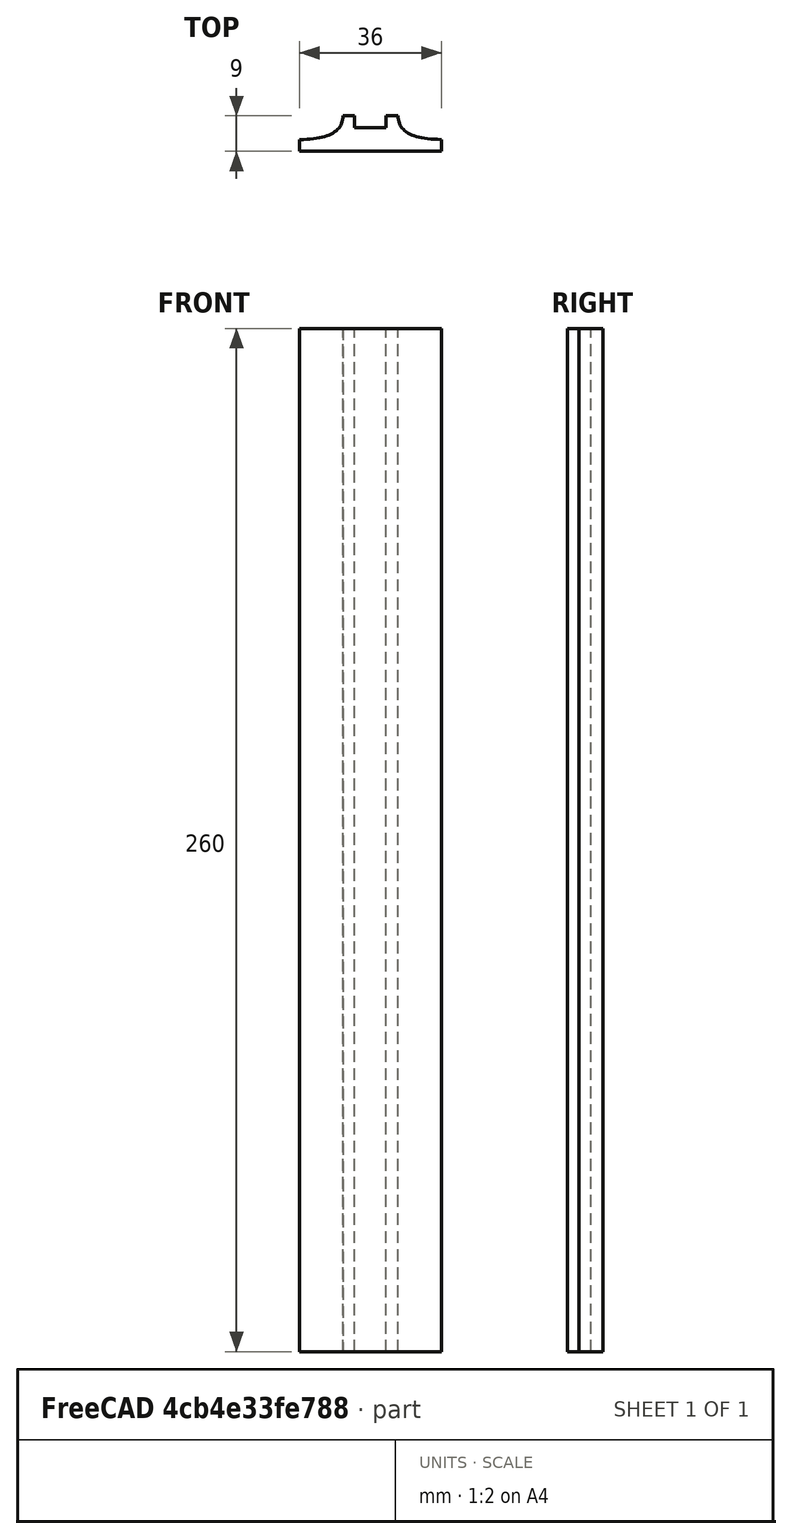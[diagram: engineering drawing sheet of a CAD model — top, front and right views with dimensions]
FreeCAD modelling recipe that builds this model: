
FCSTD DOCUMENT  (FreeCAD 0.19R0.19.2)
Label: laptopStand300.FCStd
License: All rights reserved
LicenseURL: http://en.wikipedia.org/wiki/All_rights_reserved
objects: Sketcher::SketchObject×11, Part::Extrusion×1
note: 12 computed .brp shape members not serialized (recipe doc carries the construction recipe); baked Part::Feature solids carry a one-line shape summary decoded from their .brp

FEATURE [Sketcher::SketchObject] Sketch001  label="legTop"
  FullyConstrained = true
  MapMode = 4
  Placement = pos=(0,0,0) rot=(0.57735,0.57735,0.57735;2.0944rad)
  sketch-geometry (41):
    g0: BSplineCurve PolesCount=3 KnotsCount=2 Degree=2 IsPeriodic=0
    g1: ArcOfCircle CenterX=73.1223 CenterY=-32.291 CenterZ=0 NormalX=0 NormalY=0 NormalZ=1 AngleXU=0 Radius=13 StartAngle=5.92268 EndAngle=9.06428
    g2: ArcOfCircle CenterX=66.7816 CenterY=-49.1439 CenterZ=0 NormalX=0 NormalY=0 NormalZ=1 AngleXU=0 Radius=13 StartAngle=2.78068 EndAngle=5.92131
    g3-g6: Circle x4 (B-spline internal-alignment scaffolding for g7; pole/knot coordinates omitted)
    g7: BSplineCurve PolesCount=4 KnotsCount=2 Degree=3 IsPeriodic=0
    g8: GeomPoint X=28.8094 Y=-19.0875 Z=0
    g9: GeomPoint X=47.0443 Y=-50.4712 Z=0
    g10: Circle CenterX=53.5586 CenterY=-23.2695 CenterZ=0 NormalX=0 NormalY=0 NormalZ=1 AngleXU=0 Radius=3.24518
    g11: LineSegment StartX=17.2232 StartY=-16.0875 StartZ=0 EndX=17.2232 EndY=-19.0875 EndZ=0
    g12: ArcOfCircle CenterX=17.2475 CenterY=-181.166 CenterZ=0 NormalX=0 NormalY=0 NormalZ=1 AngleXU=0 Radius=13 StartAngle=5.92268 EndAngle=7.49361
    g13: ArcOfCircle CenterX=29.5716 CenterY=-148.408 CenterZ=0 NormalX=0 NormalY=0 NormalZ=1 AngleXU=0 Radius=13 StartAngle=4.35228 EndAngle=5.92131
    g14: ArcOfCircle CenterX=35.8967 CenterY=-131.555 CenterZ=0 NormalX=0 NormalY=0 NormalZ=1 AngleXU=0 Radius=13 StartAngle=5.92268 EndAngle=7.49902
    g15: ArcOfCircle CenterX=48.1805 CenterY=-98.7782 CenterZ=0 NormalX=0 NormalY=0 NormalZ=1 AngleXU=0 Radius=13 StartAngle=4.34921 EndAngle=5.92131
    g16: ArcOfCircle CenterX=54.5183 CenterY=-81.9247 CenterZ=0 NormalX=0 NormalY=0 NormalZ=1 AngleXU=0 Radius=13 StartAngle=5.92268 EndAngle=8.70432
    g17: ArcOfCircle CenterX=20.184 CenterY=-217.506 CenterZ=0 NormalX=0 NormalY=0 NormalZ=1 AngleXU=0 Radius=3.81084 StartAngle=1.88136 EndAngle=6.80465
    g18: ArcOfCircle CenterX=36.3663 CenterY=-113.042 CenterZ=0 NormalX=0 NormalY=0 NormalZ=1 AngleXU=0 Radius=3.60555 StartAngle=0.230024 EndAngle=5.3372
    g19: ArcOfCircle CenterX=17.7945 CenterY=-162.686 CenterZ=0 NormalX=0 NormalY=0 NormalZ=1 AngleXU=0 Radius=3.60555 StartAngle=0.230024 EndAngle=5.3372
    g20: ArcOfCircle CenterX=49.8795 CenterY=-62.6074 CenterZ=0 NormalX=0 NormalY=0 NormalZ=1 AngleXU=0 Radius=3.84187 StartAngle=4.46973 EndAngle=9.40343
    g21: LineSegment StartX=48.9563 StartY=-66.3367 StartZ=0 EndX=44.7488 EndY=-73.3482 EndZ=0
    g22: LineSegment StartX=41.085 StartY=-66.3176 StartZ=0 EndX=46.0385 EndY=-62.5254 EndZ=0
    g23: LineSegment StartX=47.0443 StartY=-50.4712 StartZ=0 EndX=41.085 EndY=-66.3176 EndZ=0
    g24: LineSegment StartX=17.2232 StartY=-16.0875 StartZ=0 EndX=117.223 EndY=-16.0875 EndZ=0
    g25: LineSegment StartX=28.8094 StartY=-19.0875 StartZ=0 EndX=17.2232 EndY=-19.0875 EndZ=0
    g26: LineSegment StartX=117.223 StartY=-16.0875 StartZ=0 EndX=117.223 EndY=-19.0875 EndZ=0
    g27: LineSegment StartX=85.2866 StartY=-36.8766 StartZ=0 EndX=78.9396 EndY=-53.7463 EndZ=0
    g28: LineSegment StartX=60.9579 StartY=-27.7053 StartZ=0 EndX=54.6191 EndY=-44.5532 EndZ=0
    g29: LineSegment StartX=23.4884 StartY=-215.608 StartZ=0 EndX=94.6579 EndY=-26.1359 EndZ=0
    g30: LineSegment StartX=19.0195 StartY=-213.878 StartZ=0 EndX=29.4118 EndY=-185.752 EndZ=0
    g31: LineSegment StartX=22.7134 StartY=-166.661 StartZ=0 EndX=21.8316 EndY=-169.001 EndZ=0
    g32: LineSegment StartX=19.9036 StartY=-165.61 StartZ=0 EndX=22.7134 EndY=-166.661 EndZ=0
    g33: LineSegment StartX=21.3051 StartY=-161.864 StartZ=0 EndX=24.1149 EndY=-162.915 EndZ=0
    g34: LineSegment StartX=24.1149 StartY=-162.915 StartZ=0 EndX=24.9906 EndY=-160.574 EndZ=0
    g35: LineSegment StartX=41.7296 StartY=-153.01 StartZ=0 EndX=48.061 EndY=-136.14 EndZ=0
    g36: LineSegment StartX=41.2852 StartY=-117.017 StartZ=0 EndX=40.4148 EndY=-119.365 EndZ=0
    g37: LineSegment StartX=38.4753 StartY=-115.966 StartZ=0 EndX=41.2852 EndY=-117.017 EndZ=0
    g38: LineSegment StartX=39.8769 StartY=-112.22 StartZ=0 EndX=42.6867 EndY=-113.271 EndZ=0
    g39: LineSegment StartX=42.6867 StartY=-113.271 StartZ=0 EndX=43.5622 EndY=-110.93 EndZ=0
    g40: LineSegment StartX=66.6827 StartY=-86.5104 StartZ=0 EndX=60.3386 EndY=-103.381 EndZ=0
  constraints (65):
    c: Block(g0)
    c: Block(g1)
    c: Block(g2)
    c: Weight(g3) = 1
    c: Equal(g3,g4)
    c: Equal(g3,g5)
    c: Equal(g3,g6)
    c: InternalAlignment(g3-g6 -> g7) x4
    c: InternalAlignment(g8,g7)
    c: InternalAlignment(g9,g7)
    c: Block(g10)
    c: Block(g7)
    c: Vertical(g11)
    c: Block(g12)
    c: Block(g13)
    c: Block(g14)
    c: Block(g15)
    c: Block(g16)
    c: Block(g17)
    c: Block(g18)
    c: Block(g19)
    c: Block(g20)
    c: Coincident(g21,g20)
    c: Coincident(g21,g16)
    c: Coincident(g22,g20)
    c: Block(g22)
    c: Coincident(g23,g7)
    c: Coincident(g23,g22)
    c: Coincident(g24,g11)
    c: Horizontal(g24)
    c: Coincident(g25,g7)
    c: Coincident(g25,g11)
    c: Horizontal(g25)
    c: Coincident(g26,g24)
    c: Coincident(g26,g0)
    c: Vertical(g26)
    c: Block(g24)
    c: Coincident(g27,g1)
    c: Coincident(g27,g2)
    c: Coincident(g28,g1)
    c: Coincident(g28,g2)
    c: Coincident(g29,g17)
    c: Coincident(g29,g0)
    c: Coincident(g30,g17)
    c: Coincident(g30,g12)
    c: Coincident(g31,g12)
    c: Coincident(g32,g19)
    c: Coincident(g32,g31)
    c: Block(g31)
    c: Coincident(g33,g19)
    c: Coincident(g34,g33)
    c: Coincident(g34,g13)
    c: Block(g34)
    c: Coincident(g35,g13)
    c: Coincident(g35,g14)
    c: Coincident(g36,g14)
    c: Coincident(g37,g18)
    c: Coincident(g37,g36)
    c: Block(g36)
    c: Coincident(g38,g18)
    c: Coincident(g39,g38)
    c: Coincident(g39,g15)
    c: Block(g39)
    c: Coincident(g40,g16)
    c: Coincident(g40,g15)
FEATURE [Sketcher::SketchObject] Sketch002
  FullyConstrained = true
  sketch-geometry (20):
    g0: LineSegment StartX=-2.77179 StartY=-200.304 StartZ=0 EndX=5.22821 EndY=-200.304 EndZ=0
    g1: LineSegment StartX=5.22821 StartY=-200.304 StartZ=0 EndX=5.22821 EndY=-197.304 EndZ=0
    g2: LineSegment StartX=-2.77179 StartY=-200.304 StartZ=0 EndX=-2.77179 EndY=-197.304 EndZ=0
    g3: LineSegment StartX=5.22821 StartY=-197.304 StartZ=0 EndX=8.22821 EndY=-197.304 EndZ=0
    g4: LineSegment StartX=-2.77179 StartY=-197.304 StartZ=0 EndX=-5.77179 EndY=-197.304 EndZ=0
    g5: LineSegment StartX=19.2282 StartY=-203.304 StartZ=0 EndX=19.2282 EndY=-206.304 EndZ=0
    g6: LineSegment StartX=-16.7718 StartY=-203.304 StartZ=0 EndX=-16.7718 EndY=-206.304 EndZ=0
    g7: LineSegment StartX=-16.7718 StartY=-206.304 StartZ=0 EndX=19.2282 EndY=-206.304 EndZ=0
    g8: Circle CenterX=-16.7718 CenterY=-203.304 CenterZ=0 NormalX=0 NormalY=0 NormalZ=1 AngleXU=0 Radius=1
    g9: Circle CenterX=-5.77179 CenterY=-203.304 CenterZ=0 NormalX=0 NormalY=0 NormalZ=1 AngleXU=0 Radius=1
    g10: Circle CenterX=-5.77179 CenterY=-197.304 CenterZ=0 NormalX=0 NormalY=0 NormalZ=1 AngleXU=0 Radius=1
    g11: BSplineCurve PolesCount=3 KnotsCount=2 Degree=2 IsPeriodic=0
    g12: GeomPoint X=-16.7718 Y=-203.304 Z=0
    g13: GeomPoint X=-5.77179 Y=-197.304 Z=0
    g14: Circle CenterX=19.2282 CenterY=-203.304 CenterZ=0 NormalX=0 NormalY=0 NormalZ=1 AngleXU=0 Radius=1
    g15: Circle CenterX=8.22821 CenterY=-203.304 CenterZ=0 NormalX=0 NormalY=0 NormalZ=1 AngleXU=0 Radius=1
    g16: Circle CenterX=8.22821 CenterY=-197.304 CenterZ=0 NormalX=0 NormalY=0 NormalZ=1 AngleXU=0 Radius=1
    g17: BSplineCurve PolesCount=3 KnotsCount=2 Degree=2 IsPeriodic=0
    g18: GeomPoint X=19.2282 Y=-203.304 Z=0
    g19: GeomPoint X=8.22821 Y=-197.304 Z=0
  constraints (41):
    c: Horizontal(g0)
    c: Distance(g0) = 8
    c: Coincident(g1,g0)
    c: Vertical(g1)
    c: Distance(g1) = 3
    c: Coincident(g2,g0)
    c: Vertical(g2)
    c: Distance(g2) = 3
    c: Coincident(g3,g1)
    c: Horizontal(g3)
    c: Distance(g3) = 3
    c: Coincident(g4,g2)
    c: Horizontal(g4)
    c: Distance(g4) = 3
    c: Vertical(g5)
    c: Vertical(g6)
    c: Coincident(g7,g6)
    c: Coincident(g7,g5)
    c: Weight(g8) = 1
    c: Equal(g8,g9)
    c: Equal(g8,g10)
    c: Coincident(g11,g4)
    c: InternalAlignment(g8,g11)
    c: InternalAlignment(g9,g11)
    c: InternalAlignment(g10,g11)
    c: InternalAlignment(g12,g11)
    c: InternalAlignment(g13,g11)
    c: Coincident(g17,g5)
    c: Weight(g14) = 1
    c: Equal(g14,g15)
    c: Equal(g14,g16)
    c: Coincident(g17,g3)
    c: InternalAlignment(g14,g17)
    c: InternalAlignment(g15,g17)
    c: InternalAlignment(g16,g17)
    c: InternalAlignment(g18,g17)
    c: InternalAlignment(g19,g17)
    c: Block(g7)
    c: Block(g17)
    c: Block(g11)
    c: Block(g6)
FEATURE [Part::Extrusion] Extrude003
  Base = -> Sketch002
  Dir = (0,0,1)
  DirMode = 2
  FaceMakerClass = Part::FaceMakerBullseye
  LengthFwd = 260
  LengthRev = 0
  Solid = true
  Symmetric = false
FEATURE [Sketcher::SketchObject] Sketch003  label="original"
  FullyConstrained = false
  sketch-geometry (469):
    g0: LineSegment StartX=-42.9272 StartY=136.221 StartZ=0 EndX=-42.9272 EndY=-103.779 EndZ=0
    g1: LineSegment StartX=407.073 StartY=136.221 StartZ=0 EndX=407.073 EndY=-103.779 EndZ=0
    g2: ArcOfCircle CenterX=-26.9272 CenterY=-83.7794 CenterZ=0 NormalX=0 NormalY=0 NormalZ=1 AngleXU=0 Radius=8 StartAngle=3.14159 EndAngle=6.28319
    g3: ArcOfCircle CenterX=391.073 CenterY=-83.7794 CenterZ=0 NormalX=0 NormalY=0 NormalZ=1 AngleXU=0 Radius=8 StartAngle=3.14159 EndAngle=6.28319
    g4: Circle CenterX=175.022 CenterY=27.0628 CenterZ=0 NormalX=0 NormalY=0 NormalZ=1 AngleXU=0 Radius=1
    g5: Circle CenterX=179.022 CenterY=24.8665 CenterZ=0 NormalX=0 NormalY=0 NormalZ=1 AngleXU=0 Radius=1
    g6: Circle CenterX=179.022 CenterY=27.0628 CenterZ=0 NormalX=0 NormalY=0 NormalZ=1 AngleXU=0 Radius=1
    g7: BSplineCurve PolesCount=3 KnotsCount=2 Degree=2 IsPeriodic=0
    g8: GeomPoint X=175.022 Y=27.0628 Z=0
    g9: GeomPoint X=179.022 Y=27.0628 Z=0
    g10: Circle CenterX=189.124 CenterY=27.0628 CenterZ=0 NormalX=0 NormalY=0 NormalZ=1 AngleXU=0 Radius=1
    g11: Circle CenterX=185.124 CenterY=24.8665 CenterZ=0 NormalX=0 NormalY=0 NormalZ=1 AngleXU=0 Radius=1
    g12: Circle CenterX=185.124 CenterY=27.0628 CenterZ=0 NormalX=0 NormalY=0 NormalZ=1 AngleXU=0 Radius=1
    g13: BSplineCurve PolesCount=3 KnotsCount=2 Degree=2 IsPeriodic=0
    g14: GeomPoint X=189.124 Y=27.0628 Z=0
    g15: GeomPoint X=185.124 Y=27.0628 Z=0
    g16: Circle CenterX=175.022 CenterY=5.37834 CenterZ=0 NormalX=0 NormalY=0 NormalZ=1 AngleXU=0 Radius=1
    g17: Circle CenterX=179.022 CenterY=7.57463 CenterZ=0 NormalX=0 NormalY=0 NormalZ=1 AngleXU=0 Radius=1
    g18: Circle CenterX=179.022 CenterY=5.34704 CenterZ=0 NormalX=0 NormalY=0 NormalZ=1 AngleXU=0 Radius=1
    g19: BSplineCurve PolesCount=3 KnotsCount=2 Degree=2 IsPeriodic=0
    g20: GeomPoint X=175.022 Y=5.37834 Z=0
    g21: GeomPoint X=179.022 Y=5.34704 Z=0
    g22: Circle CenterX=189.124 CenterY=5.37834 CenterZ=0 NormalX=0 NormalY=0 NormalZ=1 AngleXU=0 Radius=1
    g23: Circle CenterX=185.124 CenterY=7.57463 CenterZ=0 NormalX=0 NormalY=0 NormalZ=1 AngleXU=0 Radius=1
    g24: Circle CenterX=185.124 CenterY=5.34704 CenterZ=0 NormalX=0 NormalY=0 NormalZ=1 AngleXU=0 Radius=1
    g25: BSplineCurve PolesCount=3 KnotsCount=2 Degree=2 IsPeriodic=0
    g26: GeomPoint X=189.124 Y=5.37834 Z=0
    g27: GeomPoint X=185.124 Y=5.34704 Z=0
    g28: Circle CenterX=165.871 CenterY=18.1458 CenterZ=0 NormalX=0 NormalY=0 NormalZ=1 AngleXU=0 Radius=1
    g29: Circle CenterX=169.377 CenterY=16.2206 CenterZ=0 NormalX=0 NormalY=0 NormalZ=1 AngleXU=0 Radius=1
    g30: Circle CenterX=165.871 CenterY=14.2956 CenterZ=0 NormalX=0 NormalY=0 NormalZ=1 AngleXU=0 Radius=1
    g31: BSplineCurve PolesCount=3 KnotsCount=2 Degree=2 IsPeriodic=0
    g32: GeomPoint X=165.871 Y=18.1458 Z=0
    g33: GeomPoint X=165.871 Y=14.2956 Z=0
    g34: Circle CenterX=198.275 CenterY=18.1318 CenterZ=0 NormalX=0 NormalY=0 NormalZ=1 AngleXU=0 Radius=1
    g35: Circle CenterX=194.768 CenterY=16.2206 CenterZ=0 NormalX=0 NormalY=0 NormalZ=1 AngleXU=0 Radius=1
    g36: Circle CenterX=198.264 CenterY=14.2963 CenterZ=0 NormalX=0 NormalY=0 NormalZ=1 AngleXU=0 Radius=1
    g37: BSplineCurve PolesCount=3 KnotsCount=2 Degree=2 IsPeriodic=0
    g38: GeomPoint X=198.275 Y=18.1318 Z=0
    g39: GeomPoint X=198.264 Y=14.2963 Z=0
    g40: LineSegment StartX=407.073 StartY=-103.779 StartZ=0 EndX=-42.9272 EndY=-103.779 EndZ=0
    g41: Circle CenterX=125.607 CenterY=54.1951 CenterZ=0 NormalX=0 NormalY=0 NormalZ=1 AngleXU=0 Radius=1
    g42: Circle CenterX=139.632 CenterY=46.4944 CenterZ=0 NormalX=0 NormalY=0 NormalZ=1 AngleXU=0 Radius=1
    g43: Circle CenterX=127.326 CenterY=56.7187 CenterZ=0 NormalX=0 NormalY=0 NormalZ=1 AngleXU=0 Radius=1
    g44: BSplineCurve PolesCount=3 KnotsCount=2 Degree=2 IsPeriodic=0
    g45: GeomPoint X=125.607 Y=54.1951 Z=0
    g46: GeomPoint X=127.326 Y=56.7187 Z=0
    g47: Circle CenterX=236.824 CenterY=56.7187 CenterZ=0 NormalX=0 NormalY=0 NormalZ=1 AngleXU=0 Radius=1
    g48: Circle CenterX=224.513 CenterY=46.4944 CenterZ=0 NormalX=0 NormalY=0 NormalZ=1 AngleXU=0 Radius=1
    g49: Circle CenterX=238.538 CenterY=54.1951 CenterZ=0 NormalX=0 NormalY=0 NormalZ=1 AngleXU=0 Radius=1
    g50: BSplineCurve PolesCount=3 KnotsCount=2 Degree=2 IsPeriodic=0
    g51: GeomPoint X=236.824 Y=56.7187 Z=0
    g52: GeomPoint X=238.538 Y=54.1951 Z=0
    g53: Circle CenterX=238.538 CenterY=-21.7516 CenterZ=0 NormalX=0 NormalY=0 NormalZ=1 AngleXU=0 Radius=1
    g54: Circle CenterX=224.513 CenterY=-14.0532 CenterZ=0 NormalX=0 NormalY=0 NormalZ=1 AngleXU=0 Radius=1
    g55: Circle CenterX=236.584 CenterY=-24.2775 CenterZ=0 NormalX=0 NormalY=0 NormalZ=1 AngleXU=0 Radius=1
    g56: BSplineCurve PolesCount=3 KnotsCount=2 Degree=2 IsPeriodic=0
    g57: GeomPoint X=238.538 Y=-21.7516 Z=0
    g58: GeomPoint X=236.584 Y=-24.2775 Z=0
    g59: Circle CenterX=125.607 CenterY=-21.7539 CenterZ=0 NormalX=0 NormalY=0 NormalZ=1 AngleXU=0 Radius=1
    g60: Circle CenterX=139.632 CenterY=-14.0532 CenterZ=0 NormalX=0 NormalY=0 NormalZ=1 AngleXU=0 Radius=1
    g61: Circle CenterX=127.325 CenterY=-24.2775 CenterZ=0 NormalX=0 NormalY=0 NormalZ=1 AngleXU=0 Radius=1
    g62: BSplineCurve PolesCount=3 KnotsCount=2 Degree=2 IsPeriodic=0
    g63: GeomPoint X=125.607 Y=-21.7539 Z=0
    g64: GeomPoint X=127.325 Y=-24.2775 Z=0
    g65: Circle CenterX=302.996 CenterY=111.695 CenterZ=0 NormalX=0 NormalY=0 NormalZ=1 AngleXU=0 Radius=1
    g66: Circle CenterX=306.073 CenterY=114.251 CenterZ=0 NormalX=0 NormalY=0 NormalZ=1 AngleXU=0 Radius=1
    g67: Circle CenterX=306.073 CenterY=110.251 CenterZ=0 NormalX=0 NormalY=0 NormalZ=1 AngleXU=0 Radius=1
    g68: BSplineCurve PolesCount=3 KnotsCount=2 Degree=2 IsPeriodic=0
    g69: GeomPoint X=302.996 Y=111.695 Z=0
    g70: GeomPoint X=306.073 Y=110.251 Z=0
    g71: Circle CenterX=306.073 CenterY=95.2763 CenterZ=0 NormalX=0 NormalY=0 NormalZ=1 AngleXU=0 Radius=1
    g72: Circle CenterX=306.073 CenterY=91.2763 CenterZ=0 NormalX=0 NormalY=0 NormalZ=1 AngleXU=0 Radius=1
    g73: Circle CenterX=302.567 CenterY=89.3511 CenterZ=0 NormalX=0 NormalY=0 NormalZ=1 AngleXU=0 Radius=1
    g74: BSplineCurve PolesCount=3 KnotsCount=2 Degree=2 IsPeriodic=0
    g75: GeomPoint X=306.073 Y=95.2763 Z=0
    g76: GeomPoint X=302.567 Y=89.3511 Z=0
    g77: LineSegment StartX=306.073 StartY=110.251 StartZ=0 EndX=306.073 EndY=95.2763 EndZ=0
    g78: LineSegment StartX=302.996 StartY=111.695 StartZ=0 EndX=236.824 EndY=56.7187 EndZ=0
    g79: LineSegment StartX=238.538 StartY=54.1951 StartZ=0 EndX=302.567 EndY=89.3511 EndZ=0
    g80: Circle CenterX=61.1496 CenterY=111.695 CenterZ=0 NormalX=0 NormalY=0 NormalZ=1 AngleXU=0 Radius=1
    g81: Circle CenterX=58.0728 CenterY=114.251 CenterZ=0 NormalX=0 NormalY=0 NormalZ=1 AngleXU=0 Radius=1
    g82: Circle CenterX=58.0728 CenterY=110.251 CenterZ=0 NormalX=0 NormalY=0 NormalZ=1 AngleXU=0 Radius=1
    g83: BSplineCurve PolesCount=3 KnotsCount=2 Degree=2 IsPeriodic=0
    g84: GeomPoint X=61.1496 Y=111.695 Z=0
    g85: GeomPoint X=58.0728 Y=110.251 Z=0
    g86: Circle CenterX=61.5791 CenterY=89.3511 CenterZ=0 NormalX=0 NormalY=0 NormalZ=1 AngleXU=0 Radius=1
    g87: Circle CenterX=58.0728 CenterY=91.2763 CenterZ=0 NormalX=0 NormalY=0 NormalZ=1 AngleXU=0 Radius=1
    g88: Circle CenterX=58.0728 CenterY=95.2763 CenterZ=0 NormalX=0 NormalY=0 NormalZ=1 AngleXU=0 Radius=1
    g89: BSplineCurve PolesCount=3 KnotsCount=2 Degree=2 IsPeriodic=0
    g90: GeomPoint X=61.5791 Y=89.3511 Z=0
    g91: GeomPoint X=58.0728 Y=95.2763 Z=0
    g92: LineSegment StartX=58.0728 StartY=110.251 StartZ=0 EndX=58.0728 EndY=95.2763 EndZ=0
    g93: LineSegment StartX=61.1496 StartY=111.695 StartZ=0 EndX=127.326 EndY=56.7187 EndZ=0
    g94: LineSegment StartX=125.607 StartY=54.1951 StartZ=0 EndX=61.5791 EndY=89.3511 EndZ=0
    g95: Circle CenterX=61.5791 CenterY=-56.9099 CenterZ=0 NormalX=0 NormalY=0 NormalZ=1 AngleXU=0 Radius=1
    g96: Circle CenterX=58.0728 CenterY=-58.8351 CenterZ=0 NormalX=0 NormalY=0 NormalZ=1 AngleXU=0 Radius=1
    g97: Circle CenterX=58.0728 CenterY=-62.8351 CenterZ=0 NormalX=0 NormalY=0 NormalZ=1 AngleXU=0 Radius=1
    g98: BSplineCurve PolesCount=3 KnotsCount=2 Degree=2 IsPeriodic=0
    g99: GeomPoint X=61.5791 Y=-56.9099 Z=0
    g100: GeomPoint X=58.0728 Y=-62.8351 Z=0
    g101: Circle CenterX=58.0728 CenterY=-77.8102 CenterZ=0 NormalX=0 NormalY=0 NormalZ=1 AngleXU=0 Radius=1
    g102: Circle CenterX=58.0728 CenterY=-81.8102 CenterZ=0 NormalX=0 NormalY=0 NormalZ=1 AngleXU=0 Radius=1
    g103: Circle CenterX=61.1496 CenterY=-79.2541 CenterZ=0 NormalX=0 NormalY=0 NormalZ=1 AngleXU=0 Radius=1
    g104: BSplineCurve PolesCount=3 KnotsCount=2 Degree=2 IsPeriodic=0
    g105: GeomPoint X=58.0728 Y=-77.8102 Z=0
    g106: GeomPoint X=61.1496 Y=-79.2541 Z=0
    g107: LineSegment StartX=58.0728 StartY=-62.8351 StartZ=0 EndX=58.0728 EndY=-77.8102 EndZ=0
    g108: LineSegment StartX=61.1496 StartY=-79.2541 StartZ=0 EndX=127.325 EndY=-24.2775 EndZ=0
    g109: LineSegment StartX=125.607 StartY=-21.7539 StartZ=0 EndX=61.5791 EndY=-56.9099 EndZ=0
    g110: Circle CenterX=302.567 CenterY=-56.9099 CenterZ=0 NormalX=0 NormalY=0 NormalZ=1 AngleXU=0 Radius=1
    g111: Circle CenterX=306.073 CenterY=-58.8351 CenterZ=0 NormalX=0 NormalY=0 NormalZ=1 AngleXU=0 Radius=1
    g112: Circle CenterX=306.073 CenterY=-62.8351 CenterZ=0 NormalX=0 NormalY=0 NormalZ=1 AngleXU=0 Radius=1
    g113: BSplineCurve PolesCount=3 KnotsCount=2 Degree=2 IsPeriodic=0
    g114: GeomPoint X=302.567 Y=-56.9099 Z=0
    g115: GeomPoint X=306.073 Y=-62.8351 Z=0
    g116: Circle CenterX=302.996 CenterY=-79.2541 CenterZ=0 NormalX=0 NormalY=0 NormalZ=1 AngleXU=0 Radius=1
    g117: Circle CenterX=306.073 CenterY=-81.8102 CenterZ=0 NormalX=0 NormalY=0 NormalZ=1 AngleXU=0 Radius=1
    g118: Circle CenterX=306.073 CenterY=-77.8102 CenterZ=0 NormalX=0 NormalY=0 NormalZ=1 AngleXU=0 Radius=1
    g119: BSplineCurve PolesCount=3 KnotsCount=2 Degree=2 IsPeriodic=0
    g120: GeomPoint X=302.996 Y=-79.2541 Z=0
    g121: GeomPoint X=306.073 Y=-77.8102 Z=0
    g122: LineSegment StartX=306.073 StartY=-62.8351 StartZ=0 EndX=306.073 EndY=-77.8102 EndZ=0
    g123: LineSegment StartX=302.996 StartY=-79.2541 StartZ=0 EndX=236.584 EndY=-24.2775 EndZ=0
    g124: LineSegment StartX=238.538 StartY=-21.7516 StartZ=0 EndX=302.567 EndY=-56.9099 EndZ=0
    g125: Circle CenterX=61.6457 CenterY=-88.8112 CenterZ=0 NormalX=0 NormalY=0 NormalZ=1 AngleXU=0 Radius=1
    g126: Circle CenterX=58.0728 CenterY=-91.7794 CenterZ=0 NormalX=0 NormalY=0 NormalZ=1 AngleXU=0 Radius=1
    g127: Circle CenterX=63.9135 CenterY=-91.7791 CenterZ=0 NormalX=0 NormalY=0 NormalZ=1 AngleXU=0 Radius=1
    g128: BSplineCurve PolesCount=3 KnotsCount=2 Degree=2 IsPeriodic=0
    g129: GeomPoint X=61.6457 Y=-88.8112 Z=0
    g130: GeomPoint X=63.9135 Y=-91.7791 Z=0
    g131: Circle CenterX=179.022 CenterY=-85.8163 CenterZ=0 NormalX=0 NormalY=0 NormalZ=1 AngleXU=0 Radius=1
    g132: Circle CenterX=179.022 CenterY=-91.7794 CenterZ=0 NormalX=0 NormalY=0 NormalZ=1 AngleXU=0 Radius=1
    g133: Circle CenterX=171.895 CenterY=-91.7791 CenterZ=0 NormalX=0 NormalY=0 NormalZ=1 AngleXU=0 Radius=1
    g134: BSplineCurve PolesCount=3 KnotsCount=2 Degree=2 IsPeriodic=0
    g135: GeomPoint X=179.022 Y=-85.8163 Z=0
    g136: GeomPoint X=171.895 Y=-91.7791 Z=0
    g137: Circle CenterX=185.124 CenterY=-86.2028 CenterZ=0 NormalX=0 NormalY=0 NormalZ=1 AngleXU=0 Radius=1
    g138: Circle CenterX=185.124 CenterY=-91.7794 CenterZ=0 NormalX=0 NormalY=0 NormalZ=1 AngleXU=0 Radius=1
    g139: Circle CenterX=191.747 CenterY=-91.7794 CenterZ=0 NormalX=0 NormalY=0 NormalZ=1 AngleXU=0 Radius=1
    g140: BSplineCurve PolesCount=3 KnotsCount=2 Degree=2 IsPeriodic=0
    g141: GeomPoint X=185.124 Y=-86.2028 Z=0
    g142: GeomPoint X=191.747 Y=-91.7794 Z=0
    g143: Circle CenterX=299.888 CenterY=-86.6413 CenterZ=0 NormalX=0 NormalY=0 NormalZ=1 AngleXU=0 Radius=1
    g144: Circle CenterX=306.073 CenterY=-91.7794 CenterZ=0 NormalX=0 NormalY=0 NormalZ=1 AngleXU=0 Radius=1
    g145: Circle CenterX=298.776 CenterY=-91.7794 CenterZ=0 NormalX=0 NormalY=0 NormalZ=1 AngleXU=0 Radius=1
    g146: BSplineCurve PolesCount=3 KnotsCount=2 Degree=2 IsPeriodic=0
    g147: GeomPoint X=299.888 Y=-86.6413 Z=0
    g148: GeomPoint X=298.776 Y=-91.7794 Z=0
    g149: LineSegment StartX=189.124 StartY=5.37834 StartZ=0 EndX=299.888 EndY=-86.6413 EndZ=0
    g150: LineSegment StartX=298.776 StartY=-91.7794 StartZ=0 EndX=191.747 EndY=-91.7794 EndZ=0
    g151: LineSegment StartX=185.124 StartY=-86.2028 StartZ=0 EndX=185.124 EndY=5.34704 EndZ=0
    g152: LineSegment StartX=179.022 StartY=5.34704 StartZ=0 EndX=179.022 EndY=-85.8163 EndZ=0
    g153: LineSegment StartX=171.895 StartY=-91.7791 StartZ=0 EndX=63.9135 EndY=-91.7791 EndZ=0
    g154: LineSegment StartX=61.6457 StartY=-88.8112 StartZ=0 EndX=175.022 EndY=5.37834 EndZ=0
    g155: Circle CenterX=302.073 CenterY=124.221 CenterZ=0 NormalX=0 NormalY=0 NormalZ=1 AngleXU=0 Radius=1
    g156: Circle CenterX=306.073 CenterY=124.221 CenterZ=0 NormalX=0 NormalY=0 NormalZ=1 AngleXU=0 Radius=1
    g157: Circle CenterX=302.996 CenterY=121.665 CenterZ=0 NormalX=0 NormalY=0 NormalZ=1 AngleXU=0 Radius=1
    g158: BSplineCurve PolesCount=3 KnotsCount=2 Degree=2 IsPeriodic=0
    g159: GeomPoint X=302.073 Y=124.221 Z=0
    g160: GeomPoint X=302.996 Y=121.665 Z=0
    g161: Circle CenterX=189.124 CenterY=124.221 CenterZ=0 NormalX=0 NormalY=0 NormalZ=1 AngleXU=0 Radius=1
    g162: Circle CenterX=185.124 CenterY=124.221 CenterZ=0 NormalX=0 NormalY=0 NormalZ=1 AngleXU=0 Radius=1
    g163: Circle CenterX=185.124 CenterY=120.221 CenterZ=0 NormalX=0 NormalY=0 NormalZ=1 AngleXU=0 Radius=1
    g164: BSplineCurve PolesCount=3 KnotsCount=2 Degree=2 IsPeriodic=0
    g165: GeomPoint X=189.124 Y=124.221 Z=0
    g166: GeomPoint X=185.124 Y=120.221 Z=0
    g167: Circle CenterX=175.022 CenterY=124.221 CenterZ=0 NormalX=0 NormalY=0 NormalZ=1 AngleXU=0 Radius=1
    g168: Circle CenterX=179.022 CenterY=124.221 CenterZ=0 NormalX=0 NormalY=0 NormalZ=1 AngleXU=0 Radius=1
    g169: Circle CenterX=179.022 CenterY=120.221 CenterZ=0 NormalX=0 NormalY=0 NormalZ=1 AngleXU=0 Radius=1
    g170: BSplineCurve PolesCount=3 KnotsCount=2 Degree=2 IsPeriodic=0
    g171: GeomPoint X=175.022 Y=124.221 Z=0
    g172: GeomPoint X=179.022 Y=120.221 Z=0
    g173: Circle CenterX=62.0728 CenterY=124.221 CenterZ=0 NormalX=0 NormalY=0 NormalZ=1 AngleXU=0 Radius=1
    g174: Circle CenterX=58.0728 CenterY=124.221 CenterZ=0 NormalX=0 NormalY=0 NormalZ=1 AngleXU=0 Radius=1
    g175: Circle CenterX=61.1496 CenterY=121.665 CenterZ=0 NormalX=0 NormalY=0 NormalZ=1 AngleXU=0 Radius=1
    g176: BSplineCurve PolesCount=3 KnotsCount=2 Degree=2 IsPeriodic=0
    g177: GeomPoint X=62.0728 Y=124.221 Z=0
    g178: GeomPoint X=61.1496 Y=121.665 Z=0
    g179: LineSegment StartX=179.022 StartY=120.221 StartZ=0 EndX=179.022 EndY=27.0628 EndZ=0
    g180: LineSegment StartX=185.124 StartY=27.0628 StartZ=0 EndX=185.124 EndY=120.221 EndZ=0
    g181: LineSegment StartX=302.996 StartY=121.665 StartZ=0 EndX=189.124 EndY=27.0628 EndZ=0
    g182: LineSegment StartX=175.022 StartY=27.0628 StartZ=0 EndX=61.1496 EndY=121.665 EndZ=0
    g183: Circle CenterX=61.5791 CenterY=75.4095 CenterZ=0 NormalX=0 NormalY=0 NormalZ=1 AngleXU=0 Radius=1
    g184: Circle CenterX=58.0728 CenterY=77.3346 CenterZ=0 NormalX=0 NormalY=0 NormalZ=1 AngleXU=0 Radius=1
    g185: Circle CenterX=58.0728 CenterY=73.3346 CenterZ=0 NormalX=0 NormalY=0 NormalZ=1 AngleXU=0 Radius=1
    g186: BSplineCurve PolesCount=3 KnotsCount=2 Degree=2 IsPeriodic=0
    g187: GeomPoint X=61.5791 Y=75.4095 Z=0
    g188: GeomPoint X=58.0728 Y=73.3346 Z=0
    g189: Circle CenterX=58.0728 CenterY=-40.8935 CenterZ=0 NormalX=0 NormalY=0 NormalZ=1 AngleXU=0 Radius=1
    g190: Circle CenterX=58.0728 CenterY=-44.8935 CenterZ=0 NormalX=0 NormalY=0 NormalZ=1 AngleXU=0 Radius=1
    g191: Circle CenterX=61.5791 CenterY=-42.9683 CenterZ=0 NormalX=0 NormalY=0 NormalZ=1 AngleXU=0 Radius=1
    g192: BSplineCurve PolesCount=3 KnotsCount=2 Degree=2 IsPeriodic=0
    g193: GeomPoint X=58.0728 Y=-40.8935 Z=0
    g194: GeomPoint X=61.5791 Y=-42.9683 Z=0
    g195: LineSegment StartX=61.5791 StartY=-42.9683 StartZ=0 EndX=165.871 EndY=14.2956 EndZ=0
    g196: LineSegment StartX=165.871 StartY=18.1458 StartZ=0 EndX=61.5791 EndY=75.4095 EndZ=0
    g197: LineSegment StartX=58.0728 StartY=73.3346 StartZ=0 EndX=58.0728 EndY=-40.8935 EndZ=0
    g198: Circle CenterX=302.567 CenterY=-42.9683 CenterZ=0 NormalX=0 NormalY=0 NormalZ=1 AngleXU=0 Radius=1
    g199: Circle CenterX=306.073 CenterY=-44.8935 CenterZ=0 NormalX=0 NormalY=0 NormalZ=1 AngleXU=0 Radius=1
    g200: Circle CenterX=306.073 CenterY=-40.8935 CenterZ=0 NormalX=0 NormalY=0 NormalZ=1 AngleXU=0 Radius=1
    g201: BSplineCurve PolesCount=3 KnotsCount=2 Degree=2 IsPeriodic=0
    g202: GeomPoint X=302.567 Y=-42.9683 Z=0
    g203: GeomPoint X=306.073 Y=-40.8935 Z=0
    g204: Circle CenterX=306.073 CenterY=73.3346 CenterZ=0 NormalX=0 NormalY=0 NormalZ=1 AngleXU=0 Radius=1
    g205: Circle CenterX=306.073 CenterY=77.3346 CenterZ=0 NormalX=0 NormalY=0 NormalZ=1 AngleXU=0 Radius=1
    g206: Circle CenterX=302.535 CenterY=75.4095 CenterZ=0 NormalX=0 NormalY=0 NormalZ=1 AngleXU=0 Radius=1
    g207: BSplineCurve PolesCount=3 KnotsCount=2 Degree=2 IsPeriodic=0
    g208: GeomPoint X=306.073 Y=73.3346 Z=0
    g209: GeomPoint X=302.535 Y=75.4095 Z=0
    g210: LineSegment StartX=302.567 StartY=-42.9683 StartZ=0 EndX=198.264 EndY=14.2963 EndZ=0
    g211: LineSegment StartX=198.275 StartY=18.1318 StartZ=0 EndX=302.535 EndY=75.4095 EndZ=0
    g212: LineSegment StartX=306.073 StartY=73.3346 StartZ=0 EndX=306.073 EndY=-40.8935 EndZ=0
    g213: LineSegment StartX=322.073 StartY=105.865 StartZ=0 EndX=328.643 EndY=105.865 EndZ=0
    g214: LineSegment StartX=318.073 StartY=120.221 StartZ=0 EndX=318.073 EndY=109.865 EndZ=0
    g215: LineSegment StartX=336.157 StartY=107.779 StartZ=0 EndX=362.567 EndY=122.294 EndZ=0
    g216: Circle CenterX=362.073 CenterY=124.221 CenterZ=0 NormalX=0 NormalY=0 NormalZ=1 AngleXU=0 Radius=1
    g217: Circle CenterX=366.073 CenterY=124.221 CenterZ=0 NormalX=0 NormalY=0 NormalZ=1 AngleXU=0 Radius=1
    g218: Circle CenterX=362.567 CenterY=122.294 CenterZ=0 NormalX=0 NormalY=0 NormalZ=1 AngleXU=0 Radius=1
    g219: BSplineCurve PolesCount=3 KnotsCount=2 Degree=2 IsPeriodic=0
    g220: GeomPoint X=362.073 Y=124.221 Z=0
    g221: GeomPoint X=362.567 Y=122.294 Z=0
    g222: Circle CenterX=322.073 CenterY=124.221 CenterZ=0 NormalX=0 NormalY=0 NormalZ=1 AngleXU=0 Radius=1
    g223: Circle CenterX=318.073 CenterY=124.221 CenterZ=0 NormalX=0 NormalY=0 NormalZ=1 AngleXU=0 Radius=1
    g224: Circle CenterX=318.073 CenterY=120.221 CenterZ=0 NormalX=0 NormalY=0 NormalZ=1 AngleXU=0 Radius=1
    g225: BSplineCurve PolesCount=3 KnotsCount=2 Degree=2 IsPeriodic=0
    g226: GeomPoint X=322.073 Y=124.221 Z=0
    g227: GeomPoint X=318.073 Y=120.221 Z=0
    g228: Circle CenterX=322.073 CenterY=105.865 CenterZ=0 NormalX=0 NormalY=0 NormalZ=1 AngleXU=0 Radius=1
    g229: Circle CenterX=318.073 CenterY=105.865 CenterZ=0 NormalX=0 NormalY=0 NormalZ=1 AngleXU=0 Radius=1
    g230: Circle CenterX=318.073 CenterY=109.865 CenterZ=0 NormalX=0 NormalY=0 NormalZ=1 AngleXU=0 Radius=1
    g231: BSplineCurve PolesCount=3 KnotsCount=2 Degree=2 IsPeriodic=0
    g232: GeomPoint X=322.073 Y=105.865 Z=0
    g233: GeomPoint X=318.073 Y=109.865 Z=0
    g234: Circle CenterX=336.157 CenterY=107.779 CenterZ=0 NormalX=0 NormalY=0 NormalZ=1 AngleXU=0 Radius=1
    g235: Circle CenterX=332.651 CenterY=105.853 CenterZ=0 NormalX=0 NormalY=0 NormalZ=1 AngleXU=0 Radius=1
    g236: Circle CenterX=328.643 CenterY=105.865 CenterZ=0 NormalX=0 NormalY=0 NormalZ=1 AngleXU=0 Radius=1
    g237: BSplineCurve PolesCount=3 KnotsCount=2 Degree=2 IsPeriodic=0
    g238: GeomPoint X=336.157 Y=107.779 Z=0
    g239: GeomPoint X=328.643 Y=105.865 Z=0
    g240: LineSegment StartX=322.073 StartY=124.221 StartZ=0 EndX=362.073 EndY=124.221 EndZ=0
    g241: Circle CenterX=371.567 CenterY=-80.8644 CenterZ=0 NormalX=0 NormalY=0 NormalZ=1 AngleXU=0 Radius=1
    g242: Circle CenterX=375.073 CenterY=-82.7896 CenterZ=0 NormalX=0 NormalY=0 NormalZ=1 AngleXU=0 Radius=1
    g243: Circle CenterX=375.073 CenterY=-78.7896 CenterZ=0 NormalX=0 NormalY=0 NormalZ=1 AngleXU=0 Radius=1
    g244: BSplineCurve PolesCount=3 KnotsCount=2 Degree=2 IsPeriodic=0
    g245: GeomPoint X=371.567 Y=-80.8644 Z=0
    g246: GeomPoint X=375.073 Y=-78.7896 Z=0
    g247: Circle CenterX=321.579 CenterY=-53.4075 CenterZ=0 NormalX=0 NormalY=0 NormalZ=1 AngleXU=0 Radius=1
    g248: Circle CenterX=318.073 CenterY=-51.4823 CenterZ=0 NormalX=0 NormalY=0 NormalZ=1 AngleXU=0 Radius=1
    g249: Circle CenterX=318.073 CenterY=-47.4805 CenterZ=0 NormalX=0 NormalY=0 NormalZ=1 AngleXU=0 Radius=1
    g250: BSplineCurve PolesCount=3 KnotsCount=2 Degree=2 IsPeriodic=0
    g251: GeomPoint X=321.579 Y=-53.4075 Z=0
    g252: GeomPoint X=318.073 Y=-47.4805 Z=0
    g253: LineSegment StartX=371.567 StartY=-80.8644 StartZ=0 EndX=321.579 EndY=-53.4075 EndZ=0
    g254: Circle CenterX=321.579 CenterY=-67.3492 CenterZ=0 NormalX=0 NormalY=0 NormalZ=1 AngleXU=0 Radius=1
    g255: Circle CenterX=318.073 CenterY=-65.424 CenterZ=0 NormalX=0 NormalY=0 NormalZ=1 AngleXU=0 Radius=1
    g256: Circle CenterX=318.073 CenterY=-69.424 CenterZ=0 NormalX=0 NormalY=0 NormalZ=1 AngleXU=0 Radius=1
    g257: BSplineCurve PolesCount=3 KnotsCount=2 Degree=2 IsPeriodic=0
    g258: GeomPoint X=321.579 Y=-67.3492 Z=0
    g259: GeomPoint X=318.073 Y=-69.424 Z=0
    g260: Circle CenterX=362.567 CenterY=-89.8542 CenterZ=0 NormalX=0 NormalY=0 NormalZ=1 AngleXU=0 Radius=1
    g261: Circle CenterX=366.073 CenterY=-91.7794 CenterZ=0 NormalX=0 NormalY=0 NormalZ=1 AngleXU=0 Radius=1
    g262: Circle CenterX=362.073 CenterY=-91.7794 CenterZ=0 NormalX=0 NormalY=0 NormalZ=1 AngleXU=0 Radius=1
    g263: BSplineCurve PolesCount=3 KnotsCount=2 Degree=2 IsPeriodic=0
    g264: GeomPoint X=362.567 Y=-89.8542 Z=0
    g265: GeomPoint X=362.073 Y=-91.7794 Z=0
    g266: Circle CenterX=322.073 CenterY=-91.7794 CenterZ=0 NormalX=0 NormalY=0 NormalZ=1 AngleXU=0 Radius=1
    g267: Circle CenterX=318.073 CenterY=-91.7794 CenterZ=0 NormalX=0 NormalY=0 NormalZ=1 AngleXU=0 Radius=1
    g268: Circle CenterX=318.073 CenterY=-87.7794 CenterZ=0 NormalX=0 NormalY=0 NormalZ=1 AngleXU=0 Radius=1
    g269: BSplineCurve PolesCount=3 KnotsCount=2 Degree=2 IsPeriodic=0
    g270: GeomPoint X=322.073 Y=-91.7794 Z=0
    g271: GeomPoint X=318.073 Y=-87.7794 Z=0
    g272: LineSegment StartX=362.567 StartY=-89.8542 StartZ=0 EndX=321.579 EndY=-67.3492 EndZ=0
    g273: LineSegment StartX=318.073 StartY=-69.424 StartZ=0 EndX=318.073 EndY=-87.7794 EndZ=0
    g274: LineSegment StartX=322.073 StartY=-91.7794 StartZ=0 EndX=362.073 EndY=-91.7794 EndZ=0
    g275: Circle CenterX=2.07281 CenterY=124.221 CenterZ=0 NormalX=0 NormalY=0 NormalZ=1 AngleXU=0 Radius=1
    g276: Circle CenterX=1.57905 CenterY=122.295 CenterZ=0 NormalX=0 NormalY=0 NormalZ=1 AngleXU=0 Radius=1
    g277: BSplineCurve PolesCount=3 KnotsCount=2 Degree=2 IsPeriodic=0
    g278: GeomPoint X=2.07281 Y=124.221 Z=0
    g279: GeomPoint X=1.57905 Y=122.295 Z=0
    g280: Circle CenterX=42.0728 CenterY=124.221 CenterZ=0 NormalX=0 NormalY=0 NormalZ=1 AngleXU=0 Radius=1
    g281: Circle CenterX=46.0728 CenterY=124.221 CenterZ=0 NormalX=0 NormalY=0 NormalZ=1 AngleXU=0 Radius=1
    g282: Circle CenterX=46.0728 CenterY=120.221 CenterZ=0 NormalX=0 NormalY=0 NormalZ=1 AngleXU=0 Radius=1
    g283: BSplineCurve PolesCount=3 KnotsCount=2 Degree=2 IsPeriodic=0
    g284: GeomPoint X=42.0728 Y=124.221 Z=0
    g285: GeomPoint X=46.0728 Y=120.221 Z=0
    g286: Circle CenterX=46.0728 CenterY=109.865 CenterZ=0 NormalX=0 NormalY=0 NormalZ=1 AngleXU=0 Radius=1
    g287: Circle CenterX=46.0728 CenterY=105.865 CenterZ=0 NormalX=0 NormalY=0 NormalZ=1 AngleXU=0 Radius=1
    g288: Circle CenterX=42.0728 CenterY=105.865 CenterZ=0 NormalX=0 NormalY=0 NormalZ=1 AngleXU=0 Radius=1
    g289: BSplineCurve PolesCount=3 KnotsCount=2 Degree=2 IsPeriodic=0
    g290: GeomPoint X=46.0728 Y=109.865 Z=0
    g291: GeomPoint X=42.0728 Y=105.865 Z=0
    g292: Circle CenterX=35.5028 CenterY=105.865 CenterZ=0 NormalX=0 NormalY=0 NormalZ=1 AngleXU=0 Radius=1
    g293: Circle CenterX=31.5028 CenterY=105.865 CenterZ=0 NormalX=0 NormalY=0 NormalZ=1 AngleXU=0 Radius=1
    g294: Circle CenterX=27.9965 CenterY=107.79 CenterZ=0 NormalX=0 NormalY=0 NormalZ=1 AngleXU=0 Radius=1
    g295: BSplineCurve PolesCount=3 KnotsCount=2 Degree=2 IsPeriodic=0
    g296: GeomPoint X=35.5028 Y=105.865 Z=0
    g297: GeomPoint X=27.9965 Y=107.79 Z=0
    g298: LineSegment StartX=2.07281 StartY=124.221 StartZ=0 EndX=42.0728 EndY=124.221 EndZ=0
    g299: LineSegment StartX=46.0728 StartY=120.221 StartZ=0 EndX=46.0728 EndY=109.865 EndZ=0
    g300: LineSegment StartX=42.0728 StartY=105.865 StartZ=0 EndX=35.5028 EndY=105.865 EndZ=0
    g301: LineSegment StartX=27.9965 StartY=107.79 StartZ=0 EndX=1.57905 EndY=122.295 EndZ=0
    g302: Circle CenterX=42.5666 CenterY=-67.3492 CenterZ=0 NormalX=0 NormalY=0 NormalZ=1 AngleXU=0 Radius=1
    g303: Circle CenterX=46.0728 CenterY=-65.424 CenterZ=0 NormalX=0 NormalY=0 NormalZ=1 AngleXU=0 Radius=1
    g304: Circle CenterX=46.0728 CenterY=-69.424 CenterZ=0 NormalX=0 NormalY=0 NormalZ=1 AngleXU=0 Radius=1
    g305: BSplineCurve PolesCount=3 KnotsCount=2 Degree=2 IsPeriodic=0
    g306: GeomPoint X=42.5666 Y=-67.3492 Z=0
    g307: GeomPoint X=46.0728 Y=-69.424 Z=0
    g308: Circle CenterX=46.0728 CenterY=-87.7794 CenterZ=0 NormalX=0 NormalY=0 NormalZ=1 AngleXU=0 Radius=1
    g309: Circle CenterX=46.0728 CenterY=-91.7794 CenterZ=0 NormalX=0 NormalY=0 NormalZ=1 AngleXU=0 Radius=1
    g310: Circle CenterX=42.0728 CenterY=-91.7794 CenterZ=0 NormalX=0 NormalY=0 NormalZ=1 AngleXU=0 Radius=1
    g311: BSplineCurve PolesCount=3 KnotsCount=2 Degree=2 IsPeriodic=0
    g312: GeomPoint X=46.0728 Y=-87.7794 Z=0
    g313: GeomPoint X=42.0728 Y=-91.7794 Z=0
    g314: Circle CenterX=2.07281 CenterY=-91.7794 CenterZ=0 NormalX=0 NormalY=0 NormalZ=1 AngleXU=0 Radius=1
    g315: Circle CenterX=-1.92719 CenterY=-91.7794 CenterZ=0 NormalX=0 NormalY=0 NormalZ=1 AngleXU=0 Radius=1
    g316: Circle CenterX=1.57905 CenterY=-89.8542 CenterZ=0 NormalX=0 NormalY=0 NormalZ=1 AngleXU=0 Radius=1
    g317: BSplineCurve PolesCount=3 KnotsCount=2 Degree=2 IsPeriodic=0
    g318: GeomPoint X=2.07281 Y=-91.7794 Z=0
    g319: GeomPoint X=1.57905 Y=-89.8542 Z=0
    g320: LineSegment StartX=2.07281 StartY=-91.7794 StartZ=0 EndX=42.0728 EndY=-91.7794 EndZ=0
    g321: LineSegment StartX=46.0728 StartY=-87.7794 StartZ=0 EndX=46.0728 EndY=-69.424 EndZ=0
    g322: LineSegment StartX=42.5666 StartY=-67.3492 StartZ=0 EndX=1.57905 EndY=-89.8542 EndZ=0
    g323: Circle CenterX=322.073 CenterY=76.4095 CenterZ=0 NormalX=0 NormalY=0 NormalZ=1 AngleXU=0 Radius=4
    g324: BSplineCurve PolesCount=3 KnotsCount=2 Degree=2 IsPeriodic=0
    g325: GeomPoint X=318.073 Y=72.4095 Z=0
    g326: GeomPoint X=322.073 Y=76.4095 Z=0
    g327: Circle CenterX=375.073 CenterY=72.4095 CenterZ=0 NormalX=0 NormalY=0 NormalZ=1 AngleXU=0 Radius=1
    g328: Circle CenterX=375.073 CenterY=76.4095 CenterZ=0 NormalX=0 NormalY=0 NormalZ=1 AngleXU=0 Radius=1
    g329: Circle CenterX=371.073 CenterY=76.4095 CenterZ=0 NormalX=0 NormalY=0 NormalZ=1 AngleXU=0 Radius=1
    g330: BSplineCurve PolesCount=3 KnotsCount=2 Degree=2 IsPeriodic=0
    g331: GeomPoint X=375.073 Y=72.4095 Z=0
    g332: GeomPoint X=371.073 Y=76.4095 Z=0
    g333: LineSegment StartX=322.073 StartY=76.4095 StartZ=0 EndX=371.073 EndY=76.4095 EndZ=0
    g334: LineSegment StartX=318.073 StartY=72.4095 StartZ=0 EndX=318.073 EndY=-47.4805 EndZ=0
    g335: LineSegment StartX=375.073 StartY=72.4095 StartZ=0 EndX=375.073 EndY=-78.7896 EndZ=0
    g336: ArcOfCircle CenterX=-26.9272 CenterY=22.1087 CenterZ=0 NormalX=0 NormalY=0 NormalZ=1 AngleXU=0 Radius=4 StartAngle=5e-16 EndAngle=3.14159
    g337: LineSegment StartX=-22.9272 StartY=22.1087 StartZ=0 EndX=-18.9272 EndY=-83.7794 EndZ=0
    g338: LineSegment StartX=-34.9272 StartY=-83.7794 StartZ=0 EndX=-30.9272 EndY=22.1087 EndZ=0
    g339: ArcOfCircle CenterX=391.073 CenterY=22.1087 CenterZ=0 NormalX=0 NormalY=0 NormalZ=1 AngleXU=0 Radius=4 StartAngle=0 EndAngle=3.14159
    g340: LineSegment StartX=387.073 StartY=22.1087 StartZ=0 EndX=383.073 EndY=-83.7794 EndZ=0
    g341: LineSegment StartX=395.073 StartY=22.1087 StartZ=0 EndX=399.073 EndY=-83.7794 EndZ=0
    g342: Circle CenterX=-10.9272 CenterY=-78.7794 CenterZ=0 NormalX=0 NormalY=0 NormalZ=1 AngleXU=0 Radius=1
    g343: Circle CenterX=-10.9272 CenterY=-82.7794 CenterZ=0 NormalX=0 NormalY=0 NormalZ=1 AngleXU=0 Radius=1
    g344: Circle CenterX=-7.42095 CenterY=-80.8542 CenterZ=0 NormalX=0 NormalY=0 NormalZ=1 AngleXU=0 Radius=1
    g345: BSplineCurve PolesCount=3 KnotsCount=2 Degree=2 IsPeriodic=0
    g346: GeomPoint X=-10.9272 Y=-78.7794 Z=0
    g347: GeomPoint X=-7.42095 Y=-80.8542 Z=0
    g348: Circle CenterX=42.5666 CenterY=-53.4075 CenterZ=0 NormalX=0 NormalY=0 NormalZ=1 AngleXU=0 Radius=1
    g349: Circle CenterX=46.0728 CenterY=-51.4823 CenterZ=0 NormalX=0 NormalY=0 NormalZ=1 AngleXU=0 Radius=1
    g350: Circle CenterX=46.0728 CenterY=-47.4823 CenterZ=0 NormalX=0 NormalY=0 NormalZ=1 AngleXU=0 Radius=1
    g351: BSplineCurve PolesCount=3 KnotsCount=2 Degree=2 IsPeriodic=0
    g352: GeomPoint X=42.5666 Y=-53.4075 Z=0
    g353: GeomPoint X=46.0728 Y=-47.4823 Z=0
    g354: Circle CenterX=46.0728 CenterY=72.4095 CenterZ=0 NormalX=0 NormalY=0 NormalZ=1 AngleXU=0 Radius=1
    g355: Circle CenterX=46.0728 CenterY=76.4095 CenterZ=0 NormalX=0 NormalY=0 NormalZ=1 AngleXU=0 Radius=1
    g356: Circle CenterX=42.0728 CenterY=76.4095 CenterZ=0 NormalX=0 NormalY=0 NormalZ=1 AngleXU=0 Radius=1
    g357: BSplineCurve PolesCount=3 KnotsCount=2 Degree=2 IsPeriodic=0
    g358: GeomPoint X=46.0728 Y=72.4095 Z=0
    g359: GeomPoint X=42.0728 Y=76.4095 Z=0
    g360: Circle CenterX=-6.92719 CenterY=76.4095 CenterZ=0 NormalX=0 NormalY=0 NormalZ=1 AngleXU=0 Radius=1
    g361: Circle CenterX=-10.9272 CenterY=76.4095 CenterZ=0 NormalX=0 NormalY=0 NormalZ=1 AngleXU=0 Radius=1
    g362: Circle CenterX=-10.9272 CenterY=72.4095 CenterZ=0 NormalX=0 NormalY=0 NormalZ=1 AngleXU=0 Radius=1
    g363: BSplineCurve PolesCount=3 KnotsCount=2 Degree=2 IsPeriodic=0
    g364: GeomPoint X=-6.92719 Y=76.4095 Z=0
    g365: GeomPoint X=-10.9272 Y=72.4095 Z=0
    g366: LineSegment StartX=-10.9272 StartY=72.4095 StartZ=0 EndX=-10.9272 EndY=-78.7794 EndZ=0
    g367: LineSegment StartX=-7.42095 StartY=-80.8542 StartZ=0 EndX=42.5666 EndY=-53.4075 EndZ=0
    g368: LineSegment StartX=46.0728 StartY=-47.4823 StartZ=0 EndX=46.0728 EndY=72.4095 EndZ=0
    g369: LineSegment StartX=42.0728 StartY=76.4095 StartZ=0 EndX=-6.92719 EndY=76.4095 EndZ=0
    g370: LineSegment StartX=-42.9272 StartY=136.221 StartZ=0 EndX=407.073 EndY=136.221 EndZ=0
    g371: LineSegment StartX=232.072 StartY=136.221 StartZ=0 EndX=220.072 EndY=136.221 EndZ=0
    g372: LineSegment StartX=232.072 StartY=136.221 StartZ=0 EndX=232.072 EndY=124.221 EndZ=0
    g373: LineSegment StartX=220.072 StartY=136.221 StartZ=0 EndX=220.072 EndY=124.221 EndZ=0
    g374: LineSegment StartX=220.072 StartY=136.221 StartZ=0 EndX=226.072 EndY=136.221 EndZ=0
    g375: LineSegment StartX=220.072 StartY=136.221 StartZ=0 EndX=220.072 EndY=130.221 EndZ=0
    g376: LineSegment StartX=220.072 StartY=124.221 StartZ=0 EndX=226.072 EndY=124.221 EndZ=0
    g377: LineSegment StartX=232.072 StartY=124.221 StartZ=0 EndX=232.072 EndY=127.221 EndZ=0
    g378: LineSegment StartX=232.072 StartY=136.221 StartZ=0 EndX=232.072 EndY=133.221 EndZ=0
    g379-g383: Circle x5 (B-spline internal-alignment scaffolding for g384; pole/knot coordinates omitted)
    g384: BSplineCurve PolesCount=5 KnotsCount=3 Degree=3 IsPeriodic=0
    g385: GeomPoint X=232.072 Y=133.221 Z=0
    g386: GeomPoint X=223.072 Y=130.221 Z=0
    g387: GeomPoint X=232.072 Y=127.221 Z=0
    g388: LineSegment StartX=189.124 StartY=124.221 StartZ=0 EndX=302.073 EndY=124.221 EndZ=0
    g389: LineSegment StartX=132.072 StartY=136.221 StartZ=0 EndX=132.072 EndY=124.221 EndZ=0
    g390: LineSegment StartX=132.072 StartY=136.221 StartZ=0 EndX=144.072 EndY=136.221 EndZ=0
    g391: LineSegment StartX=144.072 StartY=136.221 StartZ=0 EndX=144.072 EndY=124.221 EndZ=0
    g392: LineSegment StartX=144.072 StartY=136.221 StartZ=0 EndX=138.072 EndY=136.221 EndZ=0
    g393: LineSegment StartX=144.072 StartY=136.221 StartZ=0 EndX=144.072 EndY=130.221 EndZ=0
    g394: LineSegment StartX=132.072 StartY=136.221 StartZ=0 EndX=132.072 EndY=133.221 EndZ=0
    g395: LineSegment StartX=132.072 StartY=133.221 StartZ=0 EndX=132.072 EndY=127.221 EndZ=0
    g396-g400: Circle x5 (B-spline internal-alignment scaffolding for g401; pole/knot coordinates omitted)
    g401: BSplineCurve PolesCount=5 KnotsCount=3 Degree=3 IsPeriodic=0
    g402: GeomPoint X=132.072 Y=133.221 Z=0
    g403: GeomPoint X=141.072 Y=130.221 Z=0
    g404: GeomPoint X=132.072 Y=127.221 Z=0
    g405: LineSegment StartX=132.072 StartY=124.221 StartZ=0 EndX=175.022 EndY=124.221 EndZ=0
    g406: LineSegment StartX=62.0728 StartY=124.221 StartZ=0 EndX=132.072 EndY=124.221 EndZ=0
    g407: LineSegment StartX=132.072 StartY=136.221 StartZ=0 EndX=131.457 EndY=138.832 EndZ=0
    ... +61 more geometry lines
  constraints (808):
    c: Vertical(g0)
    c: Vertical(g1)
    c: Block(g1)
    c: Block(g0)
    c: Weight(g4) = 1
    c: Equal(g4,g5)
    c: Equal(g4,g6)
    c: InternalAlignment(g4,g7)
    c: InternalAlignment(g5,g7)
    c: InternalAlignment(g6,g7)
    c: InternalAlignment(g8,g7)
    c: InternalAlignment(g9,g7)
    c: Weight(g10) = 1
    c: Equal(g10,g11)
    c: Equal(g10,g12)
    c: InternalAlignment(g10,g13)
    c: InternalAlignment(g11,g13)
    c: InternalAlignment(g12,g13)
    c: InternalAlignment(g14,g13)
    c: InternalAlignment(g15,g13)
    c: Block(g13)
    c: Block(g7)
    c: Weight(g16) = 1
    c: Equal(g16,g17)
    c: Equal(g16,g18)
    c: InternalAlignment(g16,g19)
    c: InternalAlignment(g17,g19)
    c: InternalAlignment(g18,g19)
    c: InternalAlignment(g20,g19)
    c: InternalAlignment(g21,g19)
    c: Weight(g22) = 1
    c: Equal(g22,g23)
    c: Equal(g22,g24)
    c: InternalAlignment(g22,g25)
    c: InternalAlignment(g23,g25)
    c: InternalAlignment(g24,g25)
    c: InternalAlignment(g26,g25)
    c: InternalAlignment(g27,g25)
    c: Block(g25)
    c: Block(g19)
    c: Weight(g28) = 1
    c: Equal(g28,g29)
    c: Equal(g28,g30)
    c: InternalAlignment(g28,g31)
    c: InternalAlignment(g29,g31)
    c: InternalAlignment(g30,g31)
    c: InternalAlignment(g32,g31)
    c: InternalAlignment(g33,g31)
    c: Weight(g34) = 1
    c: Equal(g34,g35)
    c: Equal(g34,g36)
    c: InternalAlignment(g34,g37)
    c: InternalAlignment(g35,g37)
    c: InternalAlignment(g36,g37)
    c: InternalAlignment(g38,g37)
    c: InternalAlignment(g39,g37)
    c: Block(g31)
    c: Block(g37)
    c: Coincident(g40,g1)
    c: Coincident(g40,g0)
    c: Horizontal(g40)
    c: Distance(g40) = 450
    c: Weight(g41) = 1
    c: Equal(g41,g42)
    c: Equal(g41,g43)
    c: InternalAlignment(g41,g44)
    c: InternalAlignment(g42,g44)
    c: InternalAlignment(g43,g44)
    c: InternalAlignment(g45,g44)
    c: InternalAlignment(g46,g44)
    c: Block(g44)
    c: Weight(g47) = 1
    c: Equal(g47,g48)
    c: Equal(g47,g49)
    c: InternalAlignment(g47,g50)
    c: InternalAlignment(g48,g50)
    c: InternalAlignment(g49,g50)
    c: InternalAlignment(g51,g50)
    c: InternalAlignment(g52,g50)
    c: Block(g50)
    c: Weight(g53) = 1
    c: Equal(g53,g54)
    c: Equal(g53,g55)
    c: InternalAlignment(g53,g56)
    c: InternalAlignment(g54,g56)
    c: InternalAlignment(g55,g56)
    c: InternalAlignment(g57,g56)
    c: InternalAlignment(g58,g56)
    c: Block(g56)
    c: Weight(g59) = 1
    c: Equal(g59,g60)
    c: Equal(g59,g61)
    c: InternalAlignment(g59,g62)
    c: InternalAlignment(g60,g62)
    c: InternalAlignment(g61,g62)
    c: InternalAlignment(g63,g62)
    c: InternalAlignment(g64,g62)
    c: Block(g62)
    c: Weight(g65) = 1
    c: Equal(g65,g66)
    c: Equal(g65,g67)
    c: InternalAlignment(g65,g68)
    c: InternalAlignment(g66,g68)
    c: InternalAlignment(g67,g68)
    c: InternalAlignment(g69,g68)
    c: InternalAlignment(g70,g68)
    c: Weight(g71) = 1
    c: Equal(g71,g72)
    c: Equal(g71,g73)
    c: InternalAlignment(g71,g74)
    c: InternalAlignment(g72,g74)
    c: InternalAlignment(g73,g74)
    c: InternalAlignment(g75,g74)
    c: InternalAlignment(g76,g74)
    c: Block(g68)
    c: Block(g74)
    c: Coincident(g77,g68)
    c: Coincident(g77,g74)
    c: Vertical(g77)
    c: Coincident(g78,g68)
    c: Coincident(g78,g50)
    c: Coincident(g79,g50)
    c: Coincident(g79,g74)
    c: Weight(g80) = 1
    c: Equal(g80,g81)
    c: Equal(g80,g82)
    c: InternalAlignment(g80,g83)
    c: InternalAlignment(g81,g83)
    c: InternalAlignment(g82,g83)
    c: InternalAlignment(g84,g83)
    c: InternalAlignment(g85,g83)
    c: Weight(g86) = 1
    c: Equal(g86,g87)
    c: Equal(g86,g88)
    c: InternalAlignment(g86,g89)
    c: InternalAlignment(g87,g89)
    c: InternalAlignment(g88,g89)
    c: InternalAlignment(g90,g89)
    c: InternalAlignment(g91,g89)
    c: Block(g83)
    c: Block(g89)
    c: Coincident(g92,g83)
    c: Coincident(g92,g89)
    c: Vertical(g92)
    c: Coincident(g93,g83)
    c: Coincident(g93,g44)
    c: Coincident(g94,g44)
    c: Coincident(g94,g89)
    c: Weight(g95) = 1
    c: Equal(g95,g96)
    c: Equal(g95,g97)
    c: InternalAlignment(g95,g98)
    c: InternalAlignment(g96,g98)
    c: InternalAlignment(g97,g98)
    c: InternalAlignment(g99,g98)
    c: InternalAlignment(g100,g98)
    c: Weight(g101) = 1
    c: Equal(g101,g102)
    c: Equal(g101,g103)
    c: InternalAlignment(g101,g104)
    c: InternalAlignment(g102,g104)
    c: InternalAlignment(g103,g104)
    c: InternalAlignment(g105,g104)
    c: InternalAlignment(g106,g104)
    c: Block(g98)
    c: Block(g104)
    c: Coincident(g107,g98)
    c: Coincident(g107,g104)
    c: Vertical(g107)
    c: Coincident(g108,g104)
    c: Coincident(g108,g62)
    c: Coincident(g109,g62)
    c: Coincident(g109,g98)
    c: Weight(g110) = 1
    c: Equal(g110,g111)
    c: Equal(g110,g112)
    c: InternalAlignment(g110,g113)
    c: InternalAlignment(g111,g113)
    c: InternalAlignment(g112,g113)
    c: InternalAlignment(g114,g113)
    c: InternalAlignment(g115,g113)
    c: Weight(g116) = 1
    c: Equal(g116,g117)
    c: Equal(g116,g118)
    c: InternalAlignment(g116,g119)
    c: InternalAlignment(g117,g119)
    c: InternalAlignment(g118,g119)
    c: InternalAlignment(g120,g119)
    c: InternalAlignment(g121,g119)
    c: Block(g113)
    c: Block(g119)
    c: Coincident(g122,g113)
    c: Coincident(g122,g119)
    c: Vertical(g122)
    c: Coincident(g123,g119)
    c: Coincident(g123,g56)
    c: Coincident(g124,g56)
    c: Coincident(g124,g113)
    c: Weight(g125) = 1
    c: Equal(g125,g126)
    c: Equal(g125,g127)
    c: InternalAlignment(g125,g128)
    c: InternalAlignment(g126,g128)
    c: InternalAlignment(g127,g128)
    c: InternalAlignment(g129,g128)
    c: InternalAlignment(g130,g128)
    c: Weight(g131) = 1
    c: Equal(g131,g132)
    c: Equal(g131,g133)
    c: InternalAlignment(g131,g134)
    c: InternalAlignment(g132,g134)
    c: InternalAlignment(g133,g134)
    c: InternalAlignment(g135,g134)
    c: InternalAlignment(g136,g134)
    c: Weight(g137) = 1
    c: Equal(g137,g138)
    c: Equal(g137,g139)
    c: InternalAlignment(g137,g140)
    c: InternalAlignment(g138,g140)
    c: InternalAlignment(g139,g140)
    c: InternalAlignment(g141,g140)
    c: InternalAlignment(g142,g140)
    c: Weight(g143) = 1
    c: Equal(g143,g144)
    c: Equal(g143,g145)
    c: InternalAlignment(g143,g146)
    c: InternalAlignment(g144,g146)
    c: InternalAlignment(g145,g146)
    c: InternalAlignment(g147,g146)
    c: InternalAlignment(g148,g146)
    c: Block(g146)
    c: Block(g140)
    c: Block(g134)
    c: Block(g128)
    c: Coincident(g149,g25)
    c: Coincident(g149,g146)
    c: Coincident(g150,g146)
    c: Coincident(g150,g140)
    c: Horizontal(g150)
    c: Coincident(g151,g140)
    c: Coincident(g151,g25)
    c: Vertical(g151)
    c: Coincident(g152,g19)
    c: Coincident(g152,g134)
    c: Vertical(g152)
    c: Coincident(g153,g134)
    c: Coincident(g153,g128)
    c: Horizontal(g153)
    c: Coincident(g154,g128)
    c: Coincident(g154,g19)
    c: Weight(g155) = 1
    c: Equal(g155,g156)
    c: Equal(g155,g157)
    c: InternalAlignment(g155,g158)
    c: InternalAlignment(g156,g158)
    c: InternalAlignment(g157,g158)
    c: InternalAlignment(g159,g158)
    c: InternalAlignment(g160,g158)
    c: Weight(g161) = 1
    c: Equal(g161,g162)
    c: Equal(g161,g163)
    c: InternalAlignment(g161,g164)
    c: InternalAlignment(g162,g164)
    c: InternalAlignment(g163,g164)
    c: InternalAlignment(g165,g164)
    c: InternalAlignment(g166,g164)
    c: Weight(g167) = 1
    c: Equal(g167,g168)
    c: Equal(g167,g169)
    c: InternalAlignment(g167,g170)
    c: InternalAlignment(g168,g170)
    c: InternalAlignment(g169,g170)
    c: InternalAlignment(g171,g170)
    c: InternalAlignment(g172,g170)
    c: Weight(g173) = 1
    c: Equal(g173,g174)
    c: Equal(g173,g175)
    c: InternalAlignment(g173,g176)
    c: InternalAlignment(g174,g176)
    c: InternalAlignment(g175,g176)
    c: InternalAlignment(g177,g176)
    c: InternalAlignment(g178,g176)
    c: Block(g176)
    c: Block(g170)
    c: Block(g164)
    c: Block(g158)
    c: Coincident(g179,g170)
    c: Coincident(g179,g7)
    c: Vertical(g179)
    c: Coincident(g180,g13)
    c: Coincident(g180,g164)
    c: Vertical(g180)
    c: Coincident(g181,g158)
    c: Coincident(g181,g13)
    c: Coincident(g182,g7)
    c: Weight(g183) = 1
    c: Equal(g183,g184)
    c: Equal(g183,g185)
    c: InternalAlignment(g183,g186)
    c: InternalAlignment(g184,g186)
    c: InternalAlignment(g185,g186)
    c: InternalAlignment(g187,g186)
    c: InternalAlignment(g188,g186)
    c: Weight(g189) = 1
    c: Equal(g189,g190)
    c: Equal(g189,g191)
    c: InternalAlignment(g189,g192)
    c: InternalAlignment(g190,g192)
    c: InternalAlignment(g191,g192)
    c: InternalAlignment(g193,g192)
    c: InternalAlignment(g194,g192)
    c: Block(g192)
    c: Block(g186)
    c: Coincident(g195,g192)
    c: Coincident(g195,g31)
    c: Coincident(g196,g31)
    c: Coincident(g196,g186)
    c: Coincident(g197,g186)
    c: Coincident(g197,g192)
    c: Vertical(g197)
    c: Weight(g198) = 1
    c: Equal(g198,g199)
    c: Equal(g198,g200)
    c: InternalAlignment(g198,g201)
    c: InternalAlignment(g199,g201)
    c: InternalAlignment(g200,g201)
    c: InternalAlignment(g202,g201)
    c: InternalAlignment(g203,g201)
    c: Weight(g204) = 1
    c: Equal(g204,g205)
    c: Equal(g204,g206)
    c: InternalAlignment(g204,g207)
    c: InternalAlignment(g205,g207)
    c: InternalAlignment(g206,g207)
    c: InternalAlignment(g208,g207)
    c: InternalAlignment(g209,g207)
    c: Block(g207)
    c: Block(g201)
    c: Coincident(g210,g201)
    c: Coincident(g210,g37)
    c: Coincident(g211,g37)
    c: Coincident(g211,g207)
    c: Coincident(g212,g207)
    c: Coincident(g212,g201)
    c: Vertical(g212)
    c: Horizontal(g213)
    c: Block(g213)
    c: Vertical(g214)
    c: Block(g214)
    c: Block(g215)
    c: Weight(g216) = 1
    c: Equal(g216,g217)
    c: Equal(g216,g218)
    c: InternalAlignment(g216,g219)
    c: InternalAlignment(g217,g219)
    c: InternalAlignment(g218,g219)
    c: InternalAlignment(g220,g219)
    c: InternalAlignment(g221,g219)
    c: Weight(g222) = 1
    c: Equal(g222,g223)
    c: Equal(g222,g224)
    c: InternalAlignment(g222,g225)
    c: InternalAlignment(g223,g225)
    c: InternalAlignment(g224,g225)
    c: InternalAlignment(g226,g225)
    c: InternalAlignment(g227,g225)
    c: Weight(g228) = 1
    c: Equal(g228,g229)
    c: Equal(g228,g230)
    c: InternalAlignment(g228,g231)
    c: InternalAlignment(g229,g231)
    c: InternalAlignment(g230,g231)
    c: InternalAlignment(g232,g231)
    c: InternalAlignment(g233,g231)
    c: Weight(g234) = 1
    c: Equal(g234,g235)
    c: Equal(g234,g236)
    c: InternalAlignment(g234,g237)
    c: InternalAlignment(g235,g237)
    c: InternalAlignment(g236,g237)
    c: InternalAlignment(g238,g237)
    c: InternalAlignment(g239,g237)
    c: Block(g219)
    c: Block(g225)
    c: Block(g231)
    c: Block(g237)
    c: Coincident(g240,g225)
    c: Coincident(g240,g219)
    c: Horizontal(g240)
    c: Block(g182)
    c: Weight(g241) = 1
    c: Equal(g241,g242)
    c: Equal(g241,g243)
    c: InternalAlignment(g241,g244)
    c: InternalAlignment(g242,g244)
    c: InternalAlignment(g243,g244)
    c: InternalAlignment(g245,g244)
    c: InternalAlignment(g246,g244)
    c: Weight(g247) = 1
    c: Equal(g247,g248)
    c: Equal(g247,g249)
    c: InternalAlignment(g247,g250)
    c: InternalAlignment(g248,g250)
    c: InternalAlignment(g249,g250)
    c: InternalAlignment(g251,g250)
    c: InternalAlignment(g252,g250)
    c: Block(g244)
    c: Block(g250)
    c: Coincident(g253,g244)
    c: Coincident(g253,g250)
    c: Weight(g254) = 1
    c: Equal(g254,g255)
    c: Equal(g254,g256)
    c: InternalAlignment(g254,g257)
    c: InternalAlignment(g255,g257)
    c: InternalAlignment(g256,g257)
    c: InternalAlignment(g258,g257)
    c: InternalAlignment(g259,g257)
    c: Weight(g260) = 1
    c: Equal(g260,g261)
    c: Equal(g260,g262)
    c: InternalAlignment(g260,g263)
    c: InternalAlignment(g261,g263)
    c: InternalAlignment(g262,g263)
    c: InternalAlignment(g264,g263)
    c: InternalAlignment(g265,g263)
    c: Weight(g266) = 1
    c: Equal(g266,g267)
    c: Equal(g266,g268)
    c: InternalAlignment(g266,g269)
    c: InternalAlignment(g267,g269)
    c: InternalAlignment(g268,g269)
    c: InternalAlignment(g270,g269)
    c: InternalAlignment(g271,g269)
    c: Block(g269)
    c: Block(g263)
    c: Block(g257)
    c: Coincident(g272,g263)
    c: Coincident(g272,g257)
    c: Coincident(g273,g257)
    c: Coincident(g273,g269)
    c: Vertical(g273)
    c: Coincident(g274,g269)
    c: Coincident(g274,g263)
    c: Horizontal(g274)
    c: Weight(g275) = 1
    c: Equal(g275,g276)
    c: InternalAlignment(g275,g277)
    c: InternalAlignment(g276,g277)
    c: InternalAlignment(g278,g277)
    c: InternalAlignment(g279,g277)
    c: Weight(g280) = 1
    c: InternalAlignment(g281,g283)
    c: InternalAlignment(g282,g283)
    c: InternalAlignment(g284,g283)
    c: InternalAlignment(g285,g283)
    c: Weight(g286) = 1
    c: Equal(g286,g287)
    c: Equal(g286,g288)
    c: InternalAlignment(g286,g289)
    c: InternalAlignment(g287,g289)
    c: InternalAlignment(g288,g289)
    c: InternalAlignment(g290,g289)
    c: InternalAlignment(g291,g289)
    c: Equal(g292,g293)
    c: Equal(g292,g294)
    c: InternalAlignment(g292,g295)
    c: InternalAlignment(g293,g295)
    c: InternalAlignment(g294,g295)
    c: InternalAlignment(g296,g295)
    c: InternalAlignment(g297,g295)
    c: Block(g283)
    c: Block(g289)
    c: Block(g295)
    c: Block(g277)
    c: Coincident(g298,g277)
    c: Coincident(g298,g283)
    c: Horizontal(g298)
    c: Coincident(g299,g283)
    c: Coincident(g299,g289)
    c: Vertical(g299)
    c: Coincident(g300,g289)
    c: Coincident(g300,g295)
    c: Horizontal(g300)
    c: Coincident(g301,g295)
    c: Coincident(g301,g277)
    c: Weight(g302) = 1
    c: Equal(g302,g303)
    c: Equal(g302,g304)
    c: InternalAlignment(g302,g305)
    c: InternalAlignment(g303,g305)
    c: InternalAlignment(g304,g305)
    c: InternalAlignment(g306,g305)
    c: InternalAlignment(g307,g305)
    c: Weight(g308) = 1
    c: Equal(g308,g309)
    c: Equal(g308,g310)
    c: InternalAlignment(g308,g311)
    c: InternalAlignment(g309,g311)
    c: InternalAlignment(g310,g311)
    c: InternalAlignment(g312,g311)
    c: Weight(g314) = 1
    c: Equal(g314,g315)
    c: Equal(g314,g316)
    c: InternalAlignment(g314,g317)
    c: InternalAlignment(g315,g317)
    c: InternalAlignment(g316,g317)
    c: InternalAlignment(g318,g317)
    c: InternalAlignment(g319,g317)
    c: Block(g317)
    c: Block(g311)
    c: Block(g305)
    c: Coincident(g320,g317)
    c: Coincident(g320,g311)
    c: Horizontal(g320)
    c: Coincident(g321,g311)
    c: Coincident(g321,g305)
    c: Vertical(g321)
    c: Coincident(g322,g305)
    c: Coincident(g322,g317)
    c: InternalAlignment(g323,g324)
    c: InternalAlignment(g325,g324)
    c: InternalAlignment(g326,g324)
    c: Block(g324)
    c: Equal(g327,g328)
    c: Equal(g327,g329)
    c: InternalAlignment(g327,g330)
    c: InternalAlignment(g328,g330)
    c: InternalAlignment(g329,g330)
    c: InternalAlignment(g331,g330)
    c: InternalAlignment(g332,g330)
    c: Block(g330)
    c: Coincident(g333,g324)
    c: Horizontal(g333)
    c: Block(g333)
    c: Coincident(g334,g324)
    c: Coincident(g334,g250)
    c: Vertical(g334)
    c: Coincident(g335,g330)
    c: Coincident(g335,g244)
    c: Vertical(g335)
    c: Block(g336)
    c: Block(g2)
    c: Distance(g334) = 119.89
    c: Coincident(g337,g336)
    c: Coincident(g337,g2)
    c: Coincident(g338,g2)
    c: Coincident(g338,g336)
    c: Block(g3)
    c: Block(g339)
    c: Coincident(g340,g339)
    c: Coincident(g340,g3)
    c: Coincident(g341,g339)
    c: Coincident(g341,g3)
    c: Block(g341)
    c: Block(g340)
    c: Weight(g342) = 1
    c: Equal(g342,g344)
    c: InternalAlignment(g342,g345)
    c: InternalAlignment(g343,g345)
    c: InternalAlignment(g344,g345)
    c: InternalAlignment(g346,g345)
    c: InternalAlignment(g347,g345)
    c: InternalAlignment(g352,g351)
    c: InternalAlignment(g353,g351)
    c: InternalAlignment(g355,g357)
    c: Horizontal(g369)
    c: Coincident(g370,g0)
    c: Horizontal(g370)
    c: Block(g370)
    c: Distance(g370) = 450
    c: Horizontal(g371)
    c: Distance(g371) = 12
    c: Coincident(g373,g371)
    c: Vertical(g373)
    c: Horizontal(g374)
    c: Vertical(g375)
    c: Distance(g375) = 6
    c: Coincident(g375,g371)
    c: Coincident(g374,g371)
    c: Block(g373)
    c: Coincident(g376,g373)
    c: Horizontal(g376)
    c: Distance(g376) = 6
    c: Vertical(g377)
    c: Distance(g377) = 3
    c: Vertical(g378)
    c: Distance(g378) = 3
    c: Coincident(g372,g377)
    c: Coincident(g384,g378)
    c: Weight(g379) = 1
    c: Equal(g379,g380)
    c: Coincident(g380,g374)
    c: Equal(g379,g381)
    c: Coincident(g381,g375)
    c: Equal(g379,g382)
    c: Coincident(g382,g376)
    c: Equal(g379,g383)
    c: Coincident(g384,g377)
    c: InternalAlignment(g379-g383 -> g384) x5
    c: InternalAlignment(g385,g384)
    c: InternalAlignment(g386,g384)
    c: InternalAlignment(g387,g384)
    c: Coincident(g388,g164)
    c: Coincident(g388,g158)
    c: Coincident(g392,g390)
    c: Vertical(g393)
    c: Distance(g393) = 6
    c: Coincident(g393,g390)
    c: Vertical(g394)
    c: Distance(g394) = 3
    c: Vertical(g395)
    c: Distance(g395) = 6
    c: Coincident(g395,g394)
    c: Coincident(g401,g394)
    c: Weight(g396) = 1
    c: Equal(g396,g397)
    c: Coincident(g397,g392)
    c: Equal(g396,g398)
    c: Coincident(g398,g393)
    c: Equal(g396,g399)
    c: Equal(g396,g400)
    c: Coincident(g401,g395)
    c: InternalAlignment(g396-g400 -> g401) x5
    c: InternalAlignment(g402,g401)
    c: InternalAlignment(g403,g401)
    c: InternalAlignment(g404,g401)
    c: Coincident(g405,g389)
    c: Coincident(g405,g170)
    c: Horizontal(g405)
    c: Block(g401)
    c: Coincident(g406,g176)
    c: Coincident(g406,g389)
    c: Horizontal(g406)
    c: Block(g405)
    c: Coincident(g408,g389)
    c: PointOnObject(g408,g153)
    c: Vertical(g408)
    c: Block(g409)
    c: Coincident(g410,g409)
    c: Vertical(g410)
    c: PointOnObject(g410,g40)
    c: Block(g410)
    c: Coincident(g411,g409)
    c: Vertical(g411)
    c: Block(g411)
    c: Vertical(g412)
    c: Distance(g412) = 3
    c: Equal(g379,g415) = 1
    c: Equal(g415,g416)
    c: InternalAlignment(g415,g417)
    c: InternalAlignment(g416,g417)
    c: InternalAlignment(g413,g417)
    c: InternalAlignment(g414,g417)
    c: InternalAlignment(g418,g417)
    c: Block(g417)
    c: Coincident(g418,g412)
    c: Coincident(g419,g417)
    c: PointOnObject(g419,g150)
    c: Vertical(g419)
    c: Distance(g420) = 3
    c: Block(g420)
    c: Distance(g421) = 3
    c: Parallel(g421,g420)
    c: Coincident(g421,g420)
    c: Coincident(g422,g420)
    c: Perpendicular(g422,g420)
    c: Distance(g422) = 3
    c: Coincident(g423,g421)
    c: Perpendicular(g423,g421)
    c: Distance(g423) = 3
    c: Coincident(g424,g420)
    c: Perpendicular(g424,g421)
    c: Distance(g424) = 6
    c: Coincident(g425,g424)
    c: PointOnObject(g423,g425)
    c: Coincident(g426,g420)
    c: PointOnObject(g426,g79)
    c: Block(g426)
    c: Distance(g427) = 2.76
    c: Coincident(g428,g427)
    c: Parallel(g427,g428)
    c: PointOnObject(g428,g181)
    c: Distance(g428) = 2.41
    c: Block(g428)
    c: Coincident(g429,g427)
    c: Distance(g429) = 6.6
    c: Perpendicular(g429,g428)
    c: Distance(g430) = 6.6
    c: Coincident(g431,g429)
    c: Coincident(g431,g430)
    c: Block(g432)
    c: Coincident(g433,g432)
    c: Vertical(g433)
    c: Distance(g433) = 3.6
    c: Coincident(g434,g427)
    c: Parallel(g427,g434)
    c: PointOnObject(g434,g78)
    c: Block(g434)
    c: Coincident(g435,g421)
    c: Parallel(g435,g421)
    c: PointOnObject(g435,g211)
    c: Block(g435)
    c: Coincident(g436,g435)
    c: Vertical(g436)
    c: PointOnObject(g436,g210)
    c: Coincident(g437,g436)
    c: Perpendicular(g437,g210)
    c: Distance(g437) = 3
    c: Coincident(g438,g437)
    c: Block(g437)
    c: Distance(g438) = 3
    c: Parallel(g437,g438)
    c: Coincident(g439,g438)
    c: Distance(g439) = 3
    c: Parallel(g438,g439)
    c: Coincident(g440,g439)
    c: Parallel(g440,g437)
    c: PointOnObject(g440,g124)
    c: PointOnObject(g441,g53)
    c: Tangent(g440,g441)
    c: Coincident(g442,g439)
    c: Perpendicular(g442,g439)
    c: Coincident(g443,g437)
    c: Parallel(g443,g442)
    c: Distance(g443) = 3
    c: Distance(g442) = 3
    c: PointOnObject(g442,g444)
    c: Block(g444)
    c: PointOnObject(g445,g123)
    c: Perpendicular(g123,g445)
    c: Distance(g445) = 2.41
    c: Block(g445)
    c: Coincident(g446,g445)
    c: Perpendicular(g123,g446)
    c: Distance(g446) = 2.76
    c: Coincident(g447,g446)
    c: Perpendicular(g123,g447)
    c: PointOnObject(g447,g149)
    c: Coincident(g448,g445)
    c: Parallel(g123,g448)
    c: Distance(g448) = 6.6
    c: Coincident(g449,g446)
    c: Parallel(g123,g449)
    c: Coincident(g450,g448)
    c: Distance(g449) = 6.6
    c: Coincident(g449,g450)
    c: Block(g149)
    c: Block(g124)
    c: Block(g211)
    c: Block(g181)
    c: Block(g78)
    c: Block(g79)
    c: Block(g430)
    c: Coincident(g451,g447)
    c: Distance(g451) = 46
    c: Parallel(g149,g451)
    c: Coincident(g452,g451)
    c: Horizontal(g452)
    c: PointOnObject(g452,g154)
    c: Coincident(g453,g451)
    c: Vertical(g453)
    c: Distance(g453) = 9
    c: Block(g452)
    c: PointOnObject(g454,g93)
    c: Distance(g455) = 6.6
    c: Distance(g456) = 6.6
    c: Block(g454)
    c: Coincident(g457,g456)
    c: Coincident(g457,g455)
    c: Perpendicular(g457,g182)
    c: Coincident(g458,g455)
    c: Perpendicular(g458,g182)
    c: PointOnObject(g458,g182)
    c: Block(g458)
    c: Block(g457)
    c: Block(g456)
    c: PointOnObject(g459,g196)
    c: Perpendicular(g196,g459)
    c: Distance(g459) = 3
    c: Coincident(g460,g459)
    c: Perpendicular(g196,g460)
    c: Distance(g460) = 3
    c: Coincident(g461,g460)
    c: Perpendicular(g196,g461)
    c: Distance(g461) = 3
    c: Coincident(g462,g461)
    c: Tangent(g462,g41)
    c: PointOnObject(g462,g94)
    c: Block(g462)
    c: Block(g459)
    c: Coincident(g463,g459)
    c: Parallel(g196,g463)
    c: Distance(g463) = 3
    c: Coincident(g464,g461)
    c: Distance(g464) = 3
    c: Parallel(g196,g464)
    c: Coincident(g465,g460)
    c: Distance(g465) = 6
    c: Parallel(g465,g196)
    c: Coincident(g466,g465)
    c: PointOnObject(g464,g466)
    c: Block(g466)
    c: Coincident(g467,g458)
    c: Vertical(g467)
    c: PointOnObject(g467,g195)
    c: Coincident(g468,g467)
    c: Perpendicular(g195,g468)
FEATURE [Sketcher::SketchObject] Sketch004  label="rightSideBottom"
  FullyConstrained = false
  sketch-geometry (91):
    g0: ArcOfCircle CenterX=391.073 CenterY=-83.7794 CenterZ=0 NormalX=0 NormalY=0 NormalZ=1 AngleXU=0 Radius=8 StartAngle=3.14159 EndAngle=6.28319
    g1: Circle CenterX=306.073 CenterY=-81.8102 CenterZ=0 NormalX=0 NormalY=0 NormalZ=1 AngleXU=0 Radius=1
    g2: Circle CenterX=306.073 CenterY=-77.8102 CenterZ=0 NormalX=0 NormalY=0 NormalZ=1 AngleXU=0 Radius=1
    g3: Circle CenterX=302.567 CenterY=-42.9683 CenterZ=0 NormalX=0 NormalY=0 NormalZ=1 AngleXU=0 Radius=1
    g4: Circle CenterX=306.073 CenterY=-44.8935 CenterZ=0 NormalX=0 NormalY=0 NormalZ=1 AngleXU=0 Radius=1
    g5: Circle CenterX=306.073 CenterY=-40.8935 CenterZ=0 NormalX=0 NormalY=0 NormalZ=1 AngleXU=0 Radius=1
    g6: BSplineCurve PolesCount=3 KnotsCount=2 Degree=2 IsPeriodic=0
    g7: GeomPoint X=302.567 Y=-42.9683 Z=0
    g8: GeomPoint X=306.073 Y=-40.8935 Z=0
    g9: Circle CenterX=371.567 CenterY=-80.8644 CenterZ=0 NormalX=0 NormalY=0 NormalZ=1 AngleXU=0 Radius=1
    g10: Circle CenterX=375.073 CenterY=-82.7896 CenterZ=0 NormalX=0 NormalY=0 NormalZ=1 AngleXU=0 Radius=1
    g11: Circle CenterX=375.073 CenterY=-78.7896 CenterZ=0 NormalX=0 NormalY=0 NormalZ=1 AngleXU=0 Radius=1
    g12: GeomPoint X=371.567 Y=-80.8644 Z=0
    g13: GeomPoint X=375.073 Y=-78.7896 Z=0
    g14: Circle CenterX=318.073 CenterY=-51.4823 CenterZ=0 NormalX=0 NormalY=0 NormalZ=1 AngleXU=0 Radius=1
    g15: Circle CenterX=318.073 CenterY=-47.4805 CenterZ=0 NormalX=0 NormalY=0 NormalZ=1 AngleXU=0 Radius=1
    g16: GeomPoint X=321.579 Y=-53.4075 Z=0
    g17: GeomPoint X=318.073 Y=-47.4805 Z=0
    g18: Circle CenterX=321.579 CenterY=-67.3492 CenterZ=0 NormalX=0 NormalY=0 NormalZ=1 AngleXU=0 Radius=1
    g19: Circle CenterX=318.073 CenterY=-65.424 CenterZ=0 NormalX=0 NormalY=0 NormalZ=1 AngleXU=0 Radius=1
    g20: Circle CenterX=318.073 CenterY=-69.424 CenterZ=0 NormalX=0 NormalY=0 NormalZ=1 AngleXU=0 Radius=1
    g21: GeomPoint X=321.579 Y=-67.3492 Z=0
    g22: GeomPoint X=318.073 Y=-69.424 Z=0
    g23: Circle CenterX=362.567 CenterY=-89.8542 CenterZ=0 NormalX=0 NormalY=0 NormalZ=1 AngleXU=0 Radius=1
    g24: Circle CenterX=366.073 CenterY=-91.7794 CenterZ=0 NormalX=0 NormalY=0 NormalZ=1 AngleXU=0 Radius=1
    g25: Circle CenterX=362.073 CenterY=-91.7794 CenterZ=0 NormalX=0 NormalY=0 NormalZ=1 AngleXU=0 Radius=1
    g26: GeomPoint X=362.567 Y=-89.8542 Z=0
    g27: GeomPoint X=362.073 Y=-91.7794 Z=0
    g28: Circle CenterX=322.073 CenterY=-91.7794 CenterZ=0 NormalX=0 NormalY=0 NormalZ=1 AngleXU=0 Radius=1
    g29: Circle CenterX=318.073 CenterY=-91.7794 CenterZ=0 NormalX=0 NormalY=0 NormalZ=1 AngleXU=0 Radius=1
    g30: Circle CenterX=318.073 CenterY=-87.7794 CenterZ=0 NormalX=0 NormalY=0 NormalZ=1 AngleXU=0 Radius=1
    g31: GeomPoint X=322.073 Y=-91.7794 Z=0
    g32: GeomPoint X=318.073 Y=-87.7794 Z=0
    g33: ArcOfCircle CenterX=391.073 CenterY=22.1087 CenterZ=0 NormalX=0 NormalY=0 NormalZ=1 AngleXU=0 Radius=4 StartAngle=0 EndAngle=3.14159
    g34: LineSegment StartX=387.073 StartY=22.1087 StartZ=0 EndX=383.073 EndY=-83.7794 EndZ=0
    g35: LineSegment StartX=395.073 StartY=22.1087 StartZ=0 EndX=399.073 EndY=-83.7794 EndZ=0
    g36: LineSegment StartX=232.072 StartY=-103.779 StartZ=0 EndX=232.072 EndY=-100.779 EndZ=0
    g37: GeomPoint X=232.072 Y=-94.7794 Z=0
    g38: GeomPoint X=223.072 Y=-97.7794 Z=0
    g39: Circle CenterX=232.072 CenterY=-94.7794 CenterZ=0 NormalX=0 NormalY=0 NormalZ=1 AngleXU=0 Radius=1
    g40: Circle CenterX=232.072 CenterY=-100.779 CenterZ=0 NormalX=0 NormalY=0 NormalZ=1 AngleXU=0 Radius=1
    g41: BSplineCurve PolesCount=5 KnotsCount=3 Degree=3 IsPeriodic=0
    g42: GeomPoint X=232.072 Y=-100.779 Z=0
    g43: LineSegment StartX=232.072 StartY=-94.7794 StartZ=0 EndX=232.072 EndY=-91.7794 EndZ=0
    g44: LineSegment StartX=245.072 StartY=-31.3037 StartZ=0 EndX=243.535 EndY=-33.1602 EndZ=0
    g45: LineSegment StartX=241.775 StartY=-35.2862 StartZ=0 EndX=240.266 EndY=-37.1092 EndZ=0
    g46: LineSegment StartX=243.535 StartY=-33.1602 StartZ=0 EndX=248.619 EndY=-37.3688 EndZ=0
    g47: LineSegment StartX=241.775 StartY=-35.2862 StartZ=0 EndX=246.859 EndY=-39.4949 EndZ=0
    g48: LineSegment StartX=248.619 StartY=-37.3688 StartZ=0 EndX=246.859 EndY=-39.4949 EndZ=0
    g49: LineSegment StartX=232.072 StartY=-103.779 StartZ=0 EndX=407.073 EndY=-103.779 EndZ=0
    g50: LineSegment StartX=299.888 StartY=-86.6413 StartZ=0 EndX=240.266 EndY=-37.1092 EndZ=0
    g51: LineSegment StartX=245.072 StartY=-11.4025 StartZ=0 EndX=302.567 EndY=-42.9683 EndZ=0
    g52: BSplineCurve PolesCount=3 KnotsCount=2 Degree=2 IsPeriodic=0
    g53: BSplineCurve PolesCount=3 KnotsCount=2 Degree=2 IsPeriodic=0
    g54: LineSegment StartX=321.579 StartY=-53.4075 StartZ=0 EndX=371.567 EndY=-80.8644 EndZ=0
    g55: BSplineCurve PolesCount=3 KnotsCount=2 Degree=2 IsPeriodic=0
    g56: BSplineCurve PolesCount=3 KnotsCount=2 Degree=2 IsPeriodic=0
    g57: BSplineCurve PolesCount=3 KnotsCount=2 Degree=2 IsPeriodic=0
    g58: LineSegment StartX=318.073 StartY=-69.424 StartZ=0 EndX=318.073 EndY=-87.7794 EndZ=0
    g59: LineSegment StartX=321.579 StartY=-67.3492 StartZ=0 EndX=362.567 EndY=-89.8542 EndZ=0
    g60: LineSegment StartX=362.073 StartY=-91.7794 StartZ=0 EndX=322.073 EndY=-91.7794 EndZ=0
    g61: BSplineCurve PolesCount=3 KnotsCount=2 Degree=2 IsPeriodic=0
    g62: BSplineCurve PolesCount=3 KnotsCount=2 Degree=2 IsPeriodic=0
    g63: LineSegment StartX=245.072 StartY=-31.3037 StartZ=0 EndX=302.996 EndY=-79.2541 EndZ=0
    g64: LineSegment StartX=302.567 StartY=-56.9099 StartZ=0 EndX=239.193 EndY=-22.1109 EndZ=0
    g65: LineSegment StartX=306.073 StartY=-62.8351 StartZ=0 EndX=306.073 EndY=-77.8102 EndZ=0
    g66: BSplineCurve PolesCount=3 KnotsCount=2 Degree=2 IsPeriodic=0
    g67: LineSegment StartX=298.776 StartY=-91.7794 StartZ=0 EndX=232.072 EndY=-91.7794 EndZ=0
    g68: LineSegment StartX=245.072 StartY=-11.4025 StartZ=0 EndX=243.628 EndY=-14.0323 EndZ=0
    g69: LineSegment StartX=240.741 StartY=-19.2917 StartZ=0 EndX=239.193 EndY=-22.1109 EndZ=0
    g70: LineSegment StartX=243.628 StartY=-14.0323 StartZ=0 EndX=246.258 EndY=-15.476 EndZ=0
    g71: LineSegment StartX=240.741 StartY=-19.2917 StartZ=0 EndX=243.37 EndY=-20.7355 EndZ=0
    g72: ArcOfCircle CenterX=247.444 CenterY=-19.5495 CenterZ=0 NormalX=0 NormalY=0 NormalZ=1 AngleXU=0 Radius=4.24264 StartAngle=3.4249 EndAngle=8.13729
    g73: LineSegment StartX=407.073 StartY=-103.779 StartZ=0 EndX=407.073 EndY=48.2206 EndZ=0
    g74: LineSegment StartX=375.073 StartY=48.2206 StartZ=0 EndX=375.073 EndY=-78.7896 EndZ=0
    g75: LineSegment StartX=375.073 StartY=48.2206 StartZ=0 EndX=382.073 EndY=48.2206 EndZ=0
    g76: LineSegment StartX=407.073 StartY=48.2206 StartZ=0 EndX=400.073 EndY=48.2206 EndZ=0
    g77: LineSegment StartX=394.073 StartY=48.2206 StartZ=0 EndX=394.073 EndY=52.2206 EndZ=0
    g78: LineSegment StartX=388.073 StartY=48.2206 StartZ=0 EndX=388.073 EndY=58.2206 EndZ=0
    g79: ArcOfCircle CenterX=385.073 CenterY=61.2206 CenterZ=0 NormalX=0 NormalY=0 NormalZ=1 AngleXU=0 Radius=4.24264 StartAngle=5.49779 EndAngle=10.2102
    g80: ArcOfCircle CenterX=397.073 CenterY=55.2206 CenterZ=0 NormalX=0 NormalY=0 NormalZ=1 AngleXU=0 Radius=4.24264 StartAngle=5.49779 EndAngle=10.2102
    g81: LineSegment StartX=382.073 StartY=58.2206 StartZ=0 EndX=382.073 EndY=48.2206 EndZ=0
    g82: LineSegment StartX=400.073 StartY=52.2206 StartZ=0 EndX=400.073 EndY=48.2206 EndZ=0
    g83: LineSegment StartX=394.073 StartY=48.2206 StartZ=0 EndX=388.073 EndY=48.2206 EndZ=0
    g84: LineSegment StartX=306.073 StartY=-40.8935 StartZ=0 EndX=306.073 EndY=-27.5935 EndZ=0
    g85: LineSegment StartX=318.073 StartY=-27.5935 StartZ=0 EndX=318.073 EndY=-47.4805 EndZ=0
    g86: LineSegment StartX=306.073 StartY=-27.5935 StartZ=0 EndX=310.073 EndY=-27.5935 EndZ=0
    g87: LineSegment StartX=318.073 StartY=-27.5935 StartZ=0 EndX=314.073 EndY=-27.5935 EndZ=0
    g88: LineSegment StartX=310.073 StartY=-27.5935 StartZ=0 EndX=310.073 EndY=-31.5935 EndZ=0
    g89: LineSegment StartX=314.073 StartY=-27.5935 StartZ=0 EndX=314.073 EndY=-31.5935 EndZ=0
    g90: ArcOfCircle CenterX=312.073 CenterY=-33.5935 CenterZ=0 NormalX=0 NormalY=0 NormalZ=1 AngleXU=0 Radius=2.82843 StartAngle=2.35619 EndAngle=7.06858
  constraints (121):
    c: Distance(g44) = 2.41
    c: Block(g44)
    c: Coincident(g46,g44)
    c: Coincident(g49,g36)
    c: Horizontal(g49)
    c: Block(g49)
    c: Coincident(g50,g45)
    c: Block(g50)
    c: Coincident(g51,g6)
    c: Block(g51)
    c: Coincident(g54,g52)
    c: Coincident(g54,g53)
    c: Coincident(g58,g56)
    c: Coincident(g58,g57)
    c: Vertical(g58)
    c: Coincident(g59,g56)
    c: Coincident(g59,g55)
    c: Coincident(g60,g55)
    c: Coincident(g60,g57)
    c: Horizontal(g60)
    c: Block(g61)
    c: Block(g62)
    c: Coincident(g63,g44)
    c: Coincident(g63,g62)
    c: Coincident(g64,g61)
    c: Coincident(g65,g61)
    c: Coincident(g65,g62)
    c: Vertical(g65)
    c: Block(g66)
    c: Coincident(g66,g50)
    c: Coincident(g67,g66)
    c: Coincident(g67,g43)
    c: Horizontal(g67)
    c: Coincident(g68,g51)
    c: Perpendicular(g68,g51)
    c: Coincident(g69,g64)
    c: Coincident(g70,g68)
    c: Distance(g70) = 3
    c: Distance(g71) = 3
    c: Perpendicular(g68,g70)
    c: Coincident(g72,g70)
    c: Coincident(g72,g71)
    c: Block(g72)
    c: Block(g69)
    c: Block(g71)
    c: Block(g54)
    c: Block(g59)
    c: Block(g58)
    c: Block(g60)
    c: Block(g67)
    c: Block(g43)
    c: Block(g36)
    c: Block(g48)
    c: Block(g46)
    c: Block(g47)
    c: Block(g45)
    c: Block(g35)
    c: Block(g34)
    c: Block(g0)
    c: Block(g33)
    c: Block(g52)
    c: Block(g6)
    c: Block(g41)
    c: Block(g57)
    c: Block(g55)
    c: Block(g53)
    c: Block(g68)
    c: Distance(g48) = 2.76
    c: Distance(g47) = 6.6
    c: Distance(g45) = 2.36657
    c: Coincident(g73,g49)
    c: Vertical(g73)
    c: Distance(g73) = 152
    c: Coincident(g74,g53)
    c: Vertical(g74)
    c: Block(g74)
    c: Coincident(g75,g74)
    c: Horizontal(g75)
    c: Distance(g75) = 7
    c: Horizontal(g76)
    c: Distance(g76) = 7
    c: Coincident(g76,g73)
    c: Vertical(g77)
    c: Distance(g77) = 4
    c: Vertical(g78)
    c: Distance(g78) = 10
    c: Coincident(g79,g78)
    c: Coincident(g80,g77)
    c: Block(g80)
    c: Block(g79)
    c: Coincident(g81,g79)
    c: Coincident(g81,g75)
    c: Vertical(g81)
    c: Coincident(g82,g80)
    c: Coincident(g82,g76)
    c: Vertical(g82)
    c: Coincident(g83,g77)
    c: Coincident(g83,g78)
    c: Horizontal(g83)
    c: Coincident(g84,g6)
    c: Vertical(g84)
    c: Distance(g84) = 13.3
    c: Coincident(g85,g52)
    c: Vertical(g85)
    c: Block(g85)
    c: Coincident(g86,g84)
    c: Horizontal(g86)
    c: Distance(g86) = 4
    c: Coincident(g87,g85)
    c: Horizontal(g87)
    c: Distance(g87) = 4
    c: Coincident(g88,g86)
    c: Vertical(g88)
    c: Coincident(g89,g87)
    c: Vertical(g89)
    c: Distance(g88) = 4
    c: Distance(g89) = 4
    c: Coincident(g90,g88)
    c: Coincident(g90,g89)
    c: Block(g90)
    c: Block(g56)
FEATURE [Sketcher::SketchObject] Sketch005  label="middleTop"
  FullyConstrained = true
  sketch-geometry (133):
    g0: Circle CenterX=175.025 CenterY=27.0667 CenterZ=0 NormalX=0 NormalY=0 NormalZ=1 AngleXU=0 Radius=1
    g1: Circle CenterX=179.022 CenterY=24.8665 CenterZ=0 NormalX=0 NormalY=0 NormalZ=1 AngleXU=0 Radius=1
    g2: Circle CenterX=179.022 CenterY=27.0606 CenterZ=0 NormalX=0 NormalY=0 NormalZ=1 AngleXU=0 Radius=1
    g3: BSplineCurve PolesCount=3 KnotsCount=2 Degree=2 IsPeriodic=0
    g4: GeomPoint X=175.025 Y=27.0667 Z=0
    g5: GeomPoint X=179.022 Y=27.0606 Z=0
    g6: Circle CenterX=189.124 CenterY=27.0628 CenterZ=0 NormalX=0 NormalY=0 NormalZ=1 AngleXU=0 Radius=1
    g7: Circle CenterX=185.124 CenterY=24.8665 CenterZ=0 NormalX=0 NormalY=0 NormalZ=1 AngleXU=0 Radius=1
    g8: Circle CenterX=185.124 CenterY=27.0606 CenterZ=0 NormalX=0 NormalY=0 NormalZ=1 AngleXU=0 Radius=1
    g9: BSplineCurve PolesCount=3 KnotsCount=2 Degree=2 IsPeriodic=0
    g10: GeomPoint X=189.124 Y=27.0628 Z=0
    g11: GeomPoint X=185.124 Y=27.0606 Z=0
    g12: Circle CenterX=165.871 CenterY=18.1458 CenterZ=0 NormalX=0 NormalY=0 NormalZ=1 AngleXU=0 Radius=1
    g13: Circle CenterX=169.377 CenterY=16.2206 CenterZ=0 NormalX=0 NormalY=0 NormalZ=1 AngleXU=0 Radius=1
    g14: Circle CenterX=165.871 CenterY=14.2956 CenterZ=0 NormalX=0 NormalY=0 NormalZ=1 AngleXU=0 Radius=1
    g15: BSplineCurve PolesCount=3 KnotsCount=2 Degree=2 IsPeriodic=0
    g16: GeomPoint X=165.871 Y=18.1458 Z=0
    g17: GeomPoint X=165.871 Y=14.2956 Z=0
    g18: Circle CenterX=198.275 CenterY=18.1318 CenterZ=0 NormalX=0 NormalY=0 NormalZ=1 AngleXU=0 Radius=1
    g19: Circle CenterX=194.768 CenterY=16.2206 CenterZ=0 NormalX=0 NormalY=0 NormalZ=1 AngleXU=0 Radius=1
    g20: Circle CenterX=198.264 CenterY=14.2963 CenterZ=0 NormalX=0 NormalY=0 NormalZ=1 AngleXU=0 Radius=1
    g21: BSplineCurve PolesCount=3 KnotsCount=2 Degree=2 IsPeriodic=0
    g22: GeomPoint X=198.275 Y=18.1318 Z=0
    g23: GeomPoint X=198.264 Y=14.2963 Z=0
    g24: Circle CenterX=125.607 CenterY=54.1951 CenterZ=0 NormalX=0 NormalY=0 NormalZ=1 AngleXU=0 Radius=1
    g25: Circle CenterX=139.632 CenterY=46.4944 CenterZ=0 NormalX=0 NormalY=0 NormalZ=1 AngleXU=0 Radius=1
    g26: Circle CenterX=127.326 CenterY=56.7187 CenterZ=0 NormalX=0 NormalY=0 NormalZ=1 AngleXU=0 Radius=1
    g27: BSplineCurve PolesCount=3 KnotsCount=2 Degree=2 IsPeriodic=0
    g28: GeomPoint X=125.607 Y=54.1951 Z=0
    g29: GeomPoint X=127.326 Y=56.7187 Z=0
    g30: Circle CenterX=236.824 CenterY=56.7187 CenterZ=0 NormalX=0 NormalY=0 NormalZ=1 AngleXU=0 Radius=1
    g31: Circle CenterX=224.513 CenterY=46.4944 CenterZ=0 NormalX=0 NormalY=0 NormalZ=1 AngleXU=0 Radius=1
    g32: Circle CenterX=238.538 CenterY=54.1951 CenterZ=0 NormalX=0 NormalY=0 NormalZ=1 AngleXU=0 Radius=1
    g33: BSplineCurve PolesCount=3 KnotsCount=2 Degree=2 IsPeriodic=0
    g34: GeomPoint X=236.824 Y=56.7187 Z=0
    g35: GeomPoint X=238.538 Y=54.1951 Z=0
    g36: Circle CenterX=189.121 CenterY=124.221 CenterZ=0 NormalX=0 NormalY=0 NormalZ=1 AngleXU=0 Radius=1
    g37: Circle CenterX=185.124 CenterY=124.221 CenterZ=0 NormalX=0 NormalY=0 NormalZ=1 AngleXU=0 Radius=1
    g38: Circle CenterX=185.124 CenterY=120.221 CenterZ=0 NormalX=0 NormalY=0 NormalZ=1 AngleXU=0 Radius=1
    g39: BSplineCurve PolesCount=3 KnotsCount=2 Degree=2 IsPeriodic=0
    g40: GeomPoint X=189.121 Y=124.221 Z=0
    g41: GeomPoint X=185.124 Y=120.221 Z=0
    g42: Circle CenterX=175.022 CenterY=124.221 CenterZ=0 NormalX=0 NormalY=0 NormalZ=1 AngleXU=0 Radius=1
    g43: Circle CenterX=179.022 CenterY=124.221 CenterZ=0 NormalX=0 NormalY=0 NormalZ=1 AngleXU=0 Radius=1
    g44: Circle CenterX=179.022 CenterY=120.221 CenterZ=0 NormalX=0 NormalY=0 NormalZ=1 AngleXU=0 Radius=1
    g45: BSplineCurve PolesCount=3 KnotsCount=2 Degree=2 IsPeriodic=0
    g46: GeomPoint X=175.022 Y=124.221 Z=0
    g47: GeomPoint X=179.022 Y=120.221 Z=0
    g48: LineSegment StartX=232.071 StartY=124.221 StartZ=0 EndX=232.071 EndY=127.221 EndZ=0
    g49-g52: Circle x4 (B-spline internal-alignment scaffolding for g53; pole/knot coordinates omitted)
    g53: BSplineCurve PolesCount=5 KnotsCount=3 Degree=3 IsPeriodic=0
    g54: GeomPoint X=232.072 Y=133.221 Z=0
    g55: GeomPoint X=223.072 Y=130.221 Z=0
    g56: GeomPoint X=232.071 Y=127.221 Z=0
    g57-g61: Circle x5 (B-spline internal-alignment scaffolding for g62; pole/knot coordinates omitted)
    g62: BSplineCurve PolesCount=5 KnotsCount=3 Degree=3 IsPeriodic=0
    g63: GeomPoint X=132.072 Y=133.221 Z=0
    g64: GeomPoint X=141.072 Y=130.221 Z=0
    g65: GeomPoint X=132.072 Y=127.221 Z=0
    g66: ArcOfCircle CenterX=247.391 CenterY=52.0843 CenterZ=0 NormalX=0 NormalY=0 NormalZ=1 AngleXU=0 Radius=4.24264 StartAngle=4.42912 EndAngle=9.14151
    g67: LineSegment StartX=240.687 StartY=51.8263 StartZ=0 EndX=239.192 EndY=54.5542 EndZ=0
    g68: LineSegment StartX=243.575 StartY=46.5669 StartZ=0 EndX=245.072 EndY=43.8408 EndZ=0
    g69: LineSegment StartX=240.168 StartY=69.471 StartZ=0 EndX=241.708 EndY=67.6172 EndZ=0
    g70: LineSegment StartX=246.783 StartY=71.8328 StartZ=0 EndX=248.546 EndY=69.7098 EndZ=0
    g71: LineSegment StartX=245.073 StartY=63.5726 StartZ=0 EndX=243.476 EndY=65.4955 EndZ=0
    g72: LineSegment StartX=123.967 StartY=69.4706 StartZ=0 EndX=122.37 EndY=67.5474 EndZ=0
    g73: LineSegment StartX=232.072 StartY=133.221 StartZ=0 EndX=232.072 EndY=136.221 EndZ=0
    g74: LineSegment StartX=232.072 StartY=136.221 StartZ=0 EndX=132.072 EndY=136.221 EndZ=0
    g75: LineSegment StartX=132.072 StartY=136.221 StartZ=0 EndX=132.072 EndY=133.221 EndZ=0
    g76: LineSegment StartX=132.072 StartY=127.221 StartZ=0 EndX=132.072 EndY=124.221 EndZ=0
    g77: LineSegment StartX=132.072 StartY=124.221 StartZ=0 EndX=175.022 EndY=124.221 EndZ=0
    g78: LineSegment StartX=189.121 StartY=124.221 StartZ=0 EndX=232.071 EndY=124.221 EndZ=0
    g79: LineSegment StartX=185.124 StartY=120.221 StartZ=0 EndX=185.124 EndY=27.0606 EndZ=0
    g80: LineSegment StartX=189.124 StartY=27.0628 StartZ=0 EndX=240.168 EndY=69.471 EndZ=0
    g81: LineSegment StartX=241.708 StartY=67.6172 StartZ=0 EndX=246.783 EndY=71.8328 EndZ=0
    g82: LineSegment StartX=248.546 StartY=69.7098 StartZ=0 EndX=243.476 EndY=65.4955 EndZ=0
    g83: LineSegment StartX=245.073 StartY=63.5726 StartZ=0 EndX=236.824 EndY=56.7187 EndZ=0
    g84: LineSegment StartX=238.538 StartY=54.1951 StartZ=0 EndX=239.192 EndY=54.5542 EndZ=0
    g85: LineSegment StartX=240.687 StartY=51.8263 StartZ=0 EndX=243.317 EndY=53.2701 EndZ=0
    g86: LineSegment StartX=246.205 StartY=48.0108 StartZ=0 EndX=243.575 EndY=46.5669 EndZ=0
    g87: LineSegment StartX=245.072 StartY=43.8408 StartZ=0 EndX=198.275 EndY=18.1318 EndZ=0
    g88: LineSegment StartX=165.871 StartY=18.1458 StartZ=0 EndX=118.934 EndY=43.9178 EndZ=0
    g89: LineSegment StartX=118.934 StartY=43.9178 StartZ=0 EndX=120.377 EndY=46.5474 EndZ=0
    g90: LineSegment StartX=117.748 StartY=47.9913 StartZ=0 EndX=120.377 EndY=46.5474 EndZ=0
    g91: LineSegment StartX=120.635 StartY=53.2507 StartZ=0 EndX=123.265 EndY=51.8068 EndZ=0
    g92: LineSegment StartX=123.265 StartY=51.8068 StartZ=0 EndX=124.73 EndY=54.6766 EndZ=0
    g93: ArcOfCircle CenterX=116.562 CenterY=52.0649 CenterZ=0 NormalX=0 NormalY=0 NormalZ=1 AngleXU=0 Radius=4.24264 StartAngle=0.283267 EndAngle=4.99566
    g94: LineSegment StartX=124.73 StartY=54.6766 StartZ=0 EndX=125.607 EndY=54.1951 EndZ=0
    g95: LineSegment StartX=127.326 StartY=56.7187 StartZ=0 EndX=119.072 EndY=63.5741 EndZ=0
    g96: LineSegment StartX=119.072 StartY=63.5741 StartZ=0 EndX=120.669 EndY=65.4973 EndZ=0
    g97: LineSegment StartX=120.669 StartY=65.4973 StartZ=0 EndX=115.591 EndY=69.7147 EndZ=0
    g98: LineSegment StartX=115.591 StartY=69.7147 StartZ=0 EndX=117.293 EndY=71.7641 EndZ=0
    g99: LineSegment StartX=117.293 StartY=71.7641 StartZ=0 EndX=122.37 EndY=67.5474 EndZ=0
    g100: LineSegment StartX=123.967 StartY=69.4706 StartZ=0 EndX=175.025 EndY=27.0667 EndZ=0
    g101: LineSegment StartX=179.022 StartY=27.0606 StartZ=0 EndX=179.022 EndY=120.221 EndZ=0
    g102-g117: Circle x16 (B-spline internal-alignment scaffolding for g118; pole/knot coordinates omitted)
    g118: BSplineCurve PolesCount=16 KnotsCount=14 Degree=3 IsPeriodic=0
    g119-g132: GeomPoint x14 (B-spline internal-alignment scaffolding for g118; pole/knot coordinates omitted)
  constraints (180):
    c: Weight(g0) = 1
    c: Equal(g0,g1)
    c: Equal(g0,g2)
    c: InternalAlignment(g0,g3)
    c: InternalAlignment(g1,g3)
    c: InternalAlignment(g2,g3)
    c: InternalAlignment(g4,g3)
    c: InternalAlignment(g5,g3)
    c: Weight(g6) = 1
    c: Equal(g6,g7)
    c: Equal(g6,g8)
    c: InternalAlignment(g6,g9)
    c: InternalAlignment(g7,g9)
    c: InternalAlignment(g8,g9)
    c: InternalAlignment(g10,g9)
    c: InternalAlignment(g11,g9)
    c: Block(g9)
    c: Block(g3)
    c: Weight(g12) = 1
    c: Equal(g12,g13)
    c: Equal(g12,g14)
    c: InternalAlignment(g12,g15)
    c: InternalAlignment(g13,g15)
    c: InternalAlignment(g14,g15)
    c: InternalAlignment(g16,g15)
    c: InternalAlignment(g17,g15)
    c: Weight(g18) = 1
    c: Equal(g18,g19)
    c: Equal(g18,g20)
    c: InternalAlignment(g18,g21)
    c: InternalAlignment(g19,g21)
    c: InternalAlignment(g20,g21)
    c: InternalAlignment(g22,g21)
    c: InternalAlignment(g23,g21)
    c: Block(g15)
    c: Block(g21)
    c: Weight(g24) = 1
    c: Equal(g24,g25)
    c: Equal(g24,g26)
    c: InternalAlignment(g24,g27)
    c: InternalAlignment(g25,g27)
    c: InternalAlignment(g26,g27)
    c: InternalAlignment(g28,g27)
    c: InternalAlignment(g29,g27)
    c: Block(g27)
    c: Weight(g30) = 1
    c: Equal(g30,g31)
    c: Equal(g30,g32)
    c: InternalAlignment(g30,g33)
    c: InternalAlignment(g31,g33)
    c: InternalAlignment(g32,g33)
    c: InternalAlignment(g34,g33)
    c: InternalAlignment(g35,g33)
    c: Block(g33)
    c: Weight(g36) = 1
    c: Equal(g36,g37)
    c: Equal(g36,g38)
    c: InternalAlignment(g36,g39)
    c: InternalAlignment(g37,g39)
    c: InternalAlignment(g38,g39)
    c: InternalAlignment(g40,g39)
    c: InternalAlignment(g41,g39)
    c: Weight(g42) = 1
    c: Equal(g42,g43)
    c: Equal(g42,g44)
    c: InternalAlignment(g42,g45)
    c: InternalAlignment(g43,g45)
    c: InternalAlignment(g44,g45)
    c: InternalAlignment(g46,g45)
    c: InternalAlignment(g47,g45)
    c: Block(g45)
    c: Block(g39)
    c: Vertical(g48)
    c: Distance(g48) = 3
    c: Weight(g49) = 1
    c: Equal(g49,g50)
    c: Equal(g49,g51)
    c: Equal(g49,g52)
    c: Coincident(g53,g48)
    c: InternalAlignment(g49-g52 -> g53) x4
    c: InternalAlignment(g54,g53)
    c: InternalAlignment(g55,g53)
    c: InternalAlignment(g56,g53)
    c: Weight(g57) = 1
    c: Equal(g57, g58-g61) x4
    c: InternalAlignment(g57-g61 -> g62) x5
    c: InternalAlignment(g63,g62)
    c: InternalAlignment(g64,g62)
    c: InternalAlignment(g65,g62)
    c: Block(g62)
    c: Block(g67)
    c: Block(g68)
    c: Distance(g69) = 2.41
    c: Distance(g70) = 2.76
    c: Distance(g71) = 2.5
    c: Distance(g72) = 2.5
    c: Block(g66)
    c: Block(g48)
    c: Block(g53)
    c: Coincident(g73,g53)
    c: Vertical(g73)
    c: Distance(g73) = 3
    c: Coincident(g74,g73)
    c: Horizontal(g74)
    c: Distance(g74) = 100
    c: Coincident(g75,g74)
    c: Coincident(g75,g62)
    c: Vertical(g75)
    c: Distance(g75) = 3
    c: Coincident(g76,g62)
    c: Vertical(g76)
    c: Distance(g76) = 3
    c: Coincident(g77,g76)
    c: Coincident(g77,g45)
    c: Horizontal(g77)
    c: Distance(g77) = 42.95
    c: Coincident(g78,g39)
    c: Coincident(g78,g48)
    c: Horizontal(g78)
    c: Distance(g78) = 42.95
    c: Coincident(g79,g39)
    c: Coincident(g79,g9)
    c: Vertical(g79)
    c: Distance(g79) = 93.16
    c: Coincident(g80,g9)
    c: Coincident(g80,g69)
    c: Angle(g80) = 0.693245
    c: Block(g80)
    c: Coincident(g81,g69)
    c: Coincident(g81,g70)
    c: Block(g81)
    c: Coincident(g82,g70)
    c: Coincident(g82,g71)
    c: Block(g82)
    c: Coincident(g83,g71)
    c: Coincident(g83,g33)
    c: Block(g71)
    c: Coincident(g84,g33)
    c: Coincident(g84,g67)
    c: Coincident(g85,g67)
    c: Coincident(g85,g66)
    c: Coincident(g86,g66)
    c: Coincident(g86,g68)
    c: Coincident(g87,g68)
    c: Coincident(g87,g21)
    c: Coincident(g88,g15)
    c: Coincident(g89,g88)
    c: Block(g89)
    c: Coincident(g90,g89)
    c: Block(g90)
    c: Block(g91)
    c: Coincident(g92,g91)
    c: Block(g92)
    c: Coincident(g93,g91)
    c: Coincident(g93,g90)
    c: Block(g93)
    c: Coincident(g94,g92)
    c: Coincident(g94,g27)
    c: Coincident(g95,g27)
    c: Block(g95)
    c: Coincident(g96,g95)
    c: Coincident(g97,g96)
    c: Coincident(g98,g97)
    c: Coincident(g99,g98)
    c: Coincident(g99,g72)
    c: Block(g98)
    c: Block(g96)
    c: Block(g72)
    c: Coincident(g100,g72)
    c: Coincident(g100,g3)
    c: Coincident(g101,g3)
    c: Coincident(g101,g45)
    c: Vertical(g101)
    c: Coincident(g118,g21)
    c: Weight(g102) = 1
    c: Equal(g102, g103-g117) x15
    c: Coincident(g118,g15)
    c: InternalAlignment(g102-g117 -> g118) x16
    c: InternalAlignment(g119-g132 -> g118) x14
    c: Block(g118)
FEATURE [Sketcher::SketchObject] Sketch006  label="leftSideTop"
  FullyConstrained = true
  sketch-geometry (99):
    g0: Circle CenterX=61.1495 CenterY=111.695 CenterZ=0 NormalX=0 NormalY=0 NormalZ=1 AngleXU=0 Radius=1
    g1: Circle CenterX=58.0728 CenterY=114.251 CenterZ=0 NormalX=0 NormalY=0 NormalZ=1 AngleXU=0 Radius=1
    g2: Circle CenterX=58.0728 CenterY=110.251 CenterZ=0 NormalX=0 NormalY=0 NormalZ=1 AngleXU=0 Radius=1
    g3: BSplineCurve PolesCount=3 KnotsCount=2 Degree=2 IsPeriodic=0
    g4: GeomPoint X=61.1495 Y=111.695 Z=0
    g5: GeomPoint X=58.0728 Y=110.251 Z=0
    g6: Circle CenterX=61.5791 CenterY=89.3511 CenterZ=0 NormalX=0 NormalY=0 NormalZ=1 AngleXU=0 Radius=1
    g7: Circle CenterX=58.0728 CenterY=91.2763 CenterZ=0 NormalX=0 NormalY=0 NormalZ=1 AngleXU=0 Radius=1
    g8: Circle CenterX=58.0728 CenterY=95.2763 CenterZ=0 NormalX=0 NormalY=0 NormalZ=1 AngleXU=0 Radius=1
    g9: BSplineCurve PolesCount=3 KnotsCount=2 Degree=2 IsPeriodic=0
    g10: GeomPoint X=61.5791 Y=89.3511 Z=0
    g11: GeomPoint X=58.0728 Y=95.2763 Z=0
    g12: Circle CenterX=62.0728 CenterY=124.221 CenterZ=0 NormalX=0 NormalY=0 NormalZ=1 AngleXU=0 Radius=1
    g13: Circle CenterX=58.0728 CenterY=124.221 CenterZ=0 NormalX=0 NormalY=0 NormalZ=1 AngleXU=0 Radius=1
    g14: Circle CenterX=61.1496 CenterY=121.665 CenterZ=0 NormalX=0 NormalY=0 NormalZ=1 AngleXU=0 Radius=1
    g15: BSplineCurve PolesCount=3 KnotsCount=2 Degree=2 IsPeriodic=0
    g16: GeomPoint X=62.0728 Y=124.221 Z=0
    g17: GeomPoint X=61.1496 Y=121.665 Z=0
    g18: Circle CenterX=61.5791 CenterY=75.4095 CenterZ=0 NormalX=0 NormalY=0 NormalZ=1 AngleXU=0 Radius=1
    g19: Circle CenterX=58.0728 CenterY=77.3346 CenterZ=0 NormalX=0 NormalY=0 NormalZ=1 AngleXU=0 Radius=1
    g20: Circle CenterX=58.0728 CenterY=73.3346 CenterZ=0 NormalX=0 NormalY=0 NormalZ=1 AngleXU=0 Radius=1
    g21: BSplineCurve PolesCount=3 KnotsCount=2 Degree=2 IsPeriodic=0
    g22: GeomPoint X=61.5791 Y=75.4095 Z=0
    g23: GeomPoint X=58.0728 Y=73.3346 Z=0
    g24: Circle CenterX=2.07281 CenterY=124.221 CenterZ=0 NormalX=0 NormalY=0 NormalZ=1 AngleXU=0 Radius=1
    g25: Circle CenterX=1.57905 CenterY=122.295 CenterZ=0 NormalX=0 NormalY=0 NormalZ=1 AngleXU=0 Radius=1
    g26: BSplineCurve PolesCount=3 KnotsCount=2 Degree=2 IsPeriodic=0
    g27: GeomPoint X=2.07281 Y=124.221 Z=0
    g28: GeomPoint X=1.57905 Y=122.295 Z=0
    g29: Circle CenterX=46.0728 CenterY=124.221 CenterZ=0 NormalX=0 NormalY=0 NormalZ=1 AngleXU=0 Radius=1
    g30: Circle CenterX=46.0728 CenterY=120.221 CenterZ=0 NormalX=0 NormalY=0 NormalZ=1 AngleXU=0 Radius=1
    g31: BSplineCurve PolesCount=3 KnotsCount=2 Degree=2 IsPeriodic=0
    g32: GeomPoint X=42.0728 Y=124.221 Z=0
    g33: GeomPoint X=46.0728 Y=120.221 Z=0
    g34: Circle CenterX=46.0728 CenterY=109.865 CenterZ=0 NormalX=0 NormalY=0 NormalZ=1 AngleXU=0 Radius=1
    g35: Circle CenterX=46.0728 CenterY=105.865 CenterZ=0 NormalX=0 NormalY=0 NormalZ=1 AngleXU=0 Radius=1
    g36: Circle CenterX=42.0728 CenterY=105.865 CenterZ=0 NormalX=0 NormalY=0 NormalZ=1 AngleXU=0 Radius=1
    g37: BSplineCurve PolesCount=3 KnotsCount=2 Degree=2 IsPeriodic=0
    g38: GeomPoint X=46.0728 Y=109.865 Z=0
    g39: GeomPoint X=42.0728 Y=105.865 Z=0
    g40: Circle CenterX=35.5028 CenterY=105.865 CenterZ=0 NormalX=0 NormalY=0 NormalZ=1 AngleXU=0 Radius=1
    g41: Circle CenterX=31.5028 CenterY=105.865 CenterZ=0 NormalX=0 NormalY=0 NormalZ=1 AngleXU=0 Radius=1
    g42: Circle CenterX=27.9965 CenterY=107.79 CenterZ=0 NormalX=0 NormalY=0 NormalZ=1 AngleXU=0 Radius=1
    g43: BSplineCurve PolesCount=3 KnotsCount=2 Degree=2 IsPeriodic=0
    g44: GeomPoint X=35.5028 Y=105.865 Z=0
    g45: GeomPoint X=27.9965 Y=107.79 Z=0
    g46-g50: Circle x5 (B-spline internal-alignment scaffolding for g51; pole/knot coordinates omitted)
    g51: BSplineCurve PolesCount=5 KnotsCount=3 Degree=3 IsPeriodic=0
    g52: GeomPoint X=132.072 Y=133.221 Z=0
    g53: GeomPoint X=141.072 Y=130.221 Z=0
    g54: GeomPoint X=132.072 Y=127.221 Z=0
    g55: ArcOfCircle CenterX=116.562 CenterY=52.0649 CenterZ=0 NormalX=0 NormalY=0 NormalZ=1 AngleXU=0 Radius=4.24264 StartAngle=0.283268 EndAngle=4.99566
    g56: LineSegment StartX=123.967 StartY=69.4706 StartZ=0 EndX=122.37 EndY=67.5474 EndZ=0
    g57: LineSegment StartX=117.293 StartY=71.7641 StartZ=0 EndX=115.591 EndY=69.7147 EndZ=0
    g58: LineSegment StartX=120.669 StartY=65.4973 StartZ=0 EndX=119.072 EndY=63.5741 EndZ=0
    g59: LineSegment StartX=124.73 StartY=54.6766 StartZ=0 EndX=123.265 EndY=51.8068 EndZ=0
    g60: LineSegment StartX=120.377 StartY=46.5474 StartZ=0 EndX=118.934 EndY=43.9178 EndZ=0
    g61: BSplineCurve PolesCount=3 KnotsCount=2 Degree=2 IsPeriodic=0
    g62: BSplineCurve PolesCount=3 KnotsCount=2 Degree=2 IsPeriodic=0
    g63: LineSegment StartX=61.5791 StartY=75.4095 StartZ=0 EndX=118.934 EndY=43.9178 EndZ=0
    g64: LineSegment StartX=117.748 StartY=47.9913 StartZ=0 EndX=120.377 EndY=46.5474 EndZ=0
    g65: LineSegment StartX=120.635 StartY=53.2507 StartZ=0 EndX=123.265 EndY=51.8068 EndZ=0
    g66: LineSegment StartX=124.73 StartY=54.6766 StartZ=0 EndX=61.5791 EndY=89.3511 EndZ=0
    g67: LineSegment StartX=58.0728 StartY=95.2763 StartZ=0 EndX=58.0728 EndY=110.251 EndZ=0
    g68: LineSegment StartX=61.1495 StartY=111.695 StartZ=0 EndX=119.072 EndY=63.5741 EndZ=0
    g69: LineSegment StartX=120.669 StartY=65.4973 StartZ=0 EndX=115.591 EndY=69.7147 EndZ=0
    g70: LineSegment StartX=117.293 StartY=71.7641 StartZ=0 EndX=122.37 EndY=67.5474 EndZ=0
    g71: LineSegment StartX=123.967 StartY=69.4706 StartZ=0 EndX=61.1496 EndY=121.665 EndZ=0
    g72: LineSegment StartX=62.0728 StartY=124.221 StartZ=0 EndX=132.072 EndY=124.221 EndZ=0
    g73: LineSegment StartX=132.072 StartY=127.221 StartZ=0 EndX=132.072 EndY=124.221 EndZ=0
    g74: LineSegment StartX=132.072 StartY=133.221 StartZ=0 EndX=132.072 EndY=136.221 EndZ=0
    g75: LineSegment StartX=132.072 StartY=136.221 StartZ=0 EndX=-42.9272 EndY=136.221 EndZ=0
    g76: LineSegment StartX=2.07281 StartY=124.221 StartZ=0 EndX=42.0728 EndY=124.221 EndZ=0
    g77: LineSegment StartX=46.0728 StartY=120.221 StartZ=0 EndX=46.0728 EndY=109.865 EndZ=0
    g78: LineSegment StartX=42.0728 StartY=105.865 StartZ=0 EndX=35.5028 EndY=105.865 EndZ=0
    g79: LineSegment StartX=27.9965 StartY=107.79 StartZ=0 EndX=1.57905 EndY=122.295 EndZ=0
    g80: LineSegment StartX=-6.92718 StartY=76.4095 StartZ=0 EndX=42.0728 EndY=76.4095 EndZ=0
    g81: LineSegment StartX=-17.9272 StartY=48.2206 StartZ=0 EndX=-17.9272 EndY=58.2206 EndZ=0
    g82: LineSegment StartX=-35.9272 StartY=48.2206 StartZ=0 EndX=-35.9272 EndY=52.2206 EndZ=0
    g83: LineSegment StartX=-29.9272 StartY=48.2206 StartZ=0 EndX=-29.9272 EndY=52.2206 EndZ=0
    g84: LineSegment StartX=-23.9272 StartY=48.2206 StartZ=0 EndX=-23.9272 EndY=58.2206 EndZ=0
    g85: ArcOfCircle CenterX=-32.9272 CenterY=55.2206 CenterZ=0 NormalX=0 NormalY=0 NormalZ=1 AngleXU=0 Radius=4.24264 StartAngle=5.49779 EndAngle=10.2102
    g86: ArcOfCircle CenterX=-20.9272 CenterY=61.2206 CenterZ=0 NormalX=0 NormalY=0 NormalZ=1 AngleXU=0 Radius=4.24264 StartAngle=5.49779 EndAngle=10.2102
    g87: LineSegment StartX=-10.9272 StartY=48.2206 StartZ=0 EndX=-10.9272 EndY=72.4095 EndZ=0
    g88: LineSegment StartX=-42.9272 StartY=48.2206 StartZ=0 EndX=-42.9272 EndY=136.221 EndZ=0
    g89: LineSegment StartX=46.0728 StartY=72.4095 StartZ=0 EndX=46.0728 EndY=-27.5905 EndZ=0
    g90: LineSegment StartX=58.0728 StartY=-27.5905 StartZ=0 EndX=58.0728 EndY=73.3346 EndZ=0
    g91: LineSegment StartX=50.0728 StartY=-27.5905 StartZ=0 EndX=50.0728 EndY=-31.5905 EndZ=0
    g92: LineSegment StartX=54.0728 StartY=-27.5905 StartZ=0 EndX=54.0728 EndY=-31.5905 EndZ=0
    g93: ArcOfCircle CenterX=52.0728 CenterY=-33.5905 CenterZ=0 NormalX=0 NormalY=0 NormalZ=1 AngleXU=0 Radius=2.82843 StartAngle=2.35619 EndAngle=7.06858
    g94: LineSegment StartX=46.0728 StartY=-27.5905 StartZ=0 EndX=50.0728 EndY=-27.5905 EndZ=0
    g95: LineSegment StartX=54.0728 StartY=-27.5905 StartZ=0 EndX=58.0728 EndY=-27.5905 EndZ=0
    g96: LineSegment StartX=-17.9272 StartY=48.2206 StartZ=0 EndX=-10.9272 EndY=48.2206 EndZ=0
    g97: LineSegment StartX=-29.9272 StartY=48.2206 StartZ=0 EndX=-23.9272 EndY=48.2206 EndZ=0
    g98: LineSegment StartX=-42.9272 StartY=48.2206 StartZ=0 EndX=-35.9272 EndY=48.2206 EndZ=0
  constraints (172):
    c: Weight(g0) = 1
    c: Equal(g0,g1)
    c: Equal(g0,g2)
    c: InternalAlignment(g0,g3)
    c: InternalAlignment(g1,g3)
    c: InternalAlignment(g2,g3)
    c: InternalAlignment(g4,g3)
    c: InternalAlignment(g5,g3)
    c: Weight(g6) = 1
    c: Equal(g6,g7)
    c: Equal(g6,g8)
    c: InternalAlignment(g6,g9)
    c: InternalAlignment(g7,g9)
    c: InternalAlignment(g8,g9)
    c: InternalAlignment(g10,g9)
    c: InternalAlignment(g11,g9)
    c: Block(g3)
    c: Block(g9)
    c: Weight(g12) = 1
    c: Equal(g12,g13)
    c: Equal(g12,g14)
    c: InternalAlignment(g12,g15)
    c: InternalAlignment(g13,g15)
    c: InternalAlignment(g14,g15)
    c: InternalAlignment(g16,g15)
    c: InternalAlignment(g17,g15)
    c: Block(g15)
    c: Weight(g18) = 1
    c: Equal(g18,g19)
    c: Equal(g18,g20)
    c: InternalAlignment(g18,g21)
    c: InternalAlignment(g19,g21)
    c: InternalAlignment(g20,g21)
    c: InternalAlignment(g22,g21)
    c: InternalAlignment(g23,g21)
    c: Block(g21)
    c: Weight(g24) = 1
    c: Equal(g24,g25)
    c: InternalAlignment(g24,g26)
    c: InternalAlignment(g25,g26)
    c: InternalAlignment(g27,g26)
    c: InternalAlignment(g28,g26)
    c: InternalAlignment(g29,g31)
    c: InternalAlignment(g30,g31)
    c: InternalAlignment(g32,g31)
    c: InternalAlignment(g33,g31)
    c: Weight(g34) = 1
    c: Equal(g34,g35)
    c: Equal(g34,g36)
    c: InternalAlignment(g34,g37)
    c: InternalAlignment(g35,g37)
    c: InternalAlignment(g36,g37)
    c: InternalAlignment(g38,g37)
    c: InternalAlignment(g39,g37)
    c: Equal(g40,g41)
    c: Equal(g40,g42)
    c: InternalAlignment(g40,g43)
    c: InternalAlignment(g41,g43)
    c: InternalAlignment(g42,g43)
    c: InternalAlignment(g44,g43)
    c: InternalAlignment(g45,g43)
    c: Block(g31)
    c: Block(g37)
    c: Block(g43)
    c: Block(g26)
    c: Weight(g46) = 1
    c: Equal(g46, g47-g50) x4
    c: InternalAlignment(g46-g50 -> g51) x5
    c: InternalAlignment(g52,g51)
    c: InternalAlignment(g53,g51)
    c: InternalAlignment(g54,g51)
    c: Block(g51)
    c: Block(g55)
    c: Block(g56)
    c: Block(g57)
    c: Block(g58)
    c: Block(g59)
    c: Block(g60)
    c: Block(g61)
    c: Block(g62)
    c: Coincident(g90,g21)
    c: Coincident(g63,g21)
    c: Coincident(g63,g60)
    c: Coincident(g64,g55)
    c: Coincident(g64,g60)
    c: Coincident(g65,g55)
    c: Coincident(g65,g59)
    c: Coincident(g66,g59)
    c: Coincident(g66,g9)
    c: Coincident(g67,g9)
    c: Coincident(g67,g3)
    c: Vertical(g67)
    c: Coincident(g68,g3)
    c: Coincident(g68,g58)
    c: Coincident(g69,g58)
    c: Coincident(g69,g57)
    c: Coincident(g70,g57)
    c: Coincident(g70,g56)
    c: Coincident(g71,g56)
    c: Coincident(g71,g15)
    c: Coincident(g72,g15)
    c: Horizontal(g72)
    c: Coincident(g73,g51)
    c: Coincident(g73,g72)
    c: Vertical(g73)
    c: Coincident(g74,g51)
    c: Vertical(g74)
    c: Coincident(g75,g74)
    c: Horizontal(g75)
    c: Coincident(g76,g26)
    c: Coincident(g76,g31)
    c: Horizontal(g76)
    c: Coincident(g77,g31)
    c: Coincident(g77,g37)
    c: Vertical(g77)
    c: Coincident(g78,g37)
    c: Coincident(g78,g43)
    c: Horizontal(g78)
    c: Coincident(g79,g43)
    c: Coincident(g79,g26)
    c: Coincident(g80,g62)
    c: Coincident(g80,g61)
    c: Horizontal(g80)
    c: Vertical(g81)
    c: Distance(g81) = 10
    c: Vertical(g82)
    c: Distance(g82) = 4
    c: Vertical(g83)
    c: Distance(g83) = 4
    c: Vertical(g84)
    c: Distance(g84) = 10
    c: Coincident(g85,g83)
    c: Coincident(g85,g82)
    c: Block(g85)
    c: Coincident(g86,g84)
    c: Coincident(g86,g81)
    c: Block(g86)
    c: Coincident(g87,g62)
    c: Vertical(g87)
    c: Coincident(g88,g75)
    c: Vertical(g88)
    c: Block(g75)
    c: Coincident(g89,g61)
    c: Vertical(g89)
    c: Distance(g89) = 100
    c: Block(g90)
    c: Vertical(g91)
    c: Distance(g91) = 4
    c: Vertical(g92)
    c: Distance(g92) = 4
    c: Coincident(g93,g91)
    c: Coincident(g93,g92)
    c: Block(g93)
    c: Coincident(g94,g89)
    c: Coincident(g94,g91)
    c: Horizontal(g94)
    c: Distance(g94) = 4
    c: Coincident(g95,g92)
    c: Coincident(g95,g90)
    c: Horizontal(g95)
    c: Distance(g95) = 4
    c: Block(g87)
    c: Block(g88)
    c: Coincident(g96,g81)
    c: Coincident(g96,g87)
    c: Horizontal(g96)
    c: Coincident(g97,g83)
    c: Coincident(g97,g84)
    c: Horizontal(g97)
    c: Coincident(g98,g88)
    c: Coincident(g98,g82)
    c: Horizontal(g98)
FEATURE [Sketcher::SketchObject] Sketch007  label="leftSideBottom"
  FullyConstrained = true
  sketch-geometry (92):
    g0: ArcOfCircle CenterX=-26.9272 CenterY=-83.7794 CenterZ=0 NormalX=0 NormalY=0 NormalZ=1 AngleXU=0 Radius=8 StartAngle=3.14159 EndAngle=6.28319
    g1: Circle CenterX=61.5791 CenterY=-56.9099 CenterZ=0 NormalX=0 NormalY=0 NormalZ=1 AngleXU=0 Radius=1
    g2: Circle CenterX=58.0728 CenterY=-58.8351 CenterZ=0 NormalX=0 NormalY=0 NormalZ=1 AngleXU=0 Radius=1
    g3: Circle CenterX=58.0728 CenterY=-62.8351 CenterZ=0 NormalX=0 NormalY=0 NormalZ=1 AngleXU=0 Radius=1
    g4: BSplineCurve PolesCount=3 KnotsCount=2 Degree=2 IsPeriodic=0
    g5: GeomPoint X=61.5791 Y=-56.9099 Z=0
    g6: GeomPoint X=58.0728 Y=-62.8351 Z=0
    g7: Circle CenterX=58.0728 CenterY=-77.8102 CenterZ=0 NormalX=0 NormalY=0 NormalZ=1 AngleXU=0 Radius=1
    g8: Circle CenterX=58.0728 CenterY=-81.8102 CenterZ=0 NormalX=0 NormalY=0 NormalZ=1 AngleXU=0 Radius=1
    g9: Circle CenterX=61.1496 CenterY=-79.2541 CenterZ=0 NormalX=0 NormalY=0 NormalZ=1 AngleXU=0 Radius=1
    g10: BSplineCurve PolesCount=3 KnotsCount=2 Degree=2 IsPeriodic=0
    g11: GeomPoint X=58.0728 Y=-77.8102 Z=0
    g12: GeomPoint X=61.1496 Y=-79.2541 Z=0
    g13: Circle CenterX=61.6457 CenterY=-88.8112 CenterZ=0 NormalX=0 NormalY=0 NormalZ=1 AngleXU=0 Radius=1
    g14: Circle CenterX=58.0728 CenterY=-91.7794 CenterZ=0 NormalX=0 NormalY=0 NormalZ=1 AngleXU=0 Radius=1
    g15: Circle CenterX=63.9135 CenterY=-91.8014 CenterZ=0 NormalX=0 NormalY=0 NormalZ=1 AngleXU=0 Radius=1
    g16: BSplineCurve PolesCount=3 KnotsCount=2 Degree=2 IsPeriodic=0
    g17: GeomPoint X=61.6457 Y=-88.8112 Z=0
    g18: GeomPoint X=63.9135 Y=-91.8014 Z=0
    g19: Circle CenterX=58.0728 CenterY=-40.8935 CenterZ=0 NormalX=0 NormalY=0 NormalZ=1 AngleXU=0 Radius=1
    g20: Circle CenterX=58.0728 CenterY=-44.8935 CenterZ=0 NormalX=0 NormalY=0 NormalZ=1 AngleXU=0 Radius=1
    g21: Circle CenterX=61.5791 CenterY=-42.9683 CenterZ=0 NormalX=0 NormalY=0 NormalZ=1 AngleXU=0 Radius=1
    g22: BSplineCurve PolesCount=3 KnotsCount=2 Degree=2 IsPeriodic=0
    g23: GeomPoint X=58.0728 Y=-40.8935 Z=0
    g24: GeomPoint X=61.5791 Y=-42.9683 Z=0
    g25: Circle CenterX=42.5666 CenterY=-67.3492 CenterZ=0 NormalX=0 NormalY=0 NormalZ=1 AngleXU=0 Radius=1
    g26: Circle CenterX=46.0728 CenterY=-65.424 CenterZ=0 NormalX=0 NormalY=0 NormalZ=1 AngleXU=0 Radius=1
    g27: Circle CenterX=46.0728 CenterY=-69.424 CenterZ=0 NormalX=0 NormalY=0 NormalZ=1 AngleXU=0 Radius=1
    g28: BSplineCurve PolesCount=3 KnotsCount=2 Degree=2 IsPeriodic=0
    g29: GeomPoint X=42.5666 Y=-67.3492 Z=0
    g30: GeomPoint X=46.0728 Y=-69.424 Z=0
    g31: Circle CenterX=2.07281 CenterY=-91.7794 CenterZ=0 NormalX=0 NormalY=0 NormalZ=1 AngleXU=0 Radius=1
    g32: Circle CenterX=-1.92719 CenterY=-91.7794 CenterZ=0 NormalX=0 NormalY=0 NormalZ=1 AngleXU=0 Radius=1
    g33: Circle CenterX=1.57905 CenterY=-89.8542 CenterZ=0 NormalX=0 NormalY=0 NormalZ=1 AngleXU=0 Radius=1
    g34: BSplineCurve PolesCount=3 KnotsCount=2 Degree=2 IsPeriodic=0
    g35: GeomPoint X=2.07281 Y=-91.7794 Z=0
    g36: GeomPoint X=1.57905 Y=-89.8542 Z=0
    g37: ArcOfCircle CenterX=-26.9272 CenterY=22.1087 CenterZ=0 NormalX=0 NormalY=0 NormalZ=1 AngleXU=0 Radius=4 StartAngle=5e-16 EndAngle=3.14159
    g38: Circle CenterX=-10.9272 CenterY=-78.7794 CenterZ=0 NormalX=0 NormalY=0 NormalZ=1 AngleXU=0 Radius=1
    g39: Circle CenterX=-10.9272 CenterY=-82.7794 CenterZ=0 NormalX=0 NormalY=0 NormalZ=1 AngleXU=0 Radius=1
    g40: Circle CenterX=-7.42095 CenterY=-80.8542 CenterZ=0 NormalX=0 NormalY=0 NormalZ=1 AngleXU=0 Radius=1
    g41: BSplineCurve PolesCount=3 KnotsCount=2 Degree=2 IsPeriodic=0
    g42: GeomPoint X=-10.9272 Y=-78.7794 Z=0
    g43: GeomPoint X=-7.42095 Y=-80.8542 Z=0
    g44: BSplineCurve PolesCount=3 KnotsCount=2 Degree=2 IsPeriodic=0
    g45: GeomPoint X=42.5666 Y=-53.4075 Z=0
    g46: GeomPoint X=46.0728 Y=-47.4823 Z=0
    g47: BSplineCurve PolesCount=5 KnotsCount=3 Degree=3 IsPeriodic=0
    g48: LineSegment StartX=124.814 StartY=-22.1885 StartZ=0 EndX=123.265 EndY=-19.3655 EndZ=0
    g49: ArcOfCircle CenterX=116.562 CenterY=-19.6236 CenterZ=0 NormalX=0 NormalY=0 NormalZ=1 AngleXU=0 Radius=4.24264 StartAngle=1.28753 EndAngle=6.00037
    g50: LineSegment StartX=-30.9272 StartY=22.1087 StartZ=0 EndX=-34.9272 EndY=-83.7794 EndZ=0
    g51: LineSegment StartX=-22.9272 StartY=22.1087 StartZ=0 EndX=-18.9272 EndY=-83.7794 EndZ=0
    g52: LineSegment StartX=118.934 StartY=-11.4765 StartZ=0 EndX=120.377 EndY=-14.1062 EndZ=0
    g53: LineSegment StartX=118.86 StartY=-31.3104 StartZ=0 EndX=120.377 EndY=-33.1447 EndZ=0
    g54: LineSegment StartX=115.291 StartY=-37.3514 StartZ=0 EndX=117.05 EndY=-39.4781 EndZ=0
    g55: LineSegment StartX=122.136 StartY=-35.2714 StartZ=0 EndX=123.656 EndY=-37.1092 EndZ=0
    g56: BSplineCurve PolesCount=3 KnotsCount=2 Degree=2 IsPeriodic=0
    g57: LineSegment StartX=132.072 StartY=-100.779 StartZ=0 EndX=132.072 EndY=-103.779 EndZ=0
    g58: LineSegment StartX=132.072 StartY=-91.8014 StartZ=0 EndX=132.072 EndY=-94.7791 EndZ=0
    g59: LineSegment StartX=63.9135 StartY=-91.8014 StartZ=0 EndX=132.072 EndY=-91.8014 EndZ=0
    g60: LineSegment StartX=61.6457 StartY=-88.8112 StartZ=0 EndX=123.656 EndY=-37.1092 EndZ=0
    g61: LineSegment StartX=122.136 StartY=-35.2714 StartZ=0 EndX=117.05 EndY=-39.4781 EndZ=0
    g62: LineSegment StartX=115.291 StartY=-37.3514 StartZ=0 EndX=120.377 EndY=-33.1447 EndZ=0
    g63: LineSegment StartX=118.86 StartY=-31.3104 StartZ=0 EndX=61.1496 EndY=-79.2541 EndZ=0
    g64: LineSegment StartX=58.0728 StartY=-77.8102 StartZ=0 EndX=58.0728 EndY=-62.8351 EndZ=0
    g65: LineSegment StartX=61.5791 StartY=-56.9099 StartZ=0 EndX=124.814 EndY=-22.1885 EndZ=0
    g66: LineSegment StartX=120.636 StartY=-20.8076 StartZ=0 EndX=123.265 EndY=-19.3655 EndZ=0
    g67: LineSegment StartX=117.748 StartY=-15.55 StartZ=0 EndX=120.377 EndY=-14.1062 EndZ=0
    g68: LineSegment StartX=118.934 StartY=-11.4765 StartZ=0 EndX=61.5791 EndY=-42.9683 EndZ=0
    g69: LineSegment StartX=-42.9272 StartY=-103.779 StartZ=0 EndX=132.072 EndY=-103.779 EndZ=0
    g70: LineSegment StartX=42.5666 StartY=-53.4075 StartZ=0 EndX=-7.42095 EndY=-80.8542 EndZ=0
    g71: LineSegment StartX=-10.9272 StartY=-78.7794 StartZ=0 EndX=-10.9272 EndY=48.2206 EndZ=0
    g72: LineSegment StartX=2.07281 StartY=-91.7794 StartZ=0 EndX=42.0728 EndY=-91.7794 EndZ=0
    g73: LineSegment StartX=46.0728 StartY=-87.7794 StartZ=0 EndX=46.0728 EndY=-69.424 EndZ=0
    g74: LineSegment StartX=42.5666 StartY=-67.3492 StartZ=0 EndX=1.57905 EndY=-89.8542 EndZ=0
    g75: LineSegment StartX=-42.9272 StartY=-103.779 StartZ=0 EndX=-42.9272 EndY=48.2206 EndZ=0
    g76: LineSegment StartX=-17.9272 StartY=48.2206 StartZ=0 EndX=-17.9272 EndY=58.2206 EndZ=0
    g77: LineSegment StartX=-35.9272 StartY=48.2206 StartZ=0 EndX=-35.9272 EndY=52.2206 EndZ=0
    g78: LineSegment StartX=-29.9272 StartY=48.2206 StartZ=0 EndX=-29.9272 EndY=52.2206 EndZ=0
    g79: LineSegment StartX=-23.9272 StartY=48.2206 StartZ=0 EndX=-23.9272 EndY=58.2206 EndZ=0
    g80: ArcOfCircle CenterX=-32.9272 CenterY=55.2206 CenterZ=0 NormalX=0 NormalY=0 NormalZ=1 AngleXU=0 Radius=4.24264 StartAngle=5.49779 EndAngle=10.2102
    g81: ArcOfCircle CenterX=-20.9272 CenterY=61.2206 CenterZ=0 NormalX=0 NormalY=0 NormalZ=1 AngleXU=0 Radius=4.24264 StartAngle=5.49779 EndAngle=10.2102
    g82: LineSegment StartX=-17.9272 StartY=48.2206 StartZ=0 EndX=-10.9272 EndY=48.2206 EndZ=0
    g83: LineSegment StartX=-42.9272 StartY=48.2206 StartZ=0 EndX=-35.9272 EndY=48.2206 EndZ=0
    g84: LineSegment StartX=50.0728 StartY=-27.5905 StartZ=0 EndX=50.0728 EndY=-31.5905 EndZ=0
    g85: LineSegment StartX=54.0728 StartY=-27.5905 StartZ=0 EndX=54.0728 EndY=-31.5905 EndZ=0
    g86: ArcOfCircle CenterX=52.0728 CenterY=-33.5905 CenterZ=0 NormalX=0 NormalY=0 NormalZ=1 AngleXU=0 Radius=2.82843 StartAngle=2.35619 EndAngle=7.06858
    g87: LineSegment StartX=46.0728 StartY=-27.5905 StartZ=0 EndX=50.0728 EndY=-27.5905 EndZ=0
    g88: LineSegment StartX=54.0728 StartY=-27.5905 StartZ=0 EndX=58.0728 EndY=-27.5905 EndZ=0
    g89: LineSegment StartX=46.0728 StartY=-27.5905 StartZ=0 EndX=46.0728 EndY=-47.4823 EndZ=0
    g90: LineSegment StartX=58.0728 StartY=-27.5905 StartZ=0 EndX=58.0728 EndY=-40.8935 EndZ=0
    g91: LineSegment StartX=-29.9272 StartY=48.2206 StartZ=0 EndX=-23.9272 EndY=48.2206 EndZ=0
  constraints (170):
    c: Weight(g1) = 1
    c: Equal(g1,g2)
    c: Equal(g1,g3)
    c: InternalAlignment(g1,g4)
    c: InternalAlignment(g2,g4)
    c: InternalAlignment(g3,g4)
    c: InternalAlignment(g5,g4)
    c: InternalAlignment(g6,g4)
    c: Weight(g7) = 1
    c: Equal(g7,g8)
    c: Equal(g7,g9)
    c: InternalAlignment(g7,g10)
    c: InternalAlignment(g8,g10)
    c: InternalAlignment(g9,g10)
    c: InternalAlignment(g11,g10)
    c: InternalAlignment(g12,g10)
    c: Block(g4)
    c: Block(g10)
    c: Weight(g13) = 1
    c: Equal(g13,g14)
    c: Equal(g13,g15)
    c: InternalAlignment(g13,g16)
    c: InternalAlignment(g14,g16)
    c: InternalAlignment(g15,g16)
    c: InternalAlignment(g17,g16)
    c: InternalAlignment(g18,g16)
    c: Block(g16)
    c: Weight(g19) = 1
    c: Equal(g19,g20)
    c: Equal(g19,g21)
    c: InternalAlignment(g19,g22)
    c: InternalAlignment(g20,g22)
    c: InternalAlignment(g21,g22)
    c: InternalAlignment(g23,g22)
    c: InternalAlignment(g24,g22)
    c: Block(g22)
    c: Weight(g25) = 1
    c: Equal(g25,g26)
    c: Equal(g25,g27)
    c: InternalAlignment(g25,g28)
    c: InternalAlignment(g26,g28)
    c: InternalAlignment(g27,g28)
    c: InternalAlignment(g29,g28)
    c: InternalAlignment(g30,g28)
    c: Weight(g31) = 1
    c: Equal(g31,g32)
    c: Equal(g31,g33)
    c: InternalAlignment(g31,g34)
    c: InternalAlignment(g32,g34)
    c: InternalAlignment(g33,g34)
    c: InternalAlignment(g35,g34)
    c: InternalAlignment(g36,g34)
    c: Block(g34)
    c: Block(g28)
    c: Block(g37)
    c: Block(g0)
    c: Weight(g38) = 1
    c: Equal(g38,g40)
    c: InternalAlignment(g38,g41)
    c: InternalAlignment(g39,g41)
    c: InternalAlignment(g40,g41)
    c: InternalAlignment(g42,g41)
    c: InternalAlignment(g43,g41)
    c: InternalAlignment(g45,g44)
    c: InternalAlignment(g46,g44)
    c: Block(g47)
    c: Block(g44)
    c: Block(g41)
    c: Block(g48)
    c: Block(g49)
    c: Coincident(g50,g37)
    c: Coincident(g50,g0)
    c: Coincident(g51,g37)
    c: Coincident(g51,g0)
    c: Block(g51)
    c: Block(g50)
    c: Block(g52)
    c: Block(g53)
    c: Block(g54)
    c: Block(g55)
    c: Block(g56)
    c: Coincident(g57,g47)
    c: Vertical(g57)
    c: Coincident(g58,g47)
    c: Vertical(g58)
    c: Coincident(g59,g16)
    c: Coincident(g59,g58)
    c: Horizontal(g59)
    c: Coincident(g60,g16)
    c: Coincident(g60,g55)
    c: Coincident(g61,g55)
    c: Coincident(g61,g54)
    c: Coincident(g62,g54)
    c: Coincident(g62,g53)
    c: Coincident(g63,g53)
    c: Coincident(g63,g10)
    c: Coincident(g64,g10)
    c: Coincident(g64,g4)
    c: Vertical(g64)
    c: Coincident(g65,g4)
    c: Coincident(g65,g48)
    c: Coincident(g66,g49)
    c: Coincident(g66,g48)
    c: Coincident(g67,g49)
    c: Coincident(g67,g52)
    c: Coincident(g68,g52)
    c: Coincident(g68,g22)
    c: Coincident(g69,g57)
    c: Horizontal(g69)
    c: Coincident(g70,g44)
    c: Coincident(g70,g41)
    c: Coincident(g71,g41)
    c: Vertical(g71)
    c: Coincident(g72,g34)
    c: Coincident(g72,g56)
    c: Horizontal(g72)
    c: Coincident(g73,g56)
    c: Coincident(g73,g28)
    c: Vertical(g73)
    c: Coincident(g74,g28)
    c: Coincident(g74,g34)
    c: Block(g69)
    c: Coincident(g75,g69)
    c: Vertical(g75)
    c: Distance(g75) = 152
    c: Block(g71)
    c: Vertical(g76)
    c: Distance(g76) = 10
    c: Vertical(g77)
    c: Distance(g77) = 4
    c: Vertical(g78)
    c: Distance(g78) = 4
    c: Vertical(g79)
    c: Distance(g79) = 10
    c: Coincident(g80,g78)
    c: Coincident(g80,g77)
    c: Block(g80)
    c: Coincident(g81,g79)
    c: Coincident(g81,g76)
    c: Block(g81)
    c: Coincident(g82,g76)
    c: Coincident(g82,g71)
    c: Horizontal(g82)
    c: Coincident(g83,g75)
    c: Coincident(g83,g77)
    c: Horizontal(g83)
    c: Distance(g83) = 7
    c: Distance(g82) = 7
    c: Vertical(g84)
    c: Distance(g84) = 4
    c: Vertical(g85)
    c: Distance(g85) = 4
    c: Coincident(g86,g84)
    c: Coincident(g86,g85)
    c: Block(g86)
    c: Coincident(g87,g84)
    c: Horizontal(g87)
    c: Distance(g87) = 4
    c: Coincident(g88,g85)
    c: Horizontal(g88)
    c: Distance(g88) = 4
    c: Coincident(g89,g87)
    c: Coincident(g89,g44)
    c: Vertical(g89)
    c: Coincident(g90,g88)
    c: Coincident(g90,g22)
    c: Vertical(g90)
    c: Coincident(g91,g78)
    c: Coincident(g91,g79)
    c: Horizontal(g91)
FEATURE [Sketcher::SketchObject] Sketch008  label="rightSideTop"
  FullyConstrained = false
  sketch-geometry (108):
    g0: Circle CenterX=302.996 CenterY=111.695 CenterZ=0 NormalX=0 NormalY=0 NormalZ=1 AngleXU=0 Radius=1
    g1: Circle CenterX=306.073 CenterY=114.251 CenterZ=0 NormalX=0 NormalY=0 NormalZ=1 AngleXU=0 Radius=1
    g2: Circle CenterX=306.073 CenterY=110.251 CenterZ=0 NormalX=0 NormalY=0 NormalZ=1 AngleXU=0 Radius=1
    g3: BSplineCurve PolesCount=3 KnotsCount=2 Degree=2 IsPeriodic=0
    g4: GeomPoint X=302.996 Y=111.695 Z=0
    g5: GeomPoint X=306.073 Y=110.251 Z=0
    g6: Circle CenterX=306.073 CenterY=95.2763 CenterZ=0 NormalX=0 NormalY=0 NormalZ=1 AngleXU=0 Radius=1
    g7: Circle CenterX=306.073 CenterY=91.2763 CenterZ=0 NormalX=0 NormalY=0 NormalZ=1 AngleXU=0 Radius=1
    g8: Circle CenterX=302.567 CenterY=89.3511 CenterZ=0 NormalX=0 NormalY=0 NormalZ=1 AngleXU=0 Radius=1
    g9: BSplineCurve PolesCount=3 KnotsCount=2 Degree=2 IsPeriodic=0
    g10: GeomPoint X=306.073 Y=95.2763 Z=0
    g11: GeomPoint X=302.567 Y=89.3511 Z=0
    g12: LineSegment StartX=306.073 StartY=110.251 StartZ=0 EndX=306.073 EndY=95.2763 EndZ=0
    g13: Circle CenterX=302.073 CenterY=124.221 CenterZ=0 NormalX=0 NormalY=0 NormalZ=1 AngleXU=0 Radius=1
    g14: Circle CenterX=306.073 CenterY=124.221 CenterZ=0 NormalX=0 NormalY=0 NormalZ=1 AngleXU=0 Radius=1
    g15: Circle CenterX=302.996 CenterY=121.665 CenterZ=0 NormalX=0 NormalY=0 NormalZ=1 AngleXU=0 Radius=1
    g16: BSplineCurve PolesCount=3 KnotsCount=2 Degree=2 IsPeriodic=0
    g17: GeomPoint X=302.073 Y=124.221 Z=0
    g18: GeomPoint X=302.996 Y=121.665 Z=0
    g19: Circle CenterX=306.073 CenterY=73.3346 CenterZ=0 NormalX=0 NormalY=0 NormalZ=1 AngleXU=0 Radius=1
    g20: Circle CenterX=306.073 CenterY=77.3346 CenterZ=0 NormalX=0 NormalY=0 NormalZ=1 AngleXU=0 Radius=1
    g21: Circle CenterX=302.535 CenterY=75.4095 CenterZ=0 NormalX=0 NormalY=0 NormalZ=1 AngleXU=0 Radius=1
    g22: BSplineCurve PolesCount=3 KnotsCount=2 Degree=2 IsPeriodic=0
    g23: GeomPoint X=306.073 Y=73.3346 Z=0
    g24: GeomPoint X=302.535 Y=75.4095 Z=0
    g25: Circle CenterX=362.073 CenterY=124.221 CenterZ=0 NormalX=0 NormalY=0 NormalZ=1 AngleXU=0 Radius=1
    g26: Circle CenterX=366.073 CenterY=124.221 CenterZ=0 NormalX=0 NormalY=0 NormalZ=1 AngleXU=0 Radius=1
    g27: Circle CenterX=362.567 CenterY=122.294 CenterZ=0 NormalX=0 NormalY=0 NormalZ=1 AngleXU=0 Radius=1
    g28: BSplineCurve PolesCount=3 KnotsCount=2 Degree=2 IsPeriodic=0
    g29: GeomPoint X=362.073 Y=124.221 Z=0
    g30: GeomPoint X=362.567 Y=122.294 Z=0
    g31: Circle CenterX=322.073 CenterY=124.221 CenterZ=0 NormalX=0 NormalY=0 NormalZ=1 AngleXU=0 Radius=1
    g32: Circle CenterX=318.073 CenterY=124.221 CenterZ=0 NormalX=0 NormalY=0 NormalZ=1 AngleXU=0 Radius=1
    g33: Circle CenterX=318.073 CenterY=120.221 CenterZ=0 NormalX=0 NormalY=0 NormalZ=1 AngleXU=0 Radius=1
    g34: BSplineCurve PolesCount=3 KnotsCount=2 Degree=2 IsPeriodic=0
    g35: GeomPoint X=322.073 Y=124.221 Z=0
    g36: GeomPoint X=318.073 Y=120.221 Z=0
    g37: Circle CenterX=322.073 CenterY=105.865 CenterZ=0 NormalX=0 NormalY=0 NormalZ=1 AngleXU=0 Radius=1
    g38: Circle CenterX=318.073 CenterY=105.865 CenterZ=0 NormalX=0 NormalY=0 NormalZ=1 AngleXU=0 Radius=1
    g39: Circle CenterX=318.073 CenterY=109.865 CenterZ=0 NormalX=0 NormalY=0 NormalZ=1 AngleXU=0 Radius=1
    g40: BSplineCurve PolesCount=3 KnotsCount=2 Degree=2 IsPeriodic=0
    g41: GeomPoint X=322.073 Y=105.865 Z=0
    g42: GeomPoint X=318.073 Y=109.865 Z=0
    g43: Circle CenterX=336.157 CenterY=107.779 CenterZ=0 NormalX=0 NormalY=0 NormalZ=1 AngleXU=0 Radius=1
    g44: Circle CenterX=332.651 CenterY=105.853 CenterZ=0 NormalX=0 NormalY=0 NormalZ=1 AngleXU=0 Radius=1
    g45: Circle CenterX=328.643 CenterY=105.865 CenterZ=0 NormalX=0 NormalY=0 NormalZ=1 AngleXU=0 Radius=1
    g46: BSplineCurve PolesCount=3 KnotsCount=2 Degree=2 IsPeriodic=0
    g47: GeomPoint X=336.157 Y=107.779 Z=0
    g48: GeomPoint X=328.643 Y=105.865 Z=0
    g49: Circle CenterX=322.073 CenterY=76.4095 CenterZ=0 NormalX=0 NormalY=0 NormalZ=1 AngleXU=0 Radius=4
    g50: BSplineCurve PolesCount=3 KnotsCount=2 Degree=2 IsPeriodic=0
    g51: GeomPoint X=318.073 Y=72.4095 Z=0
    g52: GeomPoint X=322.073 Y=76.4095 Z=0
    g53: Circle CenterX=375.073 CenterY=72.4095 CenterZ=0 NormalX=0 NormalY=0 NormalZ=1 AngleXU=0 Radius=1
    g54: Circle CenterX=375.073 CenterY=76.4095 CenterZ=0 NormalX=0 NormalY=0 NormalZ=1 AngleXU=0 Radius=1
    g55: Circle CenterX=371.073 CenterY=76.4095 CenterZ=0 NormalX=0 NormalY=0 NormalZ=1 AngleXU=0 Radius=1
    g56: BSplineCurve PolesCount=3 KnotsCount=2 Degree=2 IsPeriodic=0
    g57: GeomPoint X=375.073 Y=72.4095 Z=0
    g58: GeomPoint X=371.073 Y=76.4095 Z=0
    g59: LineSegment StartX=322.073 StartY=76.4095 StartZ=0 EndX=371.073 EndY=76.4095 EndZ=0
    g60: Circle CenterX=232.072 CenterY=133.221 CenterZ=0 NormalX=0 NormalY=0 NormalZ=1 AngleXU=0 Radius=1
    g61: Circle CenterX=226.072 CenterY=136.221 CenterZ=0 NormalX=0 NormalY=0 NormalZ=1 AngleXU=0 Radius=1
    g62: Circle CenterX=226.072 CenterY=124.221 CenterZ=0 NormalX=0 NormalY=0 NormalZ=1 AngleXU=0 Radius=1
    g63: Circle CenterX=232.072 CenterY=127.221 CenterZ=0 NormalX=0 NormalY=0 NormalZ=1 AngleXU=0 Radius=1
    g64: BSplineCurve PolesCount=5 KnotsCount=3 Degree=3 IsPeriodic=0
    g65: GeomPoint X=232.072 Y=133.221 Z=0
    g66: GeomPoint X=223.072 Y=130.221 Z=0
    g67: GeomPoint X=232.072 Y=127.221 Z=0
    g68: LineSegment StartX=240.687 StartY=51.8263 StartZ=0 EndX=243.317 EndY=53.2701 EndZ=0
    g69: LineSegment StartX=243.575 StartY=46.5669 StartZ=0 EndX=246.205 EndY=48.0108 EndZ=0
    g70: ArcOfCircle CenterX=247.391 CenterY=52.0843 CenterZ=0 NormalX=0 NormalY=0 NormalZ=1 AngleXU=0 Radius=4.24264 StartAngle=4.42912 EndAngle=9.14151
    g71: LineSegment StartX=243.475 StartY=65.4951 StartZ=0 EndX=245.073 EndY=63.5726 EndZ=0
    g72: LineSegment StartX=243.575 StartY=46.5669 StartZ=0 EndX=245.072 EndY=43.8408 EndZ=0
    g73: LineSegment StartX=245.072 StartY=43.8408 StartZ=0 EndX=302.535 EndY=75.4095 EndZ=0
    g74: LineSegment StartX=239.192 StartY=54.5542 StartZ=0 EndX=302.567 EndY=89.3511 EndZ=0
    g75: LineSegment StartX=232.072 StartY=127.221 StartZ=0 EndX=232.072 EndY=124.221 EndZ=0
    g76: LineSegment StartX=232.072 StartY=136.221 StartZ=0 EndX=232.072 EndY=133.221 EndZ=0
    g77: LineSegment StartX=232.072 StartY=136.221 StartZ=0 EndX=407.073 EndY=136.221 EndZ=0
    g78: LineSegment StartX=322.073 StartY=124.221 StartZ=0 EndX=362.073 EndY=124.221 EndZ=0
    g79: LineSegment StartX=362.567 StartY=122.294 StartZ=0 EndX=336.157 EndY=107.779 EndZ=0
    g80: LineSegment StartX=322.073 StartY=105.865 StartZ=0 EndX=328.643 EndY=105.865 EndZ=0
    g81: LineSegment StartX=318.073 StartY=120.221 StartZ=0 EndX=318.073 EndY=109.865 EndZ=0
    g82: LineSegment StartX=232.072 StartY=124.221 StartZ=0 EndX=302.073 EndY=124.221 EndZ=0
    g83: LineSegment StartX=302.996 StartY=121.665 StartZ=0 EndX=240.171 EndY=69.471 EndZ=0
    g84: LineSegment StartX=240.171 StartY=69.471 StartZ=0 EndX=241.711 EndY=67.6177 EndZ=0
    g85: LineSegment StartX=241.711 StartY=67.6177 StartZ=0 EndX=246.787 EndY=71.8365 EndZ=0
    g86: LineSegment StartX=246.787 StartY=71.8365 StartZ=0 EndX=248.551 EndY=69.712 EndZ=0
    g87: LineSegment StartX=248.551 StartY=69.712 StartZ=0 EndX=243.475 EndY=65.4951 EndZ=0
    g88: LineSegment StartX=245.073 StartY=63.5726 StartZ=0 EndX=302.996 EndY=111.695 EndZ=0
    g89: LineSegment StartX=239.192 StartY=54.5542 StartZ=0 EndX=240.687 EndY=51.8263 EndZ=0
    g90: LineSegment StartX=375.073 StartY=48.2206 StartZ=0 EndX=382.073 EndY=48.2206 EndZ=0
    g91: LineSegment StartX=407.073 StartY=48.2206 StartZ=0 EndX=400.073 EndY=48.2206 EndZ=0
    g92: LineSegment StartX=394.073 StartY=48.2206 StartZ=0 EndX=394.073 EndY=52.2206 EndZ=0
    g93: LineSegment StartX=388.073 StartY=48.2206 StartZ=0 EndX=388.073 EndY=58.2206 EndZ=0
    g94: ArcOfCircle CenterX=385.073 CenterY=61.2206 CenterZ=0 NormalX=0 NormalY=0 NormalZ=1 AngleXU=0 Radius=4.24264 StartAngle=5.49779 EndAngle=10.2102
    g95: ArcOfCircle CenterX=397.073 CenterY=55.2206 CenterZ=0 NormalX=0 NormalY=0 NormalZ=1 AngleXU=0 Radius=4.24264 StartAngle=5.49779 EndAngle=10.2102
    g96: LineSegment StartX=382.073 StartY=58.2206 StartZ=0 EndX=382.073 EndY=48.2206 EndZ=0
    g97: LineSegment StartX=400.073 StartY=52.2206 StartZ=0 EndX=400.073 EndY=48.2206 EndZ=0
    g98: LineSegment StartX=394.073 StartY=48.2206 StartZ=0 EndX=388.073 EndY=48.2206 EndZ=0
    g99: LineSegment StartX=306.073 StartY=-27.5935 StartZ=0 EndX=310.073 EndY=-27.5935 EndZ=0
    g100: LineSegment StartX=318.073 StartY=-27.5935 StartZ=0 EndX=314.073 EndY=-27.5935 EndZ=0
    g101: LineSegment StartX=310.073 StartY=-27.5935 StartZ=0 EndX=310.073 EndY=-31.5935 EndZ=0
    g102: LineSegment StartX=314.073 StartY=-27.5935 StartZ=0 EndX=314.073 EndY=-31.5935 EndZ=0
    g103: ArcOfCircle CenterX=312.073 CenterY=-33.5935 CenterZ=0 NormalX=0 NormalY=0 NormalZ=1 AngleXU=0 Radius=2.82843 StartAngle=2.35619 EndAngle=7.06858
    g104: LineSegment StartX=375.073 StartY=72.4095 StartZ=0 EndX=375.073 EndY=48.2206 EndZ=0
    g105: LineSegment StartX=407.073 StartY=48.2206 StartZ=0 EndX=407.073 EndY=136.221 EndZ=0
    g106: LineSegment StartX=318.073 StartY=-27.5935 StartZ=0 EndX=318.073 EndY=72.4095 EndZ=0
    g107: LineSegment StartX=306.073 StartY=73.3346 StartZ=0 EndX=306.073 EndY=-27.5935 EndZ=0
  constraints (136):
    c: Weight(g0) = 1
    c: Equal(g0,g1)
    c: Equal(g0,g2)
    c: InternalAlignment(g0,g3)
    c: InternalAlignment(g1,g3)
    c: InternalAlignment(g2,g3)
    c: InternalAlignment(g4,g3)
    c: InternalAlignment(g5,g3)
    c: Weight(g6) = 1
    c: Equal(g6,g7)
    c: Equal(g6,g8)
    c: InternalAlignment(g6,g9)
    c: InternalAlignment(g7,g9)
    c: InternalAlignment(g8,g9)
    c: InternalAlignment(g10,g9)
    c: InternalAlignment(g11,g9)
    c: Block(g3)
    c: Block(g9)
    c: Coincident(g12,g3)
    c: Coincident(g12,g9)
    c: Vertical(g12)
    c: Weight(g13) = 1
    c: Equal(g13,g14)
    c: Equal(g13,g15)
    c: InternalAlignment(g14,g16)
    c: InternalAlignment(g15,g16)
    c: InternalAlignment(g17,g16)
    c: InternalAlignment(g18,g16)
    c: Block(g71)
    c: Block(g72)
    c: Coincident(g73,g72)
    c: Coincident(g73,g22)
    c: Block(g73)
    c: Coincident(g70,g69)
    c: Coincident(g70,g68)
    c: Coincident(g74,g9)
    c: Block(g74)
    c: Distance(g71) = 2.5
    c: Block(g64)
    c: Block(g46)
    c: Block(g59)
    c: Coincident(g75,g64)
    c: Vertical(g75)
    c: Coincident(g76,g64)
    c: Vertical(g76)
    c: Coincident(g77,g76)
    c: Horizontal(g77)
    c: Coincident(g78,g34)
    c: Coincident(g78,g28)
    c: Horizontal(g78)
    c: Coincident(g79,g28)
    c: Coincident(g79,g46)
    c: Coincident(g80,g40)
    c: Coincident(g80,g46)
    c: Horizontal(g80)
    c: Coincident(g81,g34)
    c: Coincident(g81,g40)
    c: Vertical(g81)
    c: Block(g34)
    c: Block(g40)
    c: Block(g28)
    c: Coincident(g82,g75)
    c: Coincident(g82,g16)
    c: Horizontal(g82)
    c: Coincident(g83,g16)
    c: Block(g82)
    c: Block(g83)
    c: Block(g16)
    c: Coincident(g84,g83)
    c: Block(g84)
    c: Coincident(g85,g84)
    c: Block(g85)
    c: Coincident(g86,g85)
    c: Coincident(g87,g86)
    c: Coincident(g87,g71)
    c: Block(g87)
    c: Coincident(g88,g71)
    c: Coincident(g88,g3)
    c: Block(g88)
    c: Coincident(g89,g74)
    c: Coincident(g89,g68)
    c: Block(g70)
    c: Block(g68)
    c: Block(g69)
    c: Block(g22)
    c: Block(g50)
    c: Block(g56)
    c: Horizontal(g90)
    c: Distance(g90) = 7
    c: Horizontal(g91)
    c: Distance(g91) = 7
    c: Vertical(g92)
    c: Distance(g92) = 4
    c: Vertical(g93)
    c: Distance(g93) = 10
    c: Coincident(g94,g93)
    c: Coincident(g95,g92)
    c: Block(g95)
    c: Block(g94)
    c: Coincident(g96,g94)
    c: Coincident(g96,g90)
    c: Vertical(g96)
    c: Coincident(g97,g95)
    c: Coincident(g97,g91)
    c: Vertical(g97)
    c: Coincident(g98,g92)
    c: Coincident(g98,g93)
    c: Horizontal(g98)
    c: Horizontal(g99)
    c: Distance(g99) = 4
    c: Horizontal(g100)
    c: Distance(g100) = 4
    c: Coincident(g101,g99)
    c: Vertical(g101)
    c: Coincident(g102,g100)
    c: Vertical(g102)
    c: Distance(g101) = 4
    c: Distance(g102) = 4
    c: Coincident(g103,g101)
    c: Coincident(g103,g102)
    c: Block(g103)
    c: Coincident(g104,g56)
    c: Coincident(g104,g90)
    c: Vertical(g104)
    c: Block(g104)
    c: Coincident(g105,g91)
    c: Coincident(g105,g77)
    c: Vertical(g105)
    c: Block(g77)
    c: Block(g105)
    c: Coincident(g106,g100)
    c: Coincident(g106,g50)
    c: Vertical(g106)
    c: Coincident(g107,g22)
    c: Coincident(g107,g99)
    c: Vertical(g107)
FEATURE [Sketcher::SketchObject] Sketch009  label="middleBottom"
  FullyConstrained = true
  sketch-geometry (109):
    g0: Circle CenterX=175.022 CenterY=5.37834 CenterZ=0 NormalX=0 NormalY=0 NormalZ=1 AngleXU=0 Radius=1
    g1: Circle CenterX=179.022 CenterY=7.57463 CenterZ=0 NormalX=0 NormalY=0 NormalZ=1 AngleXU=0 Radius=1
    g2: Circle CenterX=179.022 CenterY=5.34704 CenterZ=0 NormalX=0 NormalY=0 NormalZ=1 AngleXU=0 Radius=1
    g3: BSplineCurve PolesCount=3 KnotsCount=2 Degree=2 IsPeriodic=0
    g4: GeomPoint X=175.022 Y=5.37834 Z=0
    g5: GeomPoint X=179.022 Y=5.34704 Z=0
    g6: Circle CenterX=189.124 CenterY=5.37834 CenterZ=0 NormalX=0 NormalY=0 NormalZ=1 AngleXU=0 Radius=1
    g7: Circle CenterX=185.124 CenterY=7.57463 CenterZ=0 NormalX=0 NormalY=0 NormalZ=1 AngleXU=0 Radius=1
    g8: Circle CenterX=185.124 CenterY=5.34704 CenterZ=0 NormalX=0 NormalY=0 NormalZ=1 AngleXU=0 Radius=1
    g9: BSplineCurve PolesCount=3 KnotsCount=2 Degree=2 IsPeriodic=0
    g10: GeomPoint X=189.124 Y=5.37834 Z=0
    g11: GeomPoint X=185.124 Y=5.34704 Z=0
    g12: Circle CenterX=224.513 CenterY=-14.0532 CenterZ=0 NormalX=0 NormalY=0 NormalZ=1 AngleXU=0 Radius=1
    g13: Circle CenterX=236.584 CenterY=-24.2775 CenterZ=0 NormalX=0 NormalY=0 NormalZ=1 AngleXU=0 Radius=1
    g14: BSplineCurve PolesCount=3 KnotsCount=2 Degree=2 IsPeriodic=0
    g15: GeomPoint X=236.584 Y=-24.2775 Z=0
    g16: Circle CenterX=125.607 CenterY=-21.7539 CenterZ=0 NormalX=0 NormalY=0 NormalZ=1 AngleXU=0 Radius=1
    g17: Circle CenterX=139.632 CenterY=-14.0532 CenterZ=0 NormalX=0 NormalY=0 NormalZ=1 AngleXU=0 Radius=1
    g18: Circle CenterX=127.325 CenterY=-24.2775 CenterZ=0 NormalX=0 NormalY=0 NormalZ=1 AngleXU=0 Radius=1
    g19: BSplineCurve PolesCount=3 KnotsCount=2 Degree=2 IsPeriodic=0
    g20: GeomPoint X=125.607 Y=-21.7539 Z=0
    g21: GeomPoint X=127.325 Y=-24.2775 Z=0
    g22: Circle CenterX=179.022 CenterY=-85.8163 CenterZ=0 NormalX=0 NormalY=0 NormalZ=1 AngleXU=0 Radius=1
    g23: Circle CenterX=179.022 CenterY=-91.7794 CenterZ=0 NormalX=0 NormalY=0 NormalZ=1 AngleXU=0 Radius=1
    g24: Circle CenterX=171.895 CenterY=-91.8014 CenterZ=0 NormalX=0 NormalY=0 NormalZ=1 AngleXU=0 Radius=1
    g25: BSplineCurve PolesCount=3 KnotsCount=2 Degree=2 IsPeriodic=0
    g26: GeomPoint X=179.022 Y=-85.8163 Z=0
    g27: GeomPoint X=171.895 Y=-91.8014 Z=0
    g28: Circle CenterX=185.124 CenterY=-86.2028 CenterZ=0 NormalX=0 NormalY=0 NormalZ=1 AngleXU=0 Radius=1
    g29: Circle CenterX=185.124 CenterY=-91.7794 CenterZ=0 NormalX=0 NormalY=0 NormalZ=1 AngleXU=0 Radius=1
    g30: Circle CenterX=191.747 CenterY=-91.7794 CenterZ=0 NormalX=0 NormalY=0 NormalZ=1 AngleXU=0 Radius=1
    g31: BSplineCurve PolesCount=3 KnotsCount=2 Degree=2 IsPeriodic=0
    g32: GeomPoint X=185.124 Y=-86.2028 Z=0
    g33: GeomPoint X=191.747 Y=-91.7794 Z=0
    g34: BSplineCurve PolesCount=5 KnotsCount=3 Degree=3 IsPeriodic=0
    g35: LineSegment StartX=132.072 StartY=-100.779 StartZ=0 EndX=132.072 EndY=-103.779 EndZ=0
    g36: GeomPoint X=232.072 Y=-94.7794 Z=0
    g37: GeomPoint X=223.072 Y=-97.7794 Z=0
    g38: Circle CenterX=232.072 CenterY=-94.7794 CenterZ=0 NormalX=0 NormalY=0 NormalZ=1 AngleXU=0 Radius=1
    g39: Circle CenterX=232.072 CenterY=-100.779 CenterZ=0 NormalX=0 NormalY=0 NormalZ=1 AngleXU=0 Radius=1
    g40: BSplineCurve PolesCount=5 KnotsCount=3 Degree=3 IsPeriodic=0
    g41: GeomPoint X=232.072 Y=-100.779 Z=0
    g42: LineSegment StartX=123.656 StartY=-37.1092 StartZ=0 EndX=122.136 EndY=-35.2714 EndZ=0
    g43: LineSegment StartX=117.05 StartY=-39.4781 StartZ=0 EndX=115.291 EndY=-37.3514 EndZ=0
    g44: LineSegment StartX=120.377 StartY=-33.1447 StartZ=0 EndX=118.86 EndY=-31.3104 EndZ=0
    g45: ArcOfCircle CenterX=116.562 CenterY=-19.6236 CenterZ=0 NormalX=0 NormalY=0 NormalZ=1 AngleXU=0 Radius=4.24264 StartAngle=1.28753 EndAngle=5.99992
    g46: LineSegment StartX=240.266 StartY=-37.1092 StartZ=0 EndX=189.124 EndY=5.37834 EndZ=0
    g47: LineSegment StartX=191.747 StartY=-91.7794 StartZ=0 EndX=232.072 EndY=-91.7794 EndZ=0
    g48: LineSegment StartX=232.072 StartY=-91.7794 StartZ=0 EndX=232.072 EndY=-94.7794 EndZ=0
    g49: LineSegment StartX=232.072 StartY=-100.779 StartZ=0 EndX=232.072 EndY=-103.779 EndZ=0
    g50: LineSegment StartX=132.072 StartY=-103.779 StartZ=0 EndX=232.072 EndY=-103.779 EndZ=0
    g51: LineSegment StartX=132.072 StartY=-91.8014 StartZ=0 EndX=132.072 EndY=-94.7791 EndZ=0
    g52: LineSegment StartX=132.072 StartY=-91.8014 StartZ=0 EndX=171.895 EndY=-91.8014 EndZ=0
    g53: LineSegment StartX=179.022 StartY=-85.8163 StartZ=0 EndX=179.022 EndY=5.34704 EndZ=0
    g54: LineSegment StartX=175.022 StartY=5.37834 StartZ=0 EndX=123.656 EndY=-37.1092 EndZ=0
    g55: LineSegment StartX=185.124 StartY=5.34704 StartZ=0 EndX=185.124 EndY=-86.2028 EndZ=0
    g56: LineSegment StartX=122.136 StartY=-35.2714 StartZ=0 EndX=117.05 EndY=-39.4781 EndZ=0
    g57: LineSegment StartX=115.291 StartY=-37.3514 StartZ=0 EndX=120.377 EndY=-33.1447 EndZ=0
    g58: LineSegment StartX=118.86 StartY=-31.3104 StartZ=0 EndX=127.325 EndY=-24.2775 EndZ=0
    g59: LineSegment StartX=125.607 StartY=-21.7539 StartZ=0 EndX=124.815 EndY=-22.1887 EndZ=0
    g60: LineSegment StartX=123.265 StartY=-19.3655 StartZ=0 EndX=124.815 EndY=-22.1887 EndZ=0
    g61: LineSegment StartX=120.636 StartY=-20.8094 StartZ=0 EndX=123.265 EndY=-19.3655 EndZ=0
    g62: LineSegment StartX=117.748 StartY=-15.55 StartZ=0 EndX=120.377 EndY=-14.1062 EndZ=0
    g63: LineSegment StartX=120.377 StartY=-14.1062 StartZ=0 EndX=118.934 EndY=-11.4765 EndZ=0
    g64: LineSegment StartX=236.584 StartY=-24.2775 StartZ=0 EndX=245.072 EndY=-31.3037 EndZ=0
    g65: LineSegment StartX=245.072 StartY=-31.3037 StartZ=0 EndX=243.535 EndY=-33.1602 EndZ=0
    g66: LineSegment StartX=243.535 StartY=-33.1602 StartZ=0 EndX=248.619 EndY=-37.3688 EndZ=0
    g67: LineSegment StartX=248.619 StartY=-37.3688 StartZ=0 EndX=246.855 EndY=-39.5064 EndZ=0
    g68: LineSegment StartX=246.855 StartY=-39.5064 StartZ=0 EndX=241.778 EndY=-35.2889 EndZ=0
    g69: LineSegment StartX=241.778 StartY=-35.2889 StartZ=0 EndX=240.266 EndY=-37.1092 EndZ=0
    g70: LineSegment StartX=243.628 StartY=-14.0323 StartZ=0 EndX=246.258 EndY=-15.476 EndZ=0
    g71: LineSegment StartX=240.741 StartY=-19.2917 StartZ=0 EndX=243.37 EndY=-20.7355 EndZ=0
    g72: ArcOfCircle CenterX=247.444 CenterY=-19.5496 CenterZ=0 NormalX=0 NormalY=0 NormalZ=1 AngleXU=0 Radius=4.24264 StartAngle=3.4249 EndAngle=8.13729
    g73: LineSegment StartX=240.741 StartY=-19.2917 StartZ=0 EndX=239.201 EndY=-22.0968 EndZ=0
    g74: LineSegment StartX=238.538 StartY=-21.7516 StartZ=0 EndX=239.201 EndY=-22.0968 EndZ=0
    g75: LineSegment StartX=245.072 StartY=-11.4025 StartZ=0 EndX=243.628 EndY=-14.0323 EndZ=0
    g76-g91: Circle x16 (B-spline internal-alignment scaffolding for g92; pole/knot coordinates omitted)
    g92: BSplineCurve PolesCount=16 KnotsCount=14 Degree=3 IsPeriodic=0
    g93-g106: GeomPoint x14 (B-spline internal-alignment scaffolding for g92; pole/knot coordinates omitted)
    g107: LineSegment StartX=165.871 StartY=14.2956 StartZ=0 EndX=118.934 EndY=-11.4765 EndZ=0
    g108: LineSegment StartX=198.264 StartY=14.2963 StartZ=0 EndX=245.072 EndY=-11.4025 EndZ=0
  constraints (146):
    c: Weight(g0) = 1
    c: Equal(g0,g1)
    c: Equal(g0,g2)
    c: InternalAlignment(g0,g3)
    c: InternalAlignment(g1,g3)
    c: InternalAlignment(g2,g3)
    c: InternalAlignment(g4,g3)
    c: InternalAlignment(g5,g3)
    c: Weight(g6) = 1
    c: Equal(g6,g7)
    c: Equal(g6,g8)
    c: InternalAlignment(g6,g9)
    c: InternalAlignment(g7,g9)
    c: InternalAlignment(g8,g9)
    c: InternalAlignment(g10,g9)
    c: InternalAlignment(g11,g9)
    c: Block(g9)
    c: Block(g3)
    c: InternalAlignment(g12,g14)
    c: InternalAlignment(g13,g14)
    c: InternalAlignment(g15,g14)
    c: Block(g14)
    c: Weight(g16) = 1
    c: Equal(g16,g17)
    c: Equal(g16,g18)
    c: InternalAlignment(g16,g19)
    c: InternalAlignment(g17,g19)
    c: InternalAlignment(g18,g19)
    c: InternalAlignment(g20,g19)
    c: InternalAlignment(g21,g19)
    c: Block(g19)
    c: Weight(g22) = 1
    c: Equal(g22,g23)
    c: Equal(g22,g24)
    c: InternalAlignment(g22,g25)
    c: InternalAlignment(g23,g25)
    c: InternalAlignment(g24,g25)
    c: InternalAlignment(g26,g25)
    c: InternalAlignment(g27,g25)
    c: Weight(g28) = 1
    c: Equal(g28,g29)
    c: Equal(g28,g30)
    c: InternalAlignment(g28,g31)
    c: InternalAlignment(g29,g31)
    c: InternalAlignment(g30,g31)
    c: InternalAlignment(g32,g31)
    c: InternalAlignment(g33,g31)
    c: Block(g31)
    c: Block(g25)
    c: Block(g34)
    c: Coincident(g35,g34)
    c: Vertical(g35)
    c: Block(g35)
    c: Equal(g38,g39)
    c: InternalAlignment(g38,g40)
    c: InternalAlignment(g39,g40)
    c: InternalAlignment(g36,g40)
    c: InternalAlignment(g37,g40)
    c: InternalAlignment(g41,g40)
    c: Block(g40)
    c: Distance(g42) = 2.385
    c: Distance(g43) = 2.76
    c: Parallel(g42,g44)
    c: Block(g45)
    c: Coincident(g46,g9)
    c: Coincident(g47,g31)
    c: Horizontal(g47)
    c: Block(g47)
    c: Coincident(g48,g47)
    c: Coincident(g48,g40)
    c: Vertical(g48)
    c: Block(g48)
    c: Coincident(g49,g40)
    c: Vertical(g49)
    c: Block(g49)
    c: Coincident(g50,g35)
    c: Coincident(g50,g49)
    c: Horizontal(g50)
    c: Block(g50)
    c: Coincident(g51,g34)
    c: Vertical(g51)
    c: Coincident(g52,g51)
    c: Coincident(g52,g25)
    c: Horizontal(g52)
    c: Coincident(g53,g25)
    c: Coincident(g53,g3)
    c: Vertical(g53)
    c: Coincident(g54,g3)
    c: Coincident(g54,g42)
    c: Coincident(g55,g9)
    c: Coincident(g55,g31)
    c: Vertical(g55)
    c: Block(g42)
    c: Coincident(g56,g42)
    c: Coincident(g56,g43)
    c: Coincident(g57,g43)
    c: Coincident(g57,g44)
    c: Block(g57)
    c: Block(g56)
    c: Coincident(g58,g44)
    c: Coincident(g58,g19)
    c: Block(g58)
    c: Coincident(g59,g19)
    c: Block(g59)
    c: Coincident(g60,g59)
    c: Block(g60)
    c: Coincident(g61,g45)
    c: Coincident(g61,g60)
    c: Coincident(g62,g45)
    c: Coincident(g63,g62)
    c: Block(g63)
    c: Coincident(g64,g14)
    c: Block(g64)
    c: Coincident(g65,g64)
    c: Coincident(g66,g65)
    c: Coincident(g67,g66)
    c: Coincident(g68,g67)
    c: Coincident(g69,g68)
    c: Coincident(g69,g46)
    c: Block(g46)
    c: Block(g68)
    c: Block(g66)
    c: Distance(g70) = 3
    c: Distance(g71) = 3
    c: Coincident(g72,g70)
    c: Coincident(g72,g71)
    c: Block(g72)
    c: Coincident(g73,g71)
    c: Distance(g73) = 3.2
    c: Coincident(g74,g14)
    c: Coincident(g74,g73)
    c: Coincident(g75,g70)
    c: Block(g75)
    c: Block(g73)
    c: Distance(g63) = 3
    c: Distance(g60) = 3.22077
    c: Weight(g76) = 1
    c: Equal(g76, g77-g91) x15
    c: InternalAlignment(g76-g91 -> g92) x16
    c: InternalAlignment(g93-g106 -> g92) x14
    c: Coincident(g107,g92)
    c: Coincident(g107,g63)
    c: Block(g107)
    c: Block(g92)
    c: Coincident(g108,g92)
    c: Coincident(g108,g75)
FEATURE [Sketcher::SketchObject] Sketch010  label="legBottomBack"
  FullyConstrained = true
  MapMode = 4
  Placement = pos=(0,0,0) rot=(0.57735,0.57735,0.57735;2.0944rad)
  sketch-geometry (76):
    g0: Circle CenterX=-17.0256 CenterY=-190.268 CenterZ=0 NormalX=0 NormalY=0 NormalZ=1 AngleXU=0 Radius=10.5072
    g1: Circle CenterX=-37.7758 CenterY=-187.672 CenterZ=0 NormalX=0 NormalY=0 NormalZ=1 AngleXU=0 Radius=5.64388
    g2: Circle CenterX=-51.4606 CenterY=-185.091 CenterZ=0 NormalX=0 NormalY=0 NormalZ=1 AngleXU=0 Radius=3.01653
    g3: Circle CenterX=-60.4835 CenterY=-182.688 CenterZ=0 NormalX=0 NormalY=0 NormalZ=1 AngleXU=0 Radius=2.12826
    g4: Circle CenterX=-3.29005 CenterY=-177.662 CenterZ=0 NormalX=0 NormalY=0 NormalZ=1 AngleXU=0 Radius=3.26661
    g5: ArcOfCircle CenterX=11.0205 CenterY=-198.019 CenterZ=0 NormalX=0 NormalY=0 NormalZ=1 AngleXU=0 Radius=13 StartAngle=2.78068 EndAngle=5.92131
    g6: LineSegment StartX=5.08312 StartY=-176.581 StartZ=0 EndX=-1.14188 EndY=-193.429 EndZ=0
    g7: ArcOfCircle CenterX=17.2475 CenterY=-181.166 CenterZ=0 NormalX=0 NormalY=0 NormalZ=1 AngleXU=0 Radius=13 StartAngle=1.21042 EndAngle=2.78109
    g8: LineSegment StartX=38.8952 StartY=-231.233 StartZ=0 EndX=39.9512 EndY=-228.425 EndZ=0
    g9: ArcOfCircle CenterX=46.9911 CenterY=-209.705 CenterZ=0 NormalX=0 NormalY=0 NormalZ=1 AngleXU=0 Radius=20 StartAngle=2.78766 EndAngle=4.35269
    g10: LineSegment StartX=23.7323 StartY=-126.969 StartZ=0 EndX=17.4091 EndY=-143.817 EndZ=0
    g11: ArcOfCircle CenterX=29.5716 CenterY=-148.408 CenterZ=0 NormalX=0 NormalY=0 NormalZ=1 AngleXU=0 Radius=13 StartAngle=2.78068 EndAngle=4.35262
    g12: ArcOfCircle CenterX=35.8967 CenterY=-131.555 CenterZ=0 NormalX=0 NormalY=0 NormalZ=1 AngleXU=0 Radius=13 StartAngle=1.21584 EndAngle=2.78109
    g13: ArcOfCircle CenterX=48.1805 CenterY=-98.7782 CenterZ=0 NormalX=0 NormalY=0 NormalZ=1 AngleXU=0 Radius=13 StartAngle=2.78068 EndAngle=4.35005
    g14: LineSegment StartX=42.354 StartY=-77.3391 StartZ=0 EndX=36.018 EndY=-94.1875 EndZ=0
    g15: ArcOfCircle CenterX=54.5183 CenterY=-81.9247 CenterZ=0 NormalX=0 NormalY=0 NormalZ=1 AngleXU=0 Radius=13 StartAngle=2.42113 EndAngle=2.78109
    g16: ArcOfCircle CenterX=20.184 CenterY=-217.506 CenterZ=0 NormalX=0 NormalY=0 NormalZ=1 AngleXU=0 Radius=3.81084 StartAngle=1.88136 EndAngle=6.80465
    g17: LineSegment StartX=38.4753 StartY=-115.966 StartZ=0 EndX=41.2852 EndY=-117.017 EndZ=0
    g18: ArcOfCircle CenterX=36.3663 CenterY=-113.042 CenterZ=0 NormalX=0 NormalY=0 NormalZ=1 AngleXU=0 Radius=3.60555 StartAngle=0.230024 EndAngle=5.3372
    g19: LineSegment StartX=39.8769 StartY=-112.22 StartZ=0 EndX=42.6867 EndY=-113.271 EndZ=0
    g20: LineSegment StartX=19.9036 StartY=-165.61 StartZ=0 EndX=22.7134 EndY=-166.661 EndZ=0
    g21: ArcOfCircle CenterX=17.7945 CenterY=-162.686 CenterZ=0 NormalX=0 NormalY=0 NormalZ=1 AngleXU=0 Radius=3.60555 StartAngle=0.230024 EndAngle=5.3372
    g22: LineSegment StartX=21.3051 StartY=-161.864 StartZ=0 EndX=24.1149 EndY=-162.915 EndZ=0
    g23: LineSegment StartX=41.085 StartY=-66.3176 StartZ=0 EndX=46.0385 EndY=-62.5254 EndZ=0
    g24: LineSegment StartX=48.9563 StartY=-66.3367 StartZ=0 EndX=44.7488 EndY=-73.3482 EndZ=0
    g25: ArcOfCircle CenterX=49.8795 CenterY=-62.6074 CenterZ=0 NormalX=0 NormalY=0 NormalZ=1 AngleXU=0 Radius=3.84187 StartAngle=4.46973 EndAngle=9.40343
    g26: LineSegment StartX=43.5724 StartY=-110.934 StartZ=0 EndX=42.6867 EndY=-113.271 EndZ=0
    g27: LineSegment StartX=40.4148 StartY=-119.365 StartZ=0 EndX=41.2852 EndY=-117.017 EndZ=0
    g28: LineSegment StartX=21.8316 StartY=-169.001 StartZ=0 EndX=22.7134 EndY=-166.661 EndZ=0
    g29: LineSegment StartX=24.9948 StartY=-160.575 StartZ=0 EndX=24.1149 EndY=-162.915 EndZ=0
    g30: LineSegment StartX=23.1786 StartY=-202.622 StartZ=0 EndX=19.0195 EndY=-213.878 EndZ=0
    g31: LineSegment StartX=28.2308 StartY=-202.773 StartZ=0 EndX=23.4884 EndY=-215.608 EndZ=0
    g32: LineSegment StartX=-76.2249 StartY=-179.393 StartZ=0 EndX=-72.8553 EndY=-180.66 EndZ=0
    g33: ArcOfCircle CenterX=-71.1257 CenterY=-183.448 CenterZ=0 NormalX=0 NormalY=0 NormalZ=1 AngleXU=0 Radius=3.28025 StartAngle=3.43759 EndAngle=8.40938
    g34: LineSegment StartX=-79.0409 StartY=-186.881 StartZ=0 EndX=38.8952 EndY=-231.233 EndZ=0
    g35-g53: Circle x19 (B-spline internal-alignment scaffolding for g54; pole/knot coordinates omitted)
    g54: BSplineCurve PolesCount=19 KnotsCount=17 Degree=3 IsPeriodic=0
    g55-g71: GeomPoint x17 (B-spline internal-alignment scaffolding for g54; pole/knot coordinates omitted)
    g72: LineSegment StartX=-74.2633 StartY=-184.404 StartZ=0 EndX=-77.6329 EndY=-183.137 EndZ=0
    g73: LineSegment StartX=-79.0409 StartY=-186.881 StartZ=0 EndX=-77.6329 EndY=-183.137 EndZ=0
    g74: LineSegment StartX=8.65492 StartY=-152.553 StartZ=0 EndX=41.085 EndY=-66.3176 EndZ=0
    g75: LineSegment StartX=-74.4658 StartY=-174.715 StartZ=0 EndX=-76.2249 EndY=-179.393 EndZ=0
  constraints (76):
    c: Block(g5)
    c: Block(g7)
    c: Block(g0)
    c: Block(g4)
    c: Block(g1)
    c: Block(g2)
    c: Block(g3)
    c: Block(g9)
    c: Coincident(g8,g9)
    c: Block(g8)
    c: Coincident(g6,g7)
    c: Coincident(g6,g5)
    c: Block(g11)
    c: Block(g12)
    c: Coincident(g10,g12)
    c: Coincident(g10,g11)
    c: Block(g13)
    c: Block(g15)
    c: Coincident(g14,g15)
    c: Coincident(g14,g13)
    c: Block(g16)
    c: Block(g18)
    c: Coincident(g19,g18)
    c: Coincident(g17,g18)
    c: Parallel(g19,g17)
    c: Block(g17)
    c: Block(g19)
    c: Block(g21)
    c: Coincident(g22,g21)
    c: Coincident(g20,g21)
    c: Parallel(g22,g20)
    c: Block(g20)
    c: Block(g22)
    c: Block(g23)
    c: Coincident(g25,g23)
    c: Coincident(g25,g24)
    c: Block(g25)
    c: Block(g24)
    c: Coincident(g26,g19)
    c: Block(g26)
    c: Coincident(g27,g17)
    c: Block(g27)
    c: Coincident(g28,g20)
    c: Coincident(g29,g22)
    c: Block(g29)
    c: Block(g28)
    c: Coincident(g30,g5)
    c: Coincident(g30,g16)
    c: Block(g30)
    c: Coincident(g7,g28)
    c: Coincident(g11,g29)
    c: Coincident(g12,g27)
    c: Coincident(g13,g26)
    c: Coincident(g15,g24)
    c: Coincident(g31,g9)
    c: Coincident(g31,g16)
    c: Distance(g32) = 3.6
    c: Block(g32)
    c: Coincident(g33,g32)
    c: Coincident(g34,g8)
    c: Weight(g35) = 1
    c: Equal(g35, g36-g53) x18
    c: InternalAlignment(g35-g53 -> g54) x19
    c: InternalAlignment(g55-g71 -> g54) x17
    c: Block(g33)
    c: Block(g54)
    c: Coincident(g72,g33)
    c: Coincident(g73,g34)
    c: Block(g34)
    c: Parallel(g72,g34)
    c: Perpendicular(g73,g34)
    c: Coincident(g72,g73)
    c: Coincident(g74,g54)
    c: Coincident(g74,g23)
    c: Coincident(g75,g54)
    c: Coincident(g75,g32)
FEATURE [Sketcher::SketchObject] Sketch011  label="legBottomFront"
  FullyConstrained = true
  MapMode = 4
  Placement = pos=(0,0,0) rot=(0.57735,0.57735,0.57735;2.0944rad)
  sketch-geometry (13):
    g0: LineSegment StartX=-199.665 StartY=-138.314 StartZ=0 EndX=-200.721 EndY=-141.122 EndZ=0
    g1: LineSegment StartX=-200.721 StartY=-141.122 StartZ=0 EndX=-79.0409 EndY=-186.881 EndZ=0
    g2: ArcOfCircle CenterX=-71.1257 CenterY=-183.448 CenterZ=0 NormalX=0 NormalY=0 NormalZ=1 AngleXU=0 Radius=3.28025 StartAngle=3.43759 EndAngle=8.40938
    g3: LineSegment StartX=-74.4626 StartY=-174.707 StartZ=0 EndX=-76.2249 EndY=-179.393 EndZ=0
    g4: LineSegment StartX=-76.2249 StartY=-179.393 StartZ=0 EndX=-72.8553 EndY=-180.66 EndZ=0
    g5: Circle CenterX=-74.4626 CenterY=-174.707 CenterZ=0 NormalX=0 NormalY=0 NormalZ=1 AngleXU=0 Radius=1
    g6: Circle CenterX=-130.185 CenterY=-164.454 CenterZ=0 NormalX=0 NormalY=0 NormalZ=1 AngleXU=0 Radius=1
    g7: Circle CenterX=-199.665 CenterY=-138.314 CenterZ=0 NormalX=0 NormalY=0 NormalZ=1 AngleXU=0 Radius=1
    g8: BSplineCurve PolesCount=3 KnotsCount=2 Degree=2 IsPeriodic=0
    g9: GeomPoint X=-74.4626 Y=-174.707 Z=0
    g10: GeomPoint X=-199.665 Y=-138.314 Z=0
    g11: LineSegment StartX=-77.6329 StartY=-183.137 StartZ=0 EndX=-79.0409 EndY=-186.881 EndZ=0
    g12: LineSegment StartX=-77.6329 StartY=-183.137 StartZ=0 EndX=-74.2633 EndY=-184.404 EndZ=0
  constraints (24):
    c: Coincident(g1,g0)
    c: Block(g0)
    c: Perpendicular(g1,g0)
    c: Distance(g1) = 130
    c: Coincident(g4,g3)
    c: Coincident(g4,g2)
    c: Block(g2)
    c: Block(g4)
    c: Coincident(g8,g3)
    c: Weight(g5) = 1
    c: Equal(g5,g6)
    c: Equal(g5,g7)
    c: Coincident(g8,g0)
    c: InternalAlignment(g5,g8)
    c: InternalAlignment(g6,g8)
    c: InternalAlignment(g7,g8)
    c: InternalAlignment(g9,g8)
    c: InternalAlignment(g10,g8)
    c: Block(g8)
    c: Block(g3)
    c: Coincident(g11,g1)
    c: Coincident(g12,g11)
    c: Coincident(g12,g2)
    c: Block(g12)
